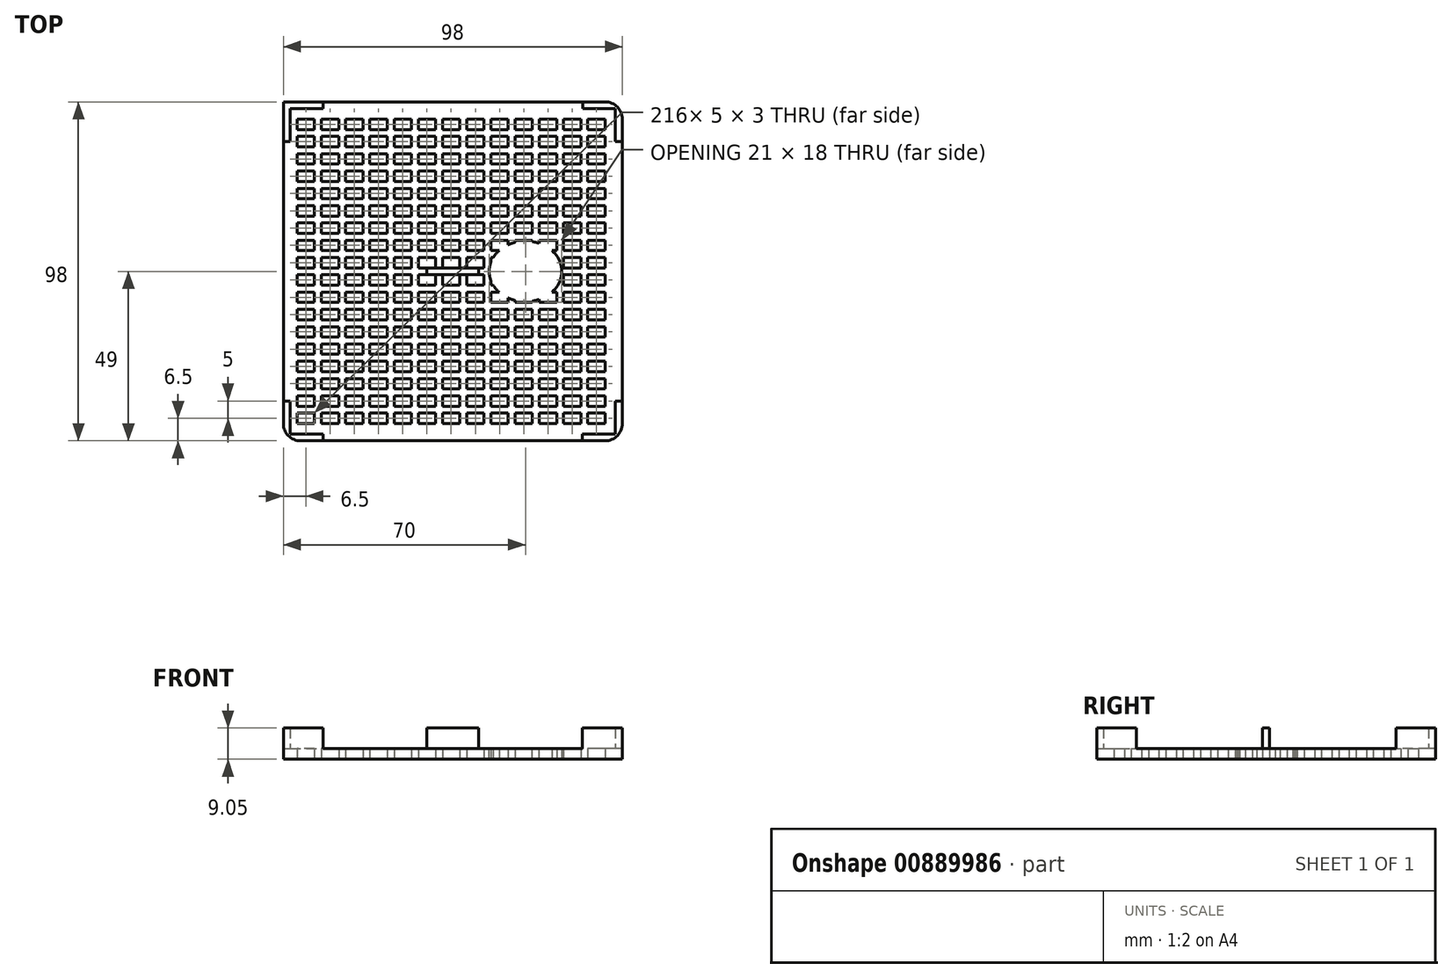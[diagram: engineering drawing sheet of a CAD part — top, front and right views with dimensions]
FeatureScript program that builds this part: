
annotation { "Feature Type Name" : "Feature", "Feature Type Description" : "" }
export const myFeature = defineFeature(function(context is Context, id is Id, definition is map)
    precondition{}
    {
        {
            var Q0;
            Q0=qCreatedBy(makeId("Top.planeOp"),FACE);
            var sketch = newSketch(context, id + "F0", { "sketchPlane" : qUnion([Q0])});
            skLineSegment(sketch, "E0.bottom", {"start": v(-49, 49) * mm, "end": v(49, 49) * mm});
            skLineSegment(sketch, "E0.top", {"start": v(-49, -49) * mm, "end": v(49, -49) * mm});
            skLineSegment(sketch, "E0.left", {"start": v(-49, 49) * mm, "end": v(-49, -49) * mm});
            skLineSegment(sketch, "E0.right", {"start": v(49, 49) * mm, "end": v(49, -49) * mm});
            skPoint(sketch, "E0.middle", {"position": v(0, 0) * mm});
            skLineSegment(sketch, "E1.bottom", {"start": v(-49, 49) * mm, "end": v(-42.5, 49) * mm});
            skLineSegment(sketch, "E1.top", {"start": v(-49, 42.5) * mm, "end": v(-42.5, 42.5) * mm});
            skLineSegment(sketch, "E1.left", {"start": v(-49, 49) * mm, "end": v(-49, 42.5) * mm});
            skLineSegment(sketch, "E1.right", {"start": v(-42.5, 49) * mm, "end": v(-42.5, 42.5) * mm});
            skLineSegment(sketch, "E2.bottom", {"start": v(-40, 41) * mm, "end": v(-45, 41) * mm});
            skLineSegment(sketch, "E2.top", {"start": v(-40, 44) * mm, "end": v(-45, 44) * mm});
            skLineSegment(sketch, "E2.left", {"start": v(-40, 41) * mm, "end": v(-40, 44) * mm});
            skLineSegment(sketch, "E2.right", {"start": v(-45, 41) * mm, "end": v(-45, 44) * mm});
            skPoint(sketch, "E2.middle", {"position": v(-42.5, 42.5) * mm});
            skLineSegment(sketch, "E3.1.0.0", {"start": v(-33, 41) * mm, "end": v(-33, 44) * mm});
            skLineSegment(sketch, "E3.1.0.1", {"start": v(-33, 44) * mm, "end": v(-38, 44) * mm});
            skLineSegment(sketch, "E3.1.0.2", {"start": v(-38, 41) * mm, "end": v(-38, 44) * mm});
            skLineSegment(sketch, "E3.1.0.3", {"start": v(-33, 41) * mm, "end": v(-38, 41) * mm});
            skLineSegment(sketch, "E3.2.0.0", {"start": v(-26, 41) * mm, "end": v(-26, 44) * mm});
            skLineSegment(sketch, "E3.2.0.1", {"start": v(-26, 44) * mm, "end": v(-31, 44) * mm});
            skLineSegment(sketch, "E3.2.0.2", {"start": v(-31, 41) * mm, "end": v(-31, 44) * mm});
            skLineSegment(sketch, "E3.2.0.3", {"start": v(-26, 41) * mm, "end": v(-31, 41) * mm});
            skLineSegment(sketch, "E3.3.0.0", {"start": v(-19, 41) * mm, "end": v(-19, 44) * mm});
            skLineSegment(sketch, "E3.3.0.1", {"start": v(-19, 44) * mm, "end": v(-24, 44) * mm});
            skLineSegment(sketch, "E3.3.0.2", {"start": v(-24, 41) * mm, "end": v(-24, 44) * mm});
            skLineSegment(sketch, "E3.3.0.3", {"start": v(-19, 41) * mm, "end": v(-24, 41) * mm});
            skLineSegment(sketch, "E3.4.0.0", {"start": v(-12, 41) * mm, "end": v(-12, 44) * mm});
            skLineSegment(sketch, "E3.4.0.1", {"start": v(-12, 44) * mm, "end": v(-17, 44) * mm});
            skLineSegment(sketch, "E3.4.0.2", {"start": v(-17, 41) * mm, "end": v(-17, 44) * mm});
            skLineSegment(sketch, "E3.4.0.3", {"start": v(-12, 41) * mm, "end": v(-17, 41) * mm});
            skLineSegment(sketch, "E3.5.0.0", {"start": v(-5, 41) * mm, "end": v(-5, 44) * mm});
            skLineSegment(sketch, "E3.5.0.1", {"start": v(-5, 44) * mm, "end": v(-10, 44) * mm});
            skLineSegment(sketch, "E3.5.0.2", {"start": v(-10, 41) * mm, "end": v(-10, 44) * mm});
            skLineSegment(sketch, "E3.5.0.3", {"start": v(-5, 41) * mm, "end": v(-10, 41) * mm});
            skLineSegment(sketch, "E3.6.0.0", {"start": v(2, 41) * mm, "end": v(2, 44) * mm});
            skLineSegment(sketch, "E3.6.0.1", {"start": v(2, 44) * mm, "end": v(-3, 44) * mm});
            skLineSegment(sketch, "E3.6.0.2", {"start": v(-3, 41) * mm, "end": v(-3, 44) * mm});
            skLineSegment(sketch, "E3.6.0.3", {"start": v(2, 41) * mm, "end": v(-3, 41) * mm});
            skLineSegment(sketch, "E3.7.0.0", {"start": v(9, 41) * mm, "end": v(9, 44) * mm});
            skLineSegment(sketch, "E3.7.0.1", {"start": v(9, 44) * mm, "end": v(4, 44) * mm});
            skLineSegment(sketch, "E3.7.0.2", {"start": v(4, 41) * mm, "end": v(4, 44) * mm});
            skLineSegment(sketch, "E3.7.0.3", {"start": v(9, 41) * mm, "end": v(4, 41) * mm});
            skLineSegment(sketch, "E3.8.0.0", {"start": v(16, 41) * mm, "end": v(16, 44) * mm});
            skLineSegment(sketch, "E3.8.0.1", {"start": v(16, 44) * mm, "end": v(11, 44) * mm});
            skLineSegment(sketch, "E3.8.0.2", {"start": v(11, 41) * mm, "end": v(11, 44) * mm});
            skLineSegment(sketch, "E3.8.0.3", {"start": v(16, 41) * mm, "end": v(11, 41) * mm});
            skLineSegment(sketch, "E3.9.0.0", {"start": v(23, 41) * mm, "end": v(23, 44) * mm});
            skLineSegment(sketch, "E3.9.0.1", {"start": v(23, 44) * mm, "end": v(18, 44) * mm});
            skLineSegment(sketch, "E3.9.0.2", {"start": v(18, 41) * mm, "end": v(18, 44) * mm});
            skLineSegment(sketch, "E3.9.0.3", {"start": v(23, 41) * mm, "end": v(18, 41) * mm});
            skLineSegment(sketch, "E3.10.0.0", {"start": v(30, 41) * mm, "end": v(30, 44) * mm});
            skLineSegment(sketch, "E3.10.0.1", {"start": v(30, 44) * mm, "end": v(25, 44) * mm});
            skLineSegment(sketch, "E3.10.0.2", {"start": v(25, 41) * mm, "end": v(25, 44) * mm});
            skLineSegment(sketch, "E3.10.0.3", {"start": v(30, 41) * mm, "end": v(25, 41) * mm});
            skLineSegment(sketch, "E4.0.11.0", {"start": v(37, 41) * mm, "end": v(37, 44) * mm});
            skLineSegment(sketch, "E4.3.11.0", {"start": v(37, 44) * mm, "end": v(32, 44) * mm});
            skLineSegment(sketch, "E4.6.11.0", {"start": v(32, 41) * mm, "end": v(32, 44) * mm});
            skLineSegment(sketch, "E4.9.11.0", {"start": v(37, 41) * mm, "end": v(32, 41) * mm});
            skLineSegment(sketch, "E5.0.12.0", {"start": v(44, 41) * mm, "end": v(44, 44) * mm});
            skLineSegment(sketch, "E5.3.12.0", {"start": v(44, 44) * mm, "end": v(39, 44) * mm});
            skLineSegment(sketch, "E5.6.12.0", {"start": v(39, 41) * mm, "end": v(39, 44) * mm});
            skLineSegment(sketch, "E5.9.12.0", {"start": v(44, 41) * mm, "end": v(39, 41) * mm});
            skLineSegment(sketch, "E6.1.0.0", {"start": v(-40, 36) * mm, "end": v(-45, 36) * mm});
            skLineSegment(sketch, "E6.1.0.1", {"start": v(-40, 36) * mm, "end": v(-40, 39) * mm});
            skLineSegment(sketch, "E6.1.0.2", {"start": v(-40, 39) * mm, "end": v(-45, 39) * mm});
            skLineSegment(sketch, "E6.1.0.3", {"start": v(-45, 36) * mm, "end": v(-45, 39) * mm});
            skLineSegment(sketch, "E6.2.0.0", {"start": v(-40, 31) * mm, "end": v(-45, 31) * mm});
            skLineSegment(sketch, "E6.2.0.1", {"start": v(-40, 31) * mm, "end": v(-40, 34) * mm});
            skLineSegment(sketch, "E6.2.0.2", {"start": v(-40, 34) * mm, "end": v(-45, 34) * mm});
            skLineSegment(sketch, "E6.2.0.3", {"start": v(-45, 31) * mm, "end": v(-45, 34) * mm});
            skLineSegment(sketch, "E6.3.0.0", {"start": v(-40, 26) * mm, "end": v(-45, 26) * mm});
            skLineSegment(sketch, "E6.3.0.1", {"start": v(-40, 26) * mm, "end": v(-40, 29) * mm});
            skLineSegment(sketch, "E6.3.0.2", {"start": v(-40, 29) * mm, "end": v(-45, 29) * mm});
            skLineSegment(sketch, "E6.3.0.3", {"start": v(-45, 26) * mm, "end": v(-45, 29) * mm});
            skLineSegment(sketch, "E6.4.0.0", {"start": v(-40, 21) * mm, "end": v(-45, 21) * mm});
            skLineSegment(sketch, "E6.4.0.1", {"start": v(-40, 21) * mm, "end": v(-40, 24) * mm});
            skLineSegment(sketch, "E6.4.0.2", {"start": v(-40, 24) * mm, "end": v(-45, 24) * mm});
            skLineSegment(sketch, "E6.4.0.3", {"start": v(-45, 21) * mm, "end": v(-45, 24) * mm});
            skLineSegment(sketch, "E6.5.0.0", {"start": v(-40, 16) * mm, "end": v(-45, 16) * mm});
            skLineSegment(sketch, "E6.5.0.1", {"start": v(-40, 16) * mm, "end": v(-40, 19) * mm});
            skLineSegment(sketch, "E6.5.0.2", {"start": v(-40, 19) * mm, "end": v(-45, 19) * mm});
            skLineSegment(sketch, "E6.5.0.3", {"start": v(-45, 16) * mm, "end": v(-45, 19) * mm});
            skLineSegment(sketch, "E6.6.0.0", {"start": v(-40, 11) * mm, "end": v(-45, 11) * mm});
            skLineSegment(sketch, "E6.6.0.1", {"start": v(-40, 11) * mm, "end": v(-40, 14) * mm});
            skLineSegment(sketch, "E6.6.0.2", {"start": v(-40, 14) * mm, "end": v(-45, 14) * mm});
            skLineSegment(sketch, "E6.6.0.3", {"start": v(-45, 11) * mm, "end": v(-45, 14) * mm});
            skLineSegment(sketch, "E6.7.0.0", {"start": v(-40, 6) * mm, "end": v(-45, 6) * mm});
            skLineSegment(sketch, "E6.7.0.1", {"start": v(-40, 6) * mm, "end": v(-40, 9) * mm});
            skLineSegment(sketch, "E6.7.0.2", {"start": v(-40, 9) * mm, "end": v(-45, 9) * mm});
            skLineSegment(sketch, "E6.7.0.3", {"start": v(-45, 6) * mm, "end": v(-45, 9) * mm});
            skLineSegment(sketch, "E6.8.0.0", {"start": v(-40, 1) * mm, "end": v(-45, 1) * mm});
            skLineSegment(sketch, "E6.8.0.1", {"start": v(-40, 1) * mm, "end": v(-40, 4) * mm});
            skLineSegment(sketch, "E6.8.0.2", {"start": v(-40, 4) * mm, "end": v(-45, 4) * mm});
            skLineSegment(sketch, "E6.8.0.3", {"start": v(-45, 1) * mm, "end": v(-45, 4) * mm});
            skLineSegment(sketch, "E6.9.0.0", {"start": v(-40, -4) * mm, "end": v(-45, -4) * mm});
            skLineSegment(sketch, "E6.9.0.1", {"start": v(-40, -4) * mm, "end": v(-40, -1) * mm});
            skLineSegment(sketch, "E6.9.0.2", {"start": v(-40, -1) * mm, "end": v(-45, -1) * mm});
            skLineSegment(sketch, "E6.9.0.3", {"start": v(-45, -4) * mm, "end": v(-45, -1) * mm});
            skLineSegment(sketch, "E6.10.0.0", {"start": v(-40, -9) * mm, "end": v(-45, -9) * mm});
            skLineSegment(sketch, "E6.10.0.1", {"start": v(-40, -9) * mm, "end": v(-40, -6) * mm});
            skLineSegment(sketch, "E6.10.0.2", {"start": v(-40, -6) * mm, "end": v(-45, -6) * mm});
            skLineSegment(sketch, "E6.10.0.3", {"start": v(-45, -9) * mm, "end": v(-45, -6) * mm});
            skLineSegment(sketch, "E6.11.0.0", {"start": v(-40, -14) * mm, "end": v(-45, -14) * mm});
            skLineSegment(sketch, "E6.11.0.1", {"start": v(-40, -14) * mm, "end": v(-40, -11) * mm});
            skLineSegment(sketch, "E6.11.0.2", {"start": v(-40, -11) * mm, "end": v(-45, -11) * mm});
            skLineSegment(sketch, "E6.11.0.3", {"start": v(-45, -14) * mm, "end": v(-45, -11) * mm});
            skLineSegment(sketch, "E6.12.0.0", {"start": v(-40, -19) * mm, "end": v(-45, -19) * mm});
            skLineSegment(sketch, "E6.12.0.1", {"start": v(-40, -19) * mm, "end": v(-40, -16) * mm});
            skLineSegment(sketch, "E6.12.0.2", {"start": v(-40, -16) * mm, "end": v(-45, -16) * mm});
            skLineSegment(sketch, "E6.12.0.3", {"start": v(-45, -19) * mm, "end": v(-45, -16) * mm});
            skLineSegment(sketch, "E6.13.0.0", {"start": v(-40, -24) * mm, "end": v(-45, -24) * mm});
            skLineSegment(sketch, "E6.13.0.1", {"start": v(-40, -24) * mm, "end": v(-40, -21) * mm});
            skLineSegment(sketch, "E6.13.0.2", {"start": v(-40, -21) * mm, "end": v(-45, -21) * mm});
            skLineSegment(sketch, "E6.13.0.3", {"start": v(-45, -24) * mm, "end": v(-45, -21) * mm});
            skLineSegment(sketch, "E6.14.0.0", {"start": v(-40, -29) * mm, "end": v(-45, -29) * mm});
            skLineSegment(sketch, "E6.14.0.1", {"start": v(-40, -29) * mm, "end": v(-40, -26) * mm});
            skLineSegment(sketch, "E6.14.0.2", {"start": v(-40, -26) * mm, "end": v(-45, -26) * mm});
            skLineSegment(sketch, "E6.14.0.3", {"start": v(-45, -29) * mm, "end": v(-45, -26) * mm});
            skLineSegment(sketch, "E6.15.0.0", {"start": v(-40, -34) * mm, "end": v(-45, -34) * mm});
            skLineSegment(sketch, "E6.15.0.1", {"start": v(-40, -34) * mm, "end": v(-40, -31) * mm});
            skLineSegment(sketch, "E6.15.0.2", {"start": v(-40, -31) * mm, "end": v(-45, -31) * mm});
            skLineSegment(sketch, "E6.15.0.3", {"start": v(-45, -34) * mm, "end": v(-45, -31) * mm});
            skLineSegment(sketch, "E6.16.0.0", {"start": v(-40, -39) * mm, "end": v(-45, -39) * mm});
            skLineSegment(sketch, "E6.16.0.1", {"start": v(-40, -39) * mm, "end": v(-40, -36) * mm});
            skLineSegment(sketch, "E6.16.0.2", {"start": v(-40, -36) * mm, "end": v(-45, -36) * mm});
            skLineSegment(sketch, "E6.16.0.3", {"start": v(-45, -39) * mm, "end": v(-45, -36) * mm});
            skLineSegment(sketch, "E6.17.0.0", {"start": v(-40, -44) * mm, "end": v(-45, -44) * mm});
            skLineSegment(sketch, "E6.17.0.1", {"start": v(-40, -44) * mm, "end": v(-40, -41) * mm});
            skLineSegment(sketch, "E6.17.0.2", {"start": v(-40, -41) * mm, "end": v(-45, -41) * mm});
            skLineSegment(sketch, "E6.17.0.3", {"start": v(-45, -44) * mm, "end": v(-45, -41) * mm});
            skLineSegment(sketch, "E7.1.0.0", {"start": v(-33, 39) * mm, "end": v(-38, 39) * mm});
            skLineSegment(sketch, "E7.1.0.1", {"start": v(-38, 36) * mm, "end": v(-38, 39) * mm});
            skLineSegment(sketch, "E7.1.0.2", {"start": v(-33, 36) * mm, "end": v(-33, 39) * mm});
            skLineSegment(sketch, "E7.1.0.3", {"start": v(-33, 36) * mm, "end": v(-38, 36) * mm});
            skLineSegment(sketch, "E7.2.0.0", {"start": v(-26, 39) * mm, "end": v(-31, 39) * mm});
            skLineSegment(sketch, "E7.2.0.1", {"start": v(-31, 36) * mm, "end": v(-31, 39) * mm});
            skLineSegment(sketch, "E7.2.0.2", {"start": v(-26, 36) * mm, "end": v(-26, 39) * mm});
            skLineSegment(sketch, "E7.2.0.3", {"start": v(-26, 36) * mm, "end": v(-31, 36) * mm});
            skLineSegment(sketch, "E7.3.0.0", {"start": v(-19, 39) * mm, "end": v(-24, 39) * mm});
            skLineSegment(sketch, "E7.3.0.1", {"start": v(-24, 36) * mm, "end": v(-24, 39) * mm});
            skLineSegment(sketch, "E7.3.0.2", {"start": v(-19, 36) * mm, "end": v(-19, 39) * mm});
            skLineSegment(sketch, "E7.3.0.3", {"start": v(-19, 36) * mm, "end": v(-24, 36) * mm});
            skLineSegment(sketch, "E7.4.0.0", {"start": v(-12, 39) * mm, "end": v(-17, 39) * mm});
            skLineSegment(sketch, "E7.4.0.1", {"start": v(-17, 36) * mm, "end": v(-17, 39) * mm});
            skLineSegment(sketch, "E7.4.0.2", {"start": v(-12, 36) * mm, "end": v(-12, 39) * mm});
            skLineSegment(sketch, "E7.4.0.3", {"start": v(-12, 36) * mm, "end": v(-17, 36) * mm});
            skLineSegment(sketch, "E7.5.0.0", {"start": v(-5, 39) * mm, "end": v(-10, 39) * mm});
            skLineSegment(sketch, "E7.5.0.1", {"start": v(-10, 36) * mm, "end": v(-10, 39) * mm});
            skLineSegment(sketch, "E7.5.0.2", {"start": v(-5, 36) * mm, "end": v(-5, 39) * mm});
            skLineSegment(sketch, "E7.5.0.3", {"start": v(-5, 36) * mm, "end": v(-10, 36) * mm});
            skLineSegment(sketch, "E7.6.0.0", {"start": v(2, 39) * mm, "end": v(-3, 39) * mm});
            skLineSegment(sketch, "E7.6.0.1", {"start": v(-3, 36) * mm, "end": v(-3, 39) * mm});
            skLineSegment(sketch, "E7.6.0.2", {"start": v(2, 36) * mm, "end": v(2, 39) * mm});
            skLineSegment(sketch, "E7.6.0.3", {"start": v(2, 36) * mm, "end": v(-3, 36) * mm});
            skLineSegment(sketch, "E7.7.0.0", {"start": v(9, 39) * mm, "end": v(4, 39) * mm});
            skLineSegment(sketch, "E7.7.0.1", {"start": v(4, 36) * mm, "end": v(4, 39) * mm});
            skLineSegment(sketch, "E7.7.0.2", {"start": v(9, 36) * mm, "end": v(9, 39) * mm});
            skLineSegment(sketch, "E7.7.0.3", {"start": v(9, 36) * mm, "end": v(4, 36) * mm});
            skLineSegment(sketch, "E7.8.0.0", {"start": v(16, 39) * mm, "end": v(11, 39) * mm});
            skLineSegment(sketch, "E7.8.0.1", {"start": v(11, 36) * mm, "end": v(11, 39) * mm});
            skLineSegment(sketch, "E7.8.0.2", {"start": v(16, 36) * mm, "end": v(16, 39) * mm});
            skLineSegment(sketch, "E7.8.0.3", {"start": v(16, 36) * mm, "end": v(11, 36) * mm});
            skLineSegment(sketch, "E7.9.0.0", {"start": v(23, 39) * mm, "end": v(18, 39) * mm});
            skLineSegment(sketch, "E7.9.0.1", {"start": v(18, 36) * mm, "end": v(18, 39) * mm});
            skLineSegment(sketch, "E7.9.0.2", {"start": v(23, 36) * mm, "end": v(23, 39) * mm});
            skLineSegment(sketch, "E7.9.0.3", {"start": v(23, 36) * mm, "end": v(18, 36) * mm});
            skLineSegment(sketch, "E7.10.0.0", {"start": v(30, 39) * mm, "end": v(25, 39) * mm});
            skLineSegment(sketch, "E7.10.0.1", {"start": v(25, 36) * mm, "end": v(25, 39) * mm});
            skLineSegment(sketch, "E7.10.0.2", {"start": v(30, 36) * mm, "end": v(30, 39) * mm});
            skLineSegment(sketch, "E7.10.0.3", {"start": v(30, 36) * mm, "end": v(25, 36) * mm});
            skLineSegment(sketch, "E7.11.0.0", {"start": v(37, 39) * mm, "end": v(32, 39) * mm});
            skLineSegment(sketch, "E7.11.0.1", {"start": v(32, 36) * mm, "end": v(32, 39) * mm});
            skLineSegment(sketch, "E7.11.0.2", {"start": v(37, 36) * mm, "end": v(37, 39) * mm});
            skLineSegment(sketch, "E7.11.0.3", {"start": v(37, 36) * mm, "end": v(32, 36) * mm});
            skLineSegment(sketch, "E7.12.0.0", {"start": v(44, 39) * mm, "end": v(39, 39) * mm});
            skLineSegment(sketch, "E7.12.0.1", {"start": v(39, 36) * mm, "end": v(39, 39) * mm});
            skLineSegment(sketch, "E7.12.0.2", {"start": v(44, 36) * mm, "end": v(44, 39) * mm});
            skLineSegment(sketch, "E7.12.0.3", {"start": v(44, 36) * mm, "end": v(39, 36) * mm});
            skLineSegment(sketch, "E8.1.0.0", {"start": v(-33, 31) * mm, "end": v(-33, 34) * mm});
            skLineSegment(sketch, "E8.1.0.1", {"start": v(-38, 31) * mm, "end": v(-38, 34) * mm});
            skLineSegment(sketch, "E8.1.0.2", {"start": v(-33, 34) * mm, "end": v(-38, 34) * mm});
            skLineSegment(sketch, "E8.1.0.3", {"start": v(-33, 31) * mm, "end": v(-38, 31) * mm});
            skLineSegment(sketch, "E8.2.0.0", {"start": v(-26, 31) * mm, "end": v(-26, 34) * mm});
            skLineSegment(sketch, "E8.2.0.1", {"start": v(-31, 31) * mm, "end": v(-31, 34) * mm});
            skLineSegment(sketch, "E8.2.0.2", {"start": v(-26, 34) * mm, "end": v(-31, 34) * mm});
            skLineSegment(sketch, "E8.2.0.3", {"start": v(-26, 31) * mm, "end": v(-31, 31) * mm});
            skLineSegment(sketch, "E8.3.0.0", {"start": v(-19, 31) * mm, "end": v(-19, 34) * mm});
            skLineSegment(sketch, "E8.3.0.1", {"start": v(-24, 31) * mm, "end": v(-24, 34) * mm});
            skLineSegment(sketch, "E8.3.0.2", {"start": v(-19, 34) * mm, "end": v(-24, 34) * mm});
            skLineSegment(sketch, "E8.3.0.3", {"start": v(-19, 31) * mm, "end": v(-24, 31) * mm});
            skLineSegment(sketch, "E8.4.0.0", {"start": v(-12, 31) * mm, "end": v(-12, 34) * mm});
            skLineSegment(sketch, "E8.4.0.1", {"start": v(-17, 31) * mm, "end": v(-17, 34) * mm});
            skLineSegment(sketch, "E8.4.0.2", {"start": v(-12, 34) * mm, "end": v(-17, 34) * mm});
            skLineSegment(sketch, "E8.4.0.3", {"start": v(-12, 31) * mm, "end": v(-17, 31) * mm});
            skLineSegment(sketch, "E8.5.0.0", {"start": v(-5, 31) * mm, "end": v(-5, 34) * mm});
            skLineSegment(sketch, "E8.5.0.1", {"start": v(-10, 31) * mm, "end": v(-10, 34) * mm});
            skLineSegment(sketch, "E8.5.0.2", {"start": v(-5, 34) * mm, "end": v(-10, 34) * mm});
            skLineSegment(sketch, "E8.5.0.3", {"start": v(-5, 31) * mm, "end": v(-10, 31) * mm});
            skLineSegment(sketch, "E8.6.0.0", {"start": v(2, 31) * mm, "end": v(2, 34) * mm});
            skLineSegment(sketch, "E8.6.0.1", {"start": v(-3, 31) * mm, "end": v(-3, 34) * mm});
            skLineSegment(sketch, "E8.6.0.2", {"start": v(2, 34) * mm, "end": v(-3, 34) * mm});
            skLineSegment(sketch, "E8.6.0.3", {"start": v(2, 31) * mm, "end": v(-3, 31) * mm});
            skLineSegment(sketch, "E8.7.0.0", {"start": v(9, 31) * mm, "end": v(9, 34) * mm});
            skLineSegment(sketch, "E8.7.0.1", {"start": v(4, 31) * mm, "end": v(4, 34) * mm});
            skLineSegment(sketch, "E8.7.0.2", {"start": v(9, 34) * mm, "end": v(4, 34) * mm});
            skLineSegment(sketch, "E8.7.0.3", {"start": v(9, 31) * mm, "end": v(4, 31) * mm});
            skLineSegment(sketch, "E8.8.0.0", {"start": v(16, 31) * mm, "end": v(16, 34) * mm});
            skLineSegment(sketch, "E8.8.0.1", {"start": v(11, 31) * mm, "end": v(11, 34) * mm});
            skLineSegment(sketch, "E8.8.0.2", {"start": v(16, 34) * mm, "end": v(11, 34) * mm});
            skLineSegment(sketch, "E8.8.0.3", {"start": v(16, 31) * mm, "end": v(11, 31) * mm});
            skLineSegment(sketch, "E8.9.0.0", {"start": v(23, 31) * mm, "end": v(23, 34) * mm});
            skLineSegment(sketch, "E8.9.0.1", {"start": v(18, 31) * mm, "end": v(18, 34) * mm});
            skLineSegment(sketch, "E8.9.0.2", {"start": v(23, 34) * mm, "end": v(18, 34) * mm});
            skLineSegment(sketch, "E8.9.0.3", {"start": v(23, 31) * mm, "end": v(18, 31) * mm});
            skLineSegment(sketch, "E8.10.0.0", {"start": v(30, 31) * mm, "end": v(30, 34) * mm});
            skLineSegment(sketch, "E8.10.0.1", {"start": v(25, 31) * mm, "end": v(25, 34) * mm});
            skLineSegment(sketch, "E8.10.0.2", {"start": v(30, 34) * mm, "end": v(25, 34) * mm});
            skLineSegment(sketch, "E8.10.0.3", {"start": v(30, 31) * mm, "end": v(25, 31) * mm});
            skLineSegment(sketch, "E8.11.0.0", {"start": v(37, 31) * mm, "end": v(37, 34) * mm});
            skLineSegment(sketch, "E8.11.0.1", {"start": v(32, 31) * mm, "end": v(32, 34) * mm});
            skLineSegment(sketch, "E8.11.0.2", {"start": v(37, 34) * mm, "end": v(32, 34) * mm});
            skLineSegment(sketch, "E8.11.0.3", {"start": v(37, 31) * mm, "end": v(32, 31) * mm});
            skLineSegment(sketch, "E8.12.0.0", {"start": v(44, 31) * mm, "end": v(44, 34) * mm});
            skLineSegment(sketch, "E8.12.0.1", {"start": v(39, 31) * mm, "end": v(39, 34) * mm});
            skLineSegment(sketch, "E8.12.0.2", {"start": v(44, 34) * mm, "end": v(39, 34) * mm});
            skLineSegment(sketch, "E8.12.0.3", {"start": v(44, 31) * mm, "end": v(39, 31) * mm});
            skLineSegment(sketch, "E9.1.0.0", {"start": v(-33, 29) * mm, "end": v(-38, 29) * mm});
            skLineSegment(sketch, "E9.1.0.1", {"start": v(-38, 26) * mm, "end": v(-38, 29) * mm});
            skLineSegment(sketch, "E9.1.0.2", {"start": v(-33, 26) * mm, "end": v(-38, 26) * mm});
            skLineSegment(sketch, "E9.1.0.3", {"start": v(-33, 26) * mm, "end": v(-33, 29) * mm});
            skLineSegment(sketch, "E9.2.0.0", {"start": v(-26, 29) * mm, "end": v(-31, 29) * mm});
            skLineSegment(sketch, "E9.2.0.1", {"start": v(-31, 26) * mm, "end": v(-31, 29) * mm});
            skLineSegment(sketch, "E9.2.0.2", {"start": v(-26, 26) * mm, "end": v(-31, 26) * mm});
            skLineSegment(sketch, "E9.2.0.3", {"start": v(-26, 26) * mm, "end": v(-26, 29) * mm});
            skLineSegment(sketch, "E9.3.0.0", {"start": v(-19, 29) * mm, "end": v(-24, 29) * mm});
            skLineSegment(sketch, "E9.3.0.1", {"start": v(-24, 26) * mm, "end": v(-24, 29) * mm});
            skLineSegment(sketch, "E9.3.0.2", {"start": v(-19, 26) * mm, "end": v(-24, 26) * mm});
            skLineSegment(sketch, "E9.3.0.3", {"start": v(-19, 26) * mm, "end": v(-19, 29) * mm});
            skLineSegment(sketch, "E9.4.0.0", {"start": v(-12, 29) * mm, "end": v(-17, 29) * mm});
            skLineSegment(sketch, "E9.4.0.1", {"start": v(-17, 26) * mm, "end": v(-17, 29) * mm});
            skLineSegment(sketch, "E9.4.0.2", {"start": v(-12, 26) * mm, "end": v(-17, 26) * mm});
            skLineSegment(sketch, "E9.4.0.3", {"start": v(-12, 26) * mm, "end": v(-12, 29) * mm});
            skLineSegment(sketch, "E9.5.0.0", {"start": v(-5, 29) * mm, "end": v(-10, 29) * mm});
            skLineSegment(sketch, "E9.5.0.1", {"start": v(-10, 26) * mm, "end": v(-10, 29) * mm});
            skLineSegment(sketch, "E9.5.0.2", {"start": v(-5, 26) * mm, "end": v(-10, 26) * mm});
            skLineSegment(sketch, "E9.5.0.3", {"start": v(-5, 26) * mm, "end": v(-5, 29) * mm});
            skLineSegment(sketch, "E9.6.0.0", {"start": v(2, 29) * mm, "end": v(-3, 29) * mm});
            skLineSegment(sketch, "E9.6.0.1", {"start": v(-3, 26) * mm, "end": v(-3, 29) * mm});
            skLineSegment(sketch, "E9.6.0.2", {"start": v(2, 26) * mm, "end": v(-3, 26) * mm});
            skLineSegment(sketch, "E9.6.0.3", {"start": v(2, 26) * mm, "end": v(2, 29) * mm});
            skLineSegment(sketch, "E9.7.0.0", {"start": v(9, 29) * mm, "end": v(4, 29) * mm});
            skLineSegment(sketch, "E9.7.0.1", {"start": v(4, 26) * mm, "end": v(4, 29) * mm});
            skLineSegment(sketch, "E9.7.0.2", {"start": v(9, 26) * mm, "end": v(4, 26) * mm});
            skLineSegment(sketch, "E9.7.0.3", {"start": v(9, 26) * mm, "end": v(9, 29) * mm});
            skLineSegment(sketch, "E9.8.0.0", {"start": v(16, 29) * mm, "end": v(11, 29) * mm});
            skLineSegment(sketch, "E9.8.0.1", {"start": v(11, 26) * mm, "end": v(11, 29) * mm});
            skLineSegment(sketch, "E9.8.0.2", {"start": v(16, 26) * mm, "end": v(11, 26) * mm});
            skLineSegment(sketch, "E9.8.0.3", {"start": v(16, 26) * mm, "end": v(16, 29) * mm});
            skLineSegment(sketch, "E9.9.0.0", {"start": v(23, 29) * mm, "end": v(18, 29) * mm});
            skLineSegment(sketch, "E9.9.0.1", {"start": v(18, 26) * mm, "end": v(18, 29) * mm});
            skLineSegment(sketch, "E9.9.0.2", {"start": v(23, 26) * mm, "end": v(18, 26) * mm});
            skLineSegment(sketch, "E9.9.0.3", {"start": v(23, 26) * mm, "end": v(23, 29) * mm});
            skLineSegment(sketch, "E9.10.0.0", {"start": v(30, 29) * mm, "end": v(25, 29) * mm});
            skLineSegment(sketch, "E9.10.0.1", {"start": v(25, 26) * mm, "end": v(25, 29) * mm});
            skLineSegment(sketch, "E9.10.0.2", {"start": v(30, 26) * mm, "end": v(25, 26) * mm});
            skLineSegment(sketch, "E9.10.0.3", {"start": v(30, 26) * mm, "end": v(30, 29) * mm});
            skLineSegment(sketch, "E9.11.0.0", {"start": v(37, 29) * mm, "end": v(32, 29) * mm});
            skLineSegment(sketch, "E9.11.0.1", {"start": v(32, 26) * mm, "end": v(32, 29) * mm});
            skLineSegment(sketch, "E9.11.0.2", {"start": v(37, 26) * mm, "end": v(32, 26) * mm});
            skLineSegment(sketch, "E9.11.0.3", {"start": v(37, 26) * mm, "end": v(37, 29) * mm});
            skLineSegment(sketch, "E9.12.0.0", {"start": v(44, 29) * mm, "end": v(39, 29) * mm});
            skLineSegment(sketch, "E9.12.0.1", {"start": v(39, 26) * mm, "end": v(39, 29) * mm});
            skLineSegment(sketch, "E9.12.0.2", {"start": v(44, 26) * mm, "end": v(39, 26) * mm});
            skLineSegment(sketch, "E9.12.0.3", {"start": v(44, 26) * mm, "end": v(44, 29) * mm});
            skLineSegment(sketch, "E10.1.0.0", {"start": v(-26, 21) * mm, "end": v(-31, 21) * mm});
            skLineSegment(sketch, "E10.1.0.1", {"start": v(-31, 21) * mm, "end": v(-31, 24) * mm});
            skLineSegment(sketch, "E10.1.0.2", {"start": v(-26, 24) * mm, "end": v(-31, 24) * mm});
            skLineSegment(sketch, "E10.1.0.3", {"start": v(-26, 21) * mm, "end": v(-26, 24) * mm});
            skLineSegment(sketch, "E10.1.0.4", {"start": v(-33, 21) * mm, "end": v(-33, 24) * mm});
            skLineSegment(sketch, "E10.1.0.5", {"start": v(-33, 24) * mm, "end": v(-38, 24) * mm});
            skLineSegment(sketch, "E10.1.0.6", {"start": v(-38, 21) * mm, "end": v(-38, 24) * mm});
            skLineSegment(sketch, "E10.1.0.7", {"start": v(-33, 21) * mm, "end": v(-38, 21) * mm});
            skLineSegment(sketch, "E10.1.0.8", {"start": v(-19, 21) * mm, "end": v(-24, 21) * mm});
            skLineSegment(sketch, "E10.1.0.9", {"start": v(-19, 24) * mm, "end": v(-24, 24) * mm});
            skLineSegment(sketch, "E10.1.0.10", {"start": v(-24, 21) * mm, "end": v(-24, 24) * mm});
            skLineSegment(sketch, "E10.1.0.11", {"start": v(-19, 21) * mm, "end": v(-19, 24) * mm});
            skLineSegment(sketch, "E10.1.0.12", {"start": v(-17, 21) * mm, "end": v(-17, 24) * mm});
            skLineSegment(sketch, "E10.1.0.13", {"start": v(-12, 24) * mm, "end": v(-17, 24) * mm});
            skLineSegment(sketch, "E10.1.0.14", {"start": v(-12, 21) * mm, "end": v(-17, 21) * mm});
            skLineSegment(sketch, "E10.1.0.15", {"start": v(-12, 21) * mm, "end": v(-12, 24) * mm});
            skLineSegment(sketch, "E10.1.0.16", {"start": v(-5, 24) * mm, "end": v(-10, 24) * mm});
            skLineSegment(sketch, "E10.1.0.17", {"start": v(-5, 21) * mm, "end": v(-10, 21) * mm});
            skLineSegment(sketch, "E10.1.0.18", {"start": v(-10, 21) * mm, "end": v(-10, 24) * mm});
            skLineSegment(sketch, "E10.1.0.19", {"start": v(-5, 21) * mm, "end": v(-5, 24) * mm});
            skLineSegment(sketch, "E10.2.0.0", {"start": v(-26, 16) * mm, "end": v(-31, 16) * mm});
            skLineSegment(sketch, "E10.2.0.1", {"start": v(-31, 16) * mm, "end": v(-31, 19) * mm});
            skLineSegment(sketch, "E10.2.0.2", {"start": v(-26, 19) * mm, "end": v(-31, 19) * mm});
            skLineSegment(sketch, "E10.2.0.3", {"start": v(-26, 16) * mm, "end": v(-26, 19) * mm});
            skLineSegment(sketch, "E10.2.0.4", {"start": v(-33, 16) * mm, "end": v(-33, 19) * mm});
            skLineSegment(sketch, "E10.2.0.5", {"start": v(-33, 19) * mm, "end": v(-38, 19) * mm});
            skLineSegment(sketch, "E10.2.0.6", {"start": v(-38, 16) * mm, "end": v(-38, 19) * mm});
            skLineSegment(sketch, "E10.2.0.7", {"start": v(-33, 16) * mm, "end": v(-38, 16) * mm});
            skLineSegment(sketch, "E10.2.0.8", {"start": v(-19, 16) * mm, "end": v(-24, 16) * mm});
            skLineSegment(sketch, "E10.2.0.9", {"start": v(-19, 19) * mm, "end": v(-24, 19) * mm});
            skLineSegment(sketch, "E10.2.0.10", {"start": v(-24, 16) * mm, "end": v(-24, 19) * mm});
            skLineSegment(sketch, "E10.2.0.11", {"start": v(-19, 16) * mm, "end": v(-19, 19) * mm});
            skLineSegment(sketch, "E10.2.0.12", {"start": v(-17, 16) * mm, "end": v(-17, 19) * mm});
            skLineSegment(sketch, "E10.2.0.13", {"start": v(-12, 19) * mm, "end": v(-17, 19) * mm});
            skLineSegment(sketch, "E10.2.0.14", {"start": v(-12, 16) * mm, "end": v(-17, 16) * mm});
            skLineSegment(sketch, "E10.2.0.15", {"start": v(-12, 16) * mm, "end": v(-12, 19) * mm});
            skLineSegment(sketch, "E10.2.0.16", {"start": v(-5, 19) * mm, "end": v(-10, 19) * mm});
            skLineSegment(sketch, "E10.2.0.17", {"start": v(-5, 16) * mm, "end": v(-10, 16) * mm});
            skLineSegment(sketch, "E10.2.0.18", {"start": v(-10, 16) * mm, "end": v(-10, 19) * mm});
            skLineSegment(sketch, "E10.2.0.19", {"start": v(-5, 16) * mm, "end": v(-5, 19) * mm});
            skLineSegment(sketch, "E10.3.0.0", {"start": v(-26, 11) * mm, "end": v(-31, 11) * mm});
            skLineSegment(sketch, "E10.3.0.1", {"start": v(-31, 11) * mm, "end": v(-31, 14) * mm});
            skLineSegment(sketch, "E10.3.0.2", {"start": v(-26, 14) * mm, "end": v(-31, 14) * mm});
            skLineSegment(sketch, "E10.3.0.3", {"start": v(-26, 11) * mm, "end": v(-26, 14) * mm});
            skLineSegment(sketch, "E10.3.0.4", {"start": v(-33, 11) * mm, "end": v(-33, 14) * mm});
            skLineSegment(sketch, "E10.3.0.5", {"start": v(-33, 14) * mm, "end": v(-38, 14) * mm});
            skLineSegment(sketch, "E10.3.0.6", {"start": v(-38, 11) * mm, "end": v(-38, 14) * mm});
            skLineSegment(sketch, "E10.3.0.7", {"start": v(-33, 11) * mm, "end": v(-38, 11) * mm});
            skLineSegment(sketch, "E10.3.0.8", {"start": v(-19, 11) * mm, "end": v(-24, 11) * mm});
            skLineSegment(sketch, "E10.3.0.9", {"start": v(-19, 14) * mm, "end": v(-24, 14) * mm});
            skLineSegment(sketch, "E10.3.0.10", {"start": v(-24, 11) * mm, "end": v(-24, 14) * mm});
            skLineSegment(sketch, "E10.3.0.11", {"start": v(-19, 11) * mm, "end": v(-19, 14) * mm});
            skLineSegment(sketch, "E10.3.0.12", {"start": v(-17, 11) * mm, "end": v(-17, 14) * mm});
            skLineSegment(sketch, "E10.3.0.13", {"start": v(-12, 14) * mm, "end": v(-17, 14) * mm});
            skLineSegment(sketch, "E10.3.0.14", {"start": v(-12, 11) * mm, "end": v(-17, 11) * mm});
            skLineSegment(sketch, "E10.3.0.15", {"start": v(-12, 11) * mm, "end": v(-12, 14) * mm});
            skLineSegment(sketch, "E10.3.0.16", {"start": v(-5, 14) * mm, "end": v(-10, 14) * mm});
            skLineSegment(sketch, "E10.3.0.17", {"start": v(-5, 11) * mm, "end": v(-10, 11) * mm});
            skLineSegment(sketch, "E10.3.0.18", {"start": v(-10, 11) * mm, "end": v(-10, 14) * mm});
            skLineSegment(sketch, "E10.3.0.19", {"start": v(-5, 11) * mm, "end": v(-5, 14) * mm});
            skLineSegment(sketch, "E10.4.0.0", {"start": v(-26, 6) * mm, "end": v(-31, 6) * mm});
            skLineSegment(sketch, "E10.4.0.1", {"start": v(-31, 6) * mm, "end": v(-31, 9) * mm});
            skLineSegment(sketch, "E10.4.0.2", {"start": v(-26, 9) * mm, "end": v(-31, 9) * mm});
            skLineSegment(sketch, "E10.4.0.3", {"start": v(-26, 6) * mm, "end": v(-26, 9) * mm});
            skLineSegment(sketch, "E10.4.0.4", {"start": v(-33, 6) * mm, "end": v(-33, 9) * mm});
            skLineSegment(sketch, "E10.4.0.5", {"start": v(-33, 9) * mm, "end": v(-38, 9) * mm});
            skLineSegment(sketch, "E10.4.0.6", {"start": v(-38, 6) * mm, "end": v(-38, 9) * mm});
            skLineSegment(sketch, "E10.4.0.7", {"start": v(-33, 6) * mm, "end": v(-38, 6) * mm});
            skLineSegment(sketch, "E10.4.0.8", {"start": v(-19, 6) * mm, "end": v(-24, 6) * mm});
            skLineSegment(sketch, "E10.4.0.9", {"start": v(-19, 9) * mm, "end": v(-24, 9) * mm});
            skLineSegment(sketch, "E10.4.0.10", {"start": v(-24, 6) * mm, "end": v(-24, 9) * mm});
            skLineSegment(sketch, "E10.4.0.11", {"start": v(-19, 6) * mm, "end": v(-19, 9) * mm});
            skLineSegment(sketch, "E10.4.0.12", {"start": v(-17, 6) * mm, "end": v(-17, 9) * mm});
            skLineSegment(sketch, "E10.4.0.13", {"start": v(-12, 9) * mm, "end": v(-17, 9) * mm});
            skLineSegment(sketch, "E10.4.0.14", {"start": v(-12, 6) * mm, "end": v(-17, 6) * mm});
            skLineSegment(sketch, "E10.4.0.15", {"start": v(-12, 6) * mm, "end": v(-12, 9) * mm});
            skLineSegment(sketch, "E10.4.0.16", {"start": v(-5, 9) * mm, "end": v(-10, 9) * mm});
            skLineSegment(sketch, "E10.4.0.17", {"start": v(-5, 6) * mm, "end": v(-10, 6) * mm});
            skLineSegment(sketch, "E10.4.0.18", {"start": v(-10, 6) * mm, "end": v(-10, 9) * mm});
            skLineSegment(sketch, "E10.4.0.19", {"start": v(-5, 6) * mm, "end": v(-5, 9) * mm});
            skLineSegment(sketch, "E10.5.0.0", {"start": v(-26, 1) * mm, "end": v(-31, 1) * mm});
            skLineSegment(sketch, "E10.5.0.1", {"start": v(-31, 1) * mm, "end": v(-31, 4) * mm});
            skLineSegment(sketch, "E10.5.0.2", {"start": v(-26, 4) * mm, "end": v(-31, 4) * mm});
            skLineSegment(sketch, "E10.5.0.3", {"start": v(-26, 1) * mm, "end": v(-26, 4) * mm});
            skLineSegment(sketch, "E10.5.0.4", {"start": v(-33, 1) * mm, "end": v(-33, 4) * mm});
            skLineSegment(sketch, "E10.5.0.5", {"start": v(-33, 4) * mm, "end": v(-38, 4) * mm});
            skLineSegment(sketch, "E10.5.0.6", {"start": v(-38, 1) * mm, "end": v(-38, 4) * mm});
            skLineSegment(sketch, "E10.5.0.7", {"start": v(-33, 1) * mm, "end": v(-38, 1) * mm});
            skLineSegment(sketch, "E10.5.0.8", {"start": v(-19, 1) * mm, "end": v(-24, 1) * mm});
            skLineSegment(sketch, "E10.5.0.9", {"start": v(-19, 4) * mm, "end": v(-24, 4) * mm});
            skLineSegment(sketch, "E10.5.0.10", {"start": v(-24, 1) * mm, "end": v(-24, 4) * mm});
            skLineSegment(sketch, "E10.5.0.11", {"start": v(-19, 1) * mm, "end": v(-19, 4) * mm});
            skLineSegment(sketch, "E10.5.0.12", {"start": v(-17, 1) * mm, "end": v(-17, 4) * mm});
            skLineSegment(sketch, "E10.5.0.13", {"start": v(-12, 4) * mm, "end": v(-17, 4) * mm});
            skLineSegment(sketch, "E10.5.0.14", {"start": v(-12, 1) * mm, "end": v(-17, 1) * mm});
            skLineSegment(sketch, "E10.5.0.15", {"start": v(-12, 1) * mm, "end": v(-12, 4) * mm});
            skLineSegment(sketch, "E10.5.0.16", {"start": v(-5, 4) * mm, "end": v(-10, 4) * mm});
            skLineSegment(sketch, "E10.5.0.17", {"start": v(-5, 1) * mm, "end": v(-10, 1) * mm});
            skLineSegment(sketch, "E10.5.0.18", {"start": v(-10, 1) * mm, "end": v(-10, 4) * mm});
            skLineSegment(sketch, "E10.5.0.19", {"start": v(-5, 1) * mm, "end": v(-5, 4) * mm});
            skLineSegment(sketch, "E10.6.0.0", {"start": v(-26, -4) * mm, "end": v(-31, -4) * mm});
            skLineSegment(sketch, "E10.6.0.1", {"start": v(-31, -4) * mm, "end": v(-31, -1) * mm});
            skLineSegment(sketch, "E10.6.0.2", {"start": v(-26, -1) * mm, "end": v(-31, -1) * mm});
            skLineSegment(sketch, "E10.6.0.3", {"start": v(-26, -4) * mm, "end": v(-26, -1) * mm});
            skLineSegment(sketch, "E10.6.0.4", {"start": v(-33, -4) * mm, "end": v(-33, -1) * mm});
            skLineSegment(sketch, "E10.6.0.5", {"start": v(-33, -1) * mm, "end": v(-38, -1) * mm});
            skLineSegment(sketch, "E10.6.0.6", {"start": v(-38, -4) * mm, "end": v(-38, -1) * mm});
            skLineSegment(sketch, "E10.6.0.7", {"start": v(-33, -4) * mm, "end": v(-38, -4) * mm});
            skLineSegment(sketch, "E10.6.0.8", {"start": v(-19, -4) * mm, "end": v(-24, -4) * mm});
            skLineSegment(sketch, "E10.6.0.9", {"start": v(-19, -1) * mm, "end": v(-24, -1) * mm});
            skLineSegment(sketch, "E10.6.0.10", {"start": v(-24, -4) * mm, "end": v(-24, -1) * mm});
            skLineSegment(sketch, "E10.6.0.11", {"start": v(-19, -4) * mm, "end": v(-19, -1) * mm});
            skLineSegment(sketch, "E10.6.0.12", {"start": v(-17, -4) * mm, "end": v(-17, -1) * mm});
            skLineSegment(sketch, "E10.6.0.13", {"start": v(-12, -1) * mm, "end": v(-17, -1) * mm});
            skLineSegment(sketch, "E10.6.0.14", {"start": v(-12, -4) * mm, "end": v(-17, -4) * mm});
            skLineSegment(sketch, "E10.6.0.15", {"start": v(-12, -4) * mm, "end": v(-12, -1) * mm});
            skLineSegment(sketch, "E10.6.0.16", {"start": v(-5, -1) * mm, "end": v(-10, -1) * mm});
            skLineSegment(sketch, "E10.6.0.17", {"start": v(-5, -4) * mm, "end": v(-10, -4) * mm});
            skLineSegment(sketch, "E10.6.0.18", {"start": v(-10, -4) * mm, "end": v(-10, -1) * mm});
            skLineSegment(sketch, "E10.6.0.19", {"start": v(-5, -4) * mm, "end": v(-5, -1) * mm});
            skLineSegment(sketch, "E10.7.0.0", {"start": v(-26, -9) * mm, "end": v(-31, -9) * mm});
            skLineSegment(sketch, "E10.7.0.1", {"start": v(-31, -9) * mm, "end": v(-31, -6) * mm});
            skLineSegment(sketch, "E10.7.0.2", {"start": v(-26, -6) * mm, "end": v(-31, -6) * mm});
            skLineSegment(sketch, "E10.7.0.3", {"start": v(-26, -9) * mm, "end": v(-26, -6) * mm});
            skLineSegment(sketch, "E10.7.0.4", {"start": v(-33, -9) * mm, "end": v(-33, -6) * mm});
            skLineSegment(sketch, "E10.7.0.5", {"start": v(-33, -6) * mm, "end": v(-38, -6) * mm});
            skLineSegment(sketch, "E10.7.0.6", {"start": v(-38, -9) * mm, "end": v(-38, -6) * mm});
            skLineSegment(sketch, "E10.7.0.7", {"start": v(-33, -9) * mm, "end": v(-38, -9) * mm});
            skLineSegment(sketch, "E10.7.0.8", {"start": v(-19, -9) * mm, "end": v(-24, -9) * mm});
            skLineSegment(sketch, "E10.7.0.9", {"start": v(-19, -6) * mm, "end": v(-24, -6) * mm});
            skLineSegment(sketch, "E10.7.0.10", {"start": v(-24, -9) * mm, "end": v(-24, -6) * mm});
            skLineSegment(sketch, "E10.7.0.11", {"start": v(-19, -9) * mm, "end": v(-19, -6) * mm});
            skLineSegment(sketch, "E10.7.0.12", {"start": v(-17, -9) * mm, "end": v(-17, -6) * mm});
            skLineSegment(sketch, "E10.7.0.13", {"start": v(-12, -6) * mm, "end": v(-17, -6) * mm});
            skLineSegment(sketch, "E10.7.0.14", {"start": v(-12, -9) * mm, "end": v(-17, -9) * mm});
            skLineSegment(sketch, "E10.7.0.15", {"start": v(-12, -9) * mm, "end": v(-12, -6) * mm});
            skLineSegment(sketch, "E10.7.0.16", {"start": v(-5, -6) * mm, "end": v(-10, -6) * mm});
            skLineSegment(sketch, "E10.7.0.17", {"start": v(-5, -9) * mm, "end": v(-10, -9) * mm});
            skLineSegment(sketch, "E10.7.0.18", {"start": v(-10, -9) * mm, "end": v(-10, -6) * mm});
            skLineSegment(sketch, "E10.7.0.19", {"start": v(-5, -9) * mm, "end": v(-5, -6) * mm});
            skLineSegment(sketch, "E10.8.0.0", {"start": v(-26, -14) * mm, "end": v(-31, -14) * mm});
            skLineSegment(sketch, "E10.8.0.1", {"start": v(-31, -14) * mm, "end": v(-31, -11) * mm});
            skLineSegment(sketch, "E10.8.0.2", {"start": v(-26, -11) * mm, "end": v(-31, -11) * mm});
            skLineSegment(sketch, "E10.8.0.3", {"start": v(-26, -14) * mm, "end": v(-26, -11) * mm});
            skLineSegment(sketch, "E10.8.0.4", {"start": v(-33, -14) * mm, "end": v(-33, -11) * mm});
            skLineSegment(sketch, "E10.8.0.5", {"start": v(-33, -11) * mm, "end": v(-38, -11) * mm});
            skLineSegment(sketch, "E10.8.0.6", {"start": v(-38, -14) * mm, "end": v(-38, -11) * mm});
            skLineSegment(sketch, "E10.8.0.7", {"start": v(-33, -14) * mm, "end": v(-38, -14) * mm});
            skLineSegment(sketch, "E10.8.0.8", {"start": v(-19, -14) * mm, "end": v(-24, -14) * mm});
            skLineSegment(sketch, "E10.8.0.9", {"start": v(-19, -11) * mm, "end": v(-24, -11) * mm});
            skLineSegment(sketch, "E10.8.0.10", {"start": v(-24, -14) * mm, "end": v(-24, -11) * mm});
            skLineSegment(sketch, "E10.8.0.11", {"start": v(-19, -14) * mm, "end": v(-19, -11) * mm});
            skLineSegment(sketch, "E10.8.0.12", {"start": v(-17, -14) * mm, "end": v(-17, -11) * mm});
            skLineSegment(sketch, "E10.8.0.13", {"start": v(-12, -11) * mm, "end": v(-17, -11) * mm});
            skLineSegment(sketch, "E10.8.0.14", {"start": v(-12, -14) * mm, "end": v(-17, -14) * mm});
            skLineSegment(sketch, "E10.8.0.15", {"start": v(-12, -14) * mm, "end": v(-12, -11) * mm});
            skLineSegment(sketch, "E10.8.0.16", {"start": v(-5, -11) * mm, "end": v(-10, -11) * mm});
            skLineSegment(sketch, "E10.8.0.17", {"start": v(-5, -14) * mm, "end": v(-10, -14) * mm});
            skLineSegment(sketch, "E10.8.0.18", {"start": v(-10, -14) * mm, "end": v(-10, -11) * mm});
            skLineSegment(sketch, "E10.8.0.19", {"start": v(-5, -14) * mm, "end": v(-5, -11) * mm});
            skLineSegment(sketch, "E10.9.0.0", {"start": v(-26, -19) * mm, "end": v(-31, -19) * mm});
            skLineSegment(sketch, "E10.9.0.1", {"start": v(-31, -19) * mm, "end": v(-31, -16) * mm});
            skLineSegment(sketch, "E10.9.0.2", {"start": v(-26, -16) * mm, "end": v(-31, -16) * mm});
            skLineSegment(sketch, "E10.9.0.3", {"start": v(-26, -19) * mm, "end": v(-26, -16) * mm});
            skLineSegment(sketch, "E10.9.0.4", {"start": v(-33, -19) * mm, "end": v(-33, -16) * mm});
            skLineSegment(sketch, "E10.9.0.5", {"start": v(-33, -16) * mm, "end": v(-38, -16) * mm});
            skLineSegment(sketch, "E10.9.0.6", {"start": v(-38, -19) * mm, "end": v(-38, -16) * mm});
            skLineSegment(sketch, "E10.9.0.7", {"start": v(-33, -19) * mm, "end": v(-38, -19) * mm});
            skLineSegment(sketch, "E10.9.0.8", {"start": v(-19, -19) * mm, "end": v(-24, -19) * mm});
            skLineSegment(sketch, "E10.9.0.9", {"start": v(-19, -16) * mm, "end": v(-24, -16) * mm});
            skLineSegment(sketch, "E10.9.0.10", {"start": v(-24, -19) * mm, "end": v(-24, -16) * mm});
            skLineSegment(sketch, "E10.9.0.11", {"start": v(-19, -19) * mm, "end": v(-19, -16) * mm});
            skLineSegment(sketch, "E10.9.0.12", {"start": v(-17, -19) * mm, "end": v(-17, -16) * mm});
            skLineSegment(sketch, "E10.9.0.13", {"start": v(-12, -16) * mm, "end": v(-17, -16) * mm});
            skLineSegment(sketch, "E10.9.0.14", {"start": v(-12, -19) * mm, "end": v(-17, -19) * mm});
            skLineSegment(sketch, "E10.9.0.15", {"start": v(-12, -19) * mm, "end": v(-12, -16) * mm});
            skLineSegment(sketch, "E10.9.0.16", {"start": v(-5, -16) * mm, "end": v(-10, -16) * mm});
            skLineSegment(sketch, "E10.9.0.17", {"start": v(-5, -19) * mm, "end": v(-10, -19) * mm});
            skLineSegment(sketch, "E10.9.0.18", {"start": v(-10, -19) * mm, "end": v(-10, -16) * mm});
            skLineSegment(sketch, "E10.9.0.19", {"start": v(-5, -19) * mm, "end": v(-5, -16) * mm});
            skLineSegment(sketch, "E10.10.0.0", {"start": v(-26, -24) * mm, "end": v(-31, -24) * mm});
            skLineSegment(sketch, "E10.10.0.1", {"start": v(-31, -24) * mm, "end": v(-31, -21) * mm});
            skLineSegment(sketch, "E10.10.0.2", {"start": v(-26, -21) * mm, "end": v(-31, -21) * mm});
            skLineSegment(sketch, "E10.10.0.3", {"start": v(-26, -24) * mm, "end": v(-26, -21) * mm});
            skLineSegment(sketch, "E10.10.0.4", {"start": v(-33, -24) * mm, "end": v(-33, -21) * mm});
            skLineSegment(sketch, "E10.10.0.5", {"start": v(-33, -21) * mm, "end": v(-38, -21) * mm});
            skLineSegment(sketch, "E10.10.0.6", {"start": v(-38, -24) * mm, "end": v(-38, -21) * mm});
            skLineSegment(sketch, "E10.10.0.7", {"start": v(-33, -24) * mm, "end": v(-38, -24) * mm});
            skLineSegment(sketch, "E10.10.0.8", {"start": v(-19, -24) * mm, "end": v(-24, -24) * mm});
            skLineSegment(sketch, "E10.10.0.9", {"start": v(-19, -21) * mm, "end": v(-24, -21) * mm});
            skLineSegment(sketch, "E10.10.0.10", {"start": v(-24, -24) * mm, "end": v(-24, -21) * mm});
            skLineSegment(sketch, "E10.10.0.11", {"start": v(-19, -24) * mm, "end": v(-19, -21) * mm});
            skLineSegment(sketch, "E10.10.0.12", {"start": v(-17, -24) * mm, "end": v(-17, -21) * mm});
            skLineSegment(sketch, "E10.10.0.13", {"start": v(-12, -21) * mm, "end": v(-17, -21) * mm});
            skLineSegment(sketch, "E10.10.0.14", {"start": v(-12, -24) * mm, "end": v(-17, -24) * mm});
            skLineSegment(sketch, "E10.10.0.15", {"start": v(-12, -24) * mm, "end": v(-12, -21) * mm});
            skLineSegment(sketch, "E10.10.0.16", {"start": v(-5, -21) * mm, "end": v(-10, -21) * mm});
            skLineSegment(sketch, "E10.10.0.17", {"start": v(-5, -24) * mm, "end": v(-10, -24) * mm});
            skLineSegment(sketch, "E10.10.0.18", {"start": v(-10, -24) * mm, "end": v(-10, -21) * mm});
            skLineSegment(sketch, "E10.10.0.19", {"start": v(-5, -24) * mm, "end": v(-5, -21) * mm});
            skLineSegment(sketch, "E10.11.0.0", {"start": v(-26, -29) * mm, "end": v(-31, -29) * mm});
            skLineSegment(sketch, "E10.11.0.1", {"start": v(-31, -29) * mm, "end": v(-31, -26) * mm});
            skLineSegment(sketch, "E10.11.0.2", {"start": v(-26, -26) * mm, "end": v(-31, -26) * mm});
            skLineSegment(sketch, "E10.11.0.3", {"start": v(-26, -29) * mm, "end": v(-26, -26) * mm});
            skLineSegment(sketch, "E10.11.0.4", {"start": v(-33, -29) * mm, "end": v(-33, -26) * mm});
            skLineSegment(sketch, "E10.11.0.5", {"start": v(-33, -26) * mm, "end": v(-38, -26) * mm});
            skLineSegment(sketch, "E10.11.0.6", {"start": v(-38, -29) * mm, "end": v(-38, -26) * mm});
            skLineSegment(sketch, "E10.11.0.7", {"start": v(-33, -29) * mm, "end": v(-38, -29) * mm});
            skLineSegment(sketch, "E10.11.0.8", {"start": v(-19, -29) * mm, "end": v(-24, -29) * mm});
            skLineSegment(sketch, "E10.11.0.9", {"start": v(-19, -26) * mm, "end": v(-24, -26) * mm});
            skLineSegment(sketch, "E10.11.0.10", {"start": v(-24, -29) * mm, "end": v(-24, -26) * mm});
            skLineSegment(sketch, "E10.11.0.11", {"start": v(-19, -29) * mm, "end": v(-19, -26) * mm});
            skLineSegment(sketch, "E10.11.0.12", {"start": v(-17, -29) * mm, "end": v(-17, -26) * mm});
            skLineSegment(sketch, "E10.11.0.13", {"start": v(-12, -26) * mm, "end": v(-17, -26) * mm});
            skLineSegment(sketch, "E10.11.0.14", {"start": v(-12, -29) * mm, "end": v(-17, -29) * mm});
            skLineSegment(sketch, "E10.11.0.15", {"start": v(-12, -29) * mm, "end": v(-12, -26) * mm});
            skLineSegment(sketch, "E10.11.0.16", {"start": v(-5, -26) * mm, "end": v(-10, -26) * mm});
            skLineSegment(sketch, "E10.11.0.17", {"start": v(-5, -29) * mm, "end": v(-10, -29) * mm});
            skLineSegment(sketch, "E10.11.0.18", {"start": v(-10, -29) * mm, "end": v(-10, -26) * mm});
            skLineSegment(sketch, "E10.11.0.19", {"start": v(-5, -29) * mm, "end": v(-5, -26) * mm});
            skLineSegment(sketch, "E10.12.0.0", {"start": v(-26, -34) * mm, "end": v(-31, -34) * mm});
            skLineSegment(sketch, "E10.12.0.1", {"start": v(-31, -34) * mm, "end": v(-31, -31) * mm});
            skLineSegment(sketch, "E10.12.0.2", {"start": v(-26, -31) * mm, "end": v(-31, -31) * mm});
            skLineSegment(sketch, "E10.12.0.3", {"start": v(-26, -34) * mm, "end": v(-26, -31) * mm});
            skLineSegment(sketch, "E10.12.0.4", {"start": v(-33, -34) * mm, "end": v(-33, -31) * mm});
            skLineSegment(sketch, "E10.12.0.5", {"start": v(-33, -31) * mm, "end": v(-38, -31) * mm});
            skLineSegment(sketch, "E10.12.0.6", {"start": v(-38, -34) * mm, "end": v(-38, -31) * mm});
            skLineSegment(sketch, "E10.12.0.7", {"start": v(-33, -34) * mm, "end": v(-38, -34) * mm});
            skLineSegment(sketch, "E10.12.0.8", {"start": v(-19, -34) * mm, "end": v(-24, -34) * mm});
            skLineSegment(sketch, "E10.12.0.9", {"start": v(-19, -31) * mm, "end": v(-24, -31) * mm});
            skLineSegment(sketch, "E10.12.0.10", {"start": v(-24, -34) * mm, "end": v(-24, -31) * mm});
            skLineSegment(sketch, "E10.12.0.11", {"start": v(-19, -34) * mm, "end": v(-19, -31) * mm});
            skLineSegment(sketch, "E10.12.0.12", {"start": v(-17, -34) * mm, "end": v(-17, -31) * mm});
            skLineSegment(sketch, "E10.12.0.13", {"start": v(-12, -31) * mm, "end": v(-17, -31) * mm});
            skLineSegment(sketch, "E10.12.0.14", {"start": v(-12, -34) * mm, "end": v(-17, -34) * mm});
            skLineSegment(sketch, "E10.12.0.15", {"start": v(-12, -34) * mm, "end": v(-12, -31) * mm});
            skLineSegment(sketch, "E10.12.0.16", {"start": v(-5, -31) * mm, "end": v(-10, -31) * mm});
            skLineSegment(sketch, "E10.12.0.17", {"start": v(-5, -34) * mm, "end": v(-10, -34) * mm});
            skLineSegment(sketch, "E10.12.0.18", {"start": v(-10, -34) * mm, "end": v(-10, -31) * mm});
            skLineSegment(sketch, "E10.12.0.19", {"start": v(-5, -34) * mm, "end": v(-5, -31) * mm});
            skLineSegment(sketch, "E10.13.0.0", {"start": v(-26, -39) * mm, "end": v(-31, -39) * mm});
            skLineSegment(sketch, "E10.13.0.1", {"start": v(-31, -39) * mm, "end": v(-31, -36) * mm});
            skLineSegment(sketch, "E10.13.0.2", {"start": v(-26, -36) * mm, "end": v(-31, -36) * mm});
            skLineSegment(sketch, "E10.13.0.3", {"start": v(-26, -39) * mm, "end": v(-26, -36) * mm});
            skLineSegment(sketch, "E10.13.0.4", {"start": v(-33, -39) * mm, "end": v(-33, -36) * mm});
            skLineSegment(sketch, "E10.13.0.5", {"start": v(-33, -36) * mm, "end": v(-38, -36) * mm});
            skLineSegment(sketch, "E10.13.0.6", {"start": v(-38, -39) * mm, "end": v(-38, -36) * mm});
            skLineSegment(sketch, "E10.13.0.7", {"start": v(-33, -39) * mm, "end": v(-38, -39) * mm});
            skLineSegment(sketch, "E10.13.0.8", {"start": v(-19, -39) * mm, "end": v(-24, -39) * mm});
            skLineSegment(sketch, "E10.13.0.9", {"start": v(-19, -36) * mm, "end": v(-24, -36) * mm});
            skLineSegment(sketch, "E10.13.0.10", {"start": v(-24, -39) * mm, "end": v(-24, -36) * mm});
            skLineSegment(sketch, "E10.13.0.11", {"start": v(-19, -39) * mm, "end": v(-19, -36) * mm});
            skLineSegment(sketch, "E10.13.0.12", {"start": v(-17, -39) * mm, "end": v(-17, -36) * mm});
            skLineSegment(sketch, "E10.13.0.13", {"start": v(-12, -36) * mm, "end": v(-17, -36) * mm});
            skLineSegment(sketch, "E10.13.0.14", {"start": v(-12, -39) * mm, "end": v(-17, -39) * mm});
            skLineSegment(sketch, "E10.13.0.15", {"start": v(-12, -39) * mm, "end": v(-12, -36) * mm});
            skLineSegment(sketch, "E10.13.0.16", {"start": v(-5, -36) * mm, "end": v(-10, -36) * mm});
            skLineSegment(sketch, "E10.13.0.17", {"start": v(-5, -39) * mm, "end": v(-10, -39) * mm});
            skLineSegment(sketch, "E10.13.0.18", {"start": v(-10, -39) * mm, "end": v(-10, -36) * mm});
            skLineSegment(sketch, "E10.13.0.19", {"start": v(-5, -39) * mm, "end": v(-5, -36) * mm});
            skLineSegment(sketch, "E10.14.0.0", {"start": v(-26, -44) * mm, "end": v(-31, -44) * mm});
            skLineSegment(sketch, "E10.14.0.1", {"start": v(-31, -44) * mm, "end": v(-31, -41) * mm});
            skLineSegment(sketch, "E10.14.0.2", {"start": v(-26, -41) * mm, "end": v(-31, -41) * mm});
            skLineSegment(sketch, "E10.14.0.3", {"start": v(-26, -44) * mm, "end": v(-26, -41) * mm});
            skLineSegment(sketch, "E10.14.0.4", {"start": v(-33, -44) * mm, "end": v(-33, -41) * mm});
            skLineSegment(sketch, "E10.14.0.5", {"start": v(-33, -41) * mm, "end": v(-38, -41) * mm});
            skLineSegment(sketch, "E10.14.0.6", {"start": v(-38, -44) * mm, "end": v(-38, -41) * mm});
            skLineSegment(sketch, "E10.14.0.7", {"start": v(-33, -44) * mm, "end": v(-38, -44) * mm});
            skLineSegment(sketch, "E10.14.0.8", {"start": v(-19, -44) * mm, "end": v(-24, -44) * mm});
            skLineSegment(sketch, "E10.14.0.9", {"start": v(-19, -41) * mm, "end": v(-24, -41) * mm});
            skLineSegment(sketch, "E10.14.0.10", {"start": v(-24, -44) * mm, "end": v(-24, -41) * mm});
            skLineSegment(sketch, "E10.14.0.11", {"start": v(-19, -44) * mm, "end": v(-19, -41) * mm});
            skLineSegment(sketch, "E10.14.0.12", {"start": v(-17, -44) * mm, "end": v(-17, -41) * mm});
            skLineSegment(sketch, "E10.14.0.13", {"start": v(-12, -41) * mm, "end": v(-17, -41) * mm});
            skLineSegment(sketch, "E10.14.0.14", {"start": v(-12, -44) * mm, "end": v(-17, -44) * mm});
            skLineSegment(sketch, "E10.14.0.15", {"start": v(-12, -44) * mm, "end": v(-12, -41) * mm});
            skLineSegment(sketch, "E10.14.0.16", {"start": v(-5, -41) * mm, "end": v(-10, -41) * mm});
            skLineSegment(sketch, "E10.14.0.17", {"start": v(-5, -44) * mm, "end": v(-10, -44) * mm});
            skLineSegment(sketch, "E10.14.0.18", {"start": v(-10, -44) * mm, "end": v(-10, -41) * mm});
            skLineSegment(sketch, "E10.14.0.19", {"start": v(-5, -44) * mm, "end": v(-5, -41) * mm});
            skLineSegment(sketch, "E10.direction1", {"start": v(-38, 26) * mm, "end": v(-38, 21) * mm, "construction": true});
            skLineSegment(sketch, "E11.1.0.0", {"start": v(-3, 21) * mm, "end": v(-3, 24) * mm});
            skLineSegment(sketch, "E11.1.0.1", {"start": v(2, 24) * mm, "end": v(-3, 24) * mm});
            skLineSegment(sketch, "E11.1.0.2", {"start": v(2, 21) * mm, "end": v(-3, 21) * mm});
            skLineSegment(sketch, "E11.1.0.3", {"start": v(2, 21) * mm, "end": v(2, 24) * mm});
            skLineSegment(sketch, "E11.1.0.4", {"start": v(9, 24) * mm, "end": v(4, 24) * mm});
            skLineSegment(sketch, "E11.1.0.5", {"start": v(4, 21) * mm, "end": v(4, 24) * mm});
            skLineSegment(sketch, "E11.1.0.6", {"start": v(9, 21) * mm, "end": v(4, 21) * mm});
            skLineSegment(sketch, "E11.1.0.7", {"start": v(9, 21) * mm, "end": v(9, 24) * mm});
            skLineSegment(sketch, "E11.1.0.8", {"start": v(16, 24) * mm, "end": v(11, 24) * mm});
            skLineSegment(sketch, "E11.1.0.9", {"start": v(11, 21) * mm, "end": v(11, 24) * mm});
            skLineSegment(sketch, "E11.1.0.10", {"start": v(16, 21) * mm, "end": v(11, 21) * mm});
            skLineSegment(sketch, "E11.1.0.11", {"start": v(16, 21) * mm, "end": v(16, 24) * mm});
            skLineSegment(sketch, "E11.1.0.12", {"start": v(18, 21) * mm, "end": v(18, 24) * mm});
            skLineSegment(sketch, "E11.1.0.13", {"start": v(23, 24) * mm, "end": v(18, 24) * mm});
            skLineSegment(sketch, "E11.1.0.14", {"start": v(23, 21) * mm, "end": v(18, 21) * mm});
            skLineSegment(sketch, "E11.1.0.15", {"start": v(23, 21) * mm, "end": v(23, 24) * mm});
            skLineSegment(sketch, "E11.1.0.16", {"start": v(30, 24) * mm, "end": v(25, 24) * mm});
            skLineSegment(sketch, "E11.1.0.17", {"start": v(25, 21) * mm, "end": v(25, 24) * mm});
            skLineSegment(sketch, "E11.1.0.18", {"start": v(30, 21) * mm, "end": v(25, 21) * mm});
            skLineSegment(sketch, "E11.1.0.19", {"start": v(30, 21) * mm, "end": v(30, 24) * mm});
            skLineSegment(sketch, "E11.1.0.20", {"start": v(37, 24) * mm, "end": v(32, 24) * mm});
            skLineSegment(sketch, "E11.1.0.21", {"start": v(37, 21) * mm, "end": v(32, 21) * mm});
            skLineSegment(sketch, "E11.1.0.22", {"start": v(32, 21) * mm, "end": v(32, 24) * mm});
            skLineSegment(sketch, "E11.1.0.23", {"start": v(37, 21) * mm, "end": v(37, 24) * mm});
            skLineSegment(sketch, "E11.1.0.24", {"start": v(44, 24) * mm, "end": v(39, 24) * mm});
            skLineSegment(sketch, "E11.1.0.25", {"start": v(39, 21) * mm, "end": v(39, 24) * mm});
            skLineSegment(sketch, "E11.1.0.26", {"start": v(44, 21) * mm, "end": v(39, 21) * mm});
            skLineSegment(sketch, "E11.1.0.27", {"start": v(44, 21) * mm, "end": v(44, 24) * mm});
            skLineSegment(sketch, "E11.2.0.0", {"start": v(-3, 16) * mm, "end": v(-3, 19) * mm});
            skLineSegment(sketch, "E11.2.0.1", {"start": v(2, 19) * mm, "end": v(-3, 19) * mm});
            skLineSegment(sketch, "E11.2.0.2", {"start": v(2, 16) * mm, "end": v(-3, 16) * mm});
            skLineSegment(sketch, "E11.2.0.3", {"start": v(2, 16) * mm, "end": v(2, 19) * mm});
            skLineSegment(sketch, "E11.2.0.4", {"start": v(9, 19) * mm, "end": v(4, 19) * mm});
            skLineSegment(sketch, "E11.2.0.5", {"start": v(4, 16) * mm, "end": v(4, 19) * mm});
            skLineSegment(sketch, "E11.2.0.6", {"start": v(9, 16) * mm, "end": v(4, 16) * mm});
            skLineSegment(sketch, "E11.2.0.7", {"start": v(9, 16) * mm, "end": v(9, 19) * mm});
            skLineSegment(sketch, "E11.2.0.8", {"start": v(16, 19) * mm, "end": v(11, 19) * mm});
            skLineSegment(sketch, "E11.2.0.9", {"start": v(11, 16) * mm, "end": v(11, 19) * mm});
            skLineSegment(sketch, "E11.2.0.10", {"start": v(16, 16) * mm, "end": v(11, 16) * mm});
            skLineSegment(sketch, "E11.2.0.11", {"start": v(16, 16) * mm, "end": v(16, 19) * mm});
            skLineSegment(sketch, "E11.2.0.12", {"start": v(18, 16) * mm, "end": v(18, 19) * mm});
            skLineSegment(sketch, "E11.2.0.13", {"start": v(23, 19) * mm, "end": v(18, 19) * mm});
            skLineSegment(sketch, "E11.2.0.14", {"start": v(23, 16) * mm, "end": v(18, 16) * mm});
            skLineSegment(sketch, "E11.2.0.15", {"start": v(23, 16) * mm, "end": v(23, 19) * mm});
            skLineSegment(sketch, "E11.2.0.16", {"start": v(30, 19) * mm, "end": v(25, 19) * mm});
            skLineSegment(sketch, "E11.2.0.17", {"start": v(25, 16) * mm, "end": v(25, 19) * mm});
            skLineSegment(sketch, "E11.2.0.18", {"start": v(30, 16) * mm, "end": v(25, 16) * mm});
            skLineSegment(sketch, "E11.2.0.19", {"start": v(30, 16) * mm, "end": v(30, 19) * mm});
            skLineSegment(sketch, "E11.2.0.20", {"start": v(37, 19) * mm, "end": v(32, 19) * mm});
            skLineSegment(sketch, "E11.2.0.21", {"start": v(37, 16) * mm, "end": v(32, 16) * mm});
            skLineSegment(sketch, "E11.2.0.22", {"start": v(32, 16) * mm, "end": v(32, 19) * mm});
            skLineSegment(sketch, "E11.2.0.23", {"start": v(37, 16) * mm, "end": v(37, 19) * mm});
            skLineSegment(sketch, "E11.2.0.24", {"start": v(44, 19) * mm, "end": v(39, 19) * mm});
            skLineSegment(sketch, "E11.2.0.25", {"start": v(39, 16) * mm, "end": v(39, 19) * mm});
            skLineSegment(sketch, "E11.2.0.26", {"start": v(44, 16) * mm, "end": v(39, 16) * mm});
            skLineSegment(sketch, "E11.2.0.27", {"start": v(44, 16) * mm, "end": v(44, 19) * mm});
            skLineSegment(sketch, "E11.3.0.0", {"start": v(-3, 11) * mm, "end": v(-3, 14) * mm});
            skLineSegment(sketch, "E11.3.0.1", {"start": v(2, 14) * mm, "end": v(-3, 14) * mm});
            skLineSegment(sketch, "E11.3.0.2", {"start": v(2, 11) * mm, "end": v(-3, 11) * mm});
            skLineSegment(sketch, "E11.3.0.3", {"start": v(2, 11) * mm, "end": v(2, 14) * mm});
            skLineSegment(sketch, "E11.3.0.4", {"start": v(9, 14) * mm, "end": v(4, 14) * mm});
            skLineSegment(sketch, "E11.3.0.5", {"start": v(4, 11) * mm, "end": v(4, 14) * mm});
            skLineSegment(sketch, "E11.3.0.6", {"start": v(9, 11) * mm, "end": v(4, 11) * mm});
            skLineSegment(sketch, "E11.3.0.7", {"start": v(9, 11) * mm, "end": v(9, 14) * mm});
            skLineSegment(sketch, "E11.3.0.8", {"start": v(16, 14) * mm, "end": v(11, 14) * mm});
            skLineSegment(sketch, "E11.3.0.9", {"start": v(11, 11) * mm, "end": v(11, 14) * mm});
            skLineSegment(sketch, "E11.3.0.10", {"start": v(16, 11) * mm, "end": v(11, 11) * mm});
            skLineSegment(sketch, "E11.3.0.11", {"start": v(16, 11) * mm, "end": v(16, 14) * mm});
            skLineSegment(sketch, "E11.3.0.12", {"start": v(18, 11) * mm, "end": v(18, 14) * mm});
            skLineSegment(sketch, "E11.3.0.13", {"start": v(23, 14) * mm, "end": v(18, 14) * mm});
            skLineSegment(sketch, "E11.3.0.14", {"start": v(23, 11) * mm, "end": v(18, 11) * mm});
            skLineSegment(sketch, "E11.3.0.15", {"start": v(23, 11) * mm, "end": v(23, 14) * mm});
            skLineSegment(sketch, "E11.3.0.16", {"start": v(30, 14) * mm, "end": v(25, 14) * mm});
            skLineSegment(sketch, "E11.3.0.17", {"start": v(25, 11) * mm, "end": v(25, 14) * mm});
            skLineSegment(sketch, "E11.3.0.18", {"start": v(30, 11) * mm, "end": v(25, 11) * mm});
            skLineSegment(sketch, "E11.3.0.19", {"start": v(30, 11) * mm, "end": v(30, 14) * mm});
            skLineSegment(sketch, "E11.3.0.20", {"start": v(37, 14) * mm, "end": v(32, 14) * mm});
            skLineSegment(sketch, "E11.3.0.21", {"start": v(37, 11) * mm, "end": v(32, 11) * mm});
            skLineSegment(sketch, "E11.3.0.22", {"start": v(32, 11) * mm, "end": v(32, 14) * mm});
            skLineSegment(sketch, "E11.3.0.23", {"start": v(37, 11) * mm, "end": v(37, 14) * mm});
            skLineSegment(sketch, "E11.3.0.24", {"start": v(44, 14) * mm, "end": v(39, 14) * mm});
            skLineSegment(sketch, "E11.3.0.25", {"start": v(39, 11) * mm, "end": v(39, 14) * mm});
            skLineSegment(sketch, "E11.3.0.26", {"start": v(44, 11) * mm, "end": v(39, 11) * mm});
            skLineSegment(sketch, "E11.3.0.27", {"start": v(44, 11) * mm, "end": v(44, 14) * mm});
            skLineSegment(sketch, "E11.4.0.0", {"start": v(-3, 6) * mm, "end": v(-3, 9) * mm});
            skLineSegment(sketch, "E11.4.0.1", {"start": v(2, 9) * mm, "end": v(-3, 9) * mm});
            skLineSegment(sketch, "E11.4.0.2", {"start": v(2, 6) * mm, "end": v(-3, 6) * mm});
            skLineSegment(sketch, "E11.4.0.3", {"start": v(2, 6) * mm, "end": v(2, 9) * mm});
            skLineSegment(sketch, "E11.4.0.4", {"start": v(9, 9) * mm, "end": v(4, 9) * mm});
            skLineSegment(sketch, "E11.4.0.5", {"start": v(4, 6) * mm, "end": v(4, 9) * mm});
            skLineSegment(sketch, "E11.4.0.6", {"start": v(9, 6) * mm, "end": v(4, 6) * mm});
            skLineSegment(sketch, "E11.4.0.7", {"start": v(9, 6) * mm, "end": v(9, 9) * mm});
            skLineSegment(sketch, "E11.4.0.8", {"start": v(16, 9) * mm, "end": v(11, 9) * mm});
            skLineSegment(sketch, "E11.4.0.9", {"start": v(11, 6) * mm, "end": v(11, 9) * mm});
            skLineSegment(sketch, "E11.4.0.10", {"start": v(16, 6) * mm, "end": v(11, 6) * mm});
            skLineSegment(sketch, "E11.4.0.11", {"start": v(16, 6) * mm, "end": v(16, 9) * mm});
            skLineSegment(sketch, "E11.4.0.12", {"start": v(18, 6) * mm, "end": v(18, 9) * mm});
            skLineSegment(sketch, "E11.4.0.13", {"start": v(23, 9) * mm, "end": v(18, 9) * mm});
            skLineSegment(sketch, "E11.4.0.14", {"start": v(23, 6) * mm, "end": v(18, 6) * mm});
            skLineSegment(sketch, "E11.4.0.15", {"start": v(23, 6) * mm, "end": v(23, 9) * mm});
            skLineSegment(sketch, "E11.4.0.16", {"start": v(30, 9) * mm, "end": v(25, 9) * mm});
            skLineSegment(sketch, "E11.4.0.17", {"start": v(25, 6) * mm, "end": v(25, 9) * mm});
            skLineSegment(sketch, "E11.4.0.18", {"start": v(30, 6) * mm, "end": v(25, 6) * mm});
            skLineSegment(sketch, "E11.4.0.19", {"start": v(30, 6) * mm, "end": v(30, 9) * mm});
            skLineSegment(sketch, "E11.4.0.20", {"start": v(37, 9) * mm, "end": v(32, 9) * mm});
            skLineSegment(sketch, "E11.4.0.21", {"start": v(37, 6) * mm, "end": v(32, 6) * mm});
            skLineSegment(sketch, "E11.4.0.22", {"start": v(32, 6) * mm, "end": v(32, 9) * mm});
            skLineSegment(sketch, "E11.4.0.23", {"start": v(37, 6) * mm, "end": v(37, 9) * mm});
            skLineSegment(sketch, "E11.4.0.24", {"start": v(44, 9) * mm, "end": v(39, 9) * mm});
            skLineSegment(sketch, "E11.4.0.25", {"start": v(39, 6) * mm, "end": v(39, 9) * mm});
            skLineSegment(sketch, "E11.4.0.26", {"start": v(44, 6) * mm, "end": v(39, 6) * mm});
            skLineSegment(sketch, "E11.4.0.27", {"start": v(44, 6) * mm, "end": v(44, 9) * mm});
            skLineSegment(sketch, "E11.5.0.0", {"start": v(-3, 1) * mm, "end": v(-3, 4) * mm});
            skLineSegment(sketch, "E11.5.0.1", {"start": v(2, 4) * mm, "end": v(-3, 4) * mm});
            skLineSegment(sketch, "E11.5.0.2", {"start": v(2, 1) * mm, "end": v(-3, 1) * mm});
            skLineSegment(sketch, "E11.5.0.3", {"start": v(2, 1) * mm, "end": v(2, 4) * mm});
            skLineSegment(sketch, "E11.5.0.4", {"start": v(9, 4) * mm, "end": v(4, 4) * mm});
            skLineSegment(sketch, "E11.5.0.5", {"start": v(4, 1) * mm, "end": v(4, 4) * mm});
            skLineSegment(sketch, "E11.5.0.6", {"start": v(9, 1) * mm, "end": v(4, 1) * mm});
            skLineSegment(sketch, "E11.5.0.7", {"start": v(9, 1) * mm, "end": v(9, 4) * mm});
            skLineSegment(sketch, "E11.5.0.8", {"start": v(16, 4) * mm, "end": v(11, 4) * mm});
            skLineSegment(sketch, "E11.5.0.9", {"start": v(11, 1) * mm, "end": v(11, 4) * mm});
            skLineSegment(sketch, "E11.5.0.10", {"start": v(16, 1) * mm, "end": v(11, 1) * mm});
            skLineSegment(sketch, "E11.5.0.11", {"start": v(16, 1) * mm, "end": v(16, 4) * mm});
            skLineSegment(sketch, "E11.5.0.12", {"start": v(18, 1) * mm, "end": v(18, 4) * mm});
            skLineSegment(sketch, "E11.5.0.13", {"start": v(23, 4) * mm, "end": v(18, 4) * mm});
            skLineSegment(sketch, "E11.5.0.14", {"start": v(23, 1) * mm, "end": v(18, 1) * mm});
            skLineSegment(sketch, "E11.5.0.15", {"start": v(23, 1) * mm, "end": v(23, 4) * mm});
            skLineSegment(sketch, "E11.5.0.16", {"start": v(30, 4) * mm, "end": v(25, 4) * mm});
            skLineSegment(sketch, "E11.5.0.17", {"start": v(25, 1) * mm, "end": v(25, 4) * mm});
            skLineSegment(sketch, "E11.5.0.18", {"start": v(30, 1) * mm, "end": v(25, 1) * mm});
            skLineSegment(sketch, "E11.5.0.19", {"start": v(30, 1) * mm, "end": v(30, 4) * mm});
            skLineSegment(sketch, "E11.5.0.20", {"start": v(37, 4) * mm, "end": v(32, 4) * mm});
            skLineSegment(sketch, "E11.5.0.21", {"start": v(37, 1) * mm, "end": v(32, 1) * mm});
            skLineSegment(sketch, "E11.5.0.22", {"start": v(32, 1) * mm, "end": v(32, 4) * mm});
            skLineSegment(sketch, "E11.5.0.23", {"start": v(37, 1) * mm, "end": v(37, 4) * mm});
            skLineSegment(sketch, "E11.5.0.24", {"start": v(44, 4) * mm, "end": v(39, 4) * mm});
            skLineSegment(sketch, "E11.5.0.25", {"start": v(39, 1) * mm, "end": v(39, 4) * mm});
            skLineSegment(sketch, "E11.5.0.26", {"start": v(44, 1) * mm, "end": v(39, 1) * mm});
            skLineSegment(sketch, "E11.5.0.27", {"start": v(44, 1) * mm, "end": v(44, 4) * mm});
            skLineSegment(sketch, "E11.6.0.0", {"start": v(-3, -4) * mm, "end": v(-3, -1) * mm});
            skLineSegment(sketch, "E11.6.0.1", {"start": v(2, -1) * mm, "end": v(-3, -1) * mm});
            skLineSegment(sketch, "E11.6.0.2", {"start": v(2, -4) * mm, "end": v(-3, -4) * mm});
            skLineSegment(sketch, "E11.6.0.3", {"start": v(2, -4) * mm, "end": v(2, -1) * mm});
            skLineSegment(sketch, "E11.6.0.4", {"start": v(9, -1) * mm, "end": v(4, -1) * mm});
            skLineSegment(sketch, "E11.6.0.5", {"start": v(4, -4) * mm, "end": v(4, -1) * mm});
            skLineSegment(sketch, "E11.6.0.6", {"start": v(9, -4) * mm, "end": v(4, -4) * mm});
            skLineSegment(sketch, "E11.6.0.7", {"start": v(9, -4) * mm, "end": v(9, -1) * mm});
            skLineSegment(sketch, "E11.6.0.8", {"start": v(16, -1) * mm, "end": v(11, -1) * mm});
            skLineSegment(sketch, "E11.6.0.9", {"start": v(11, -4) * mm, "end": v(11, -1) * mm});
            skLineSegment(sketch, "E11.6.0.10", {"start": v(16, -4) * mm, "end": v(11, -4) * mm});
            skLineSegment(sketch, "E11.6.0.11", {"start": v(16, -4) * mm, "end": v(16, -1) * mm});
            skLineSegment(sketch, "E11.6.0.12", {"start": v(18, -4) * mm, "end": v(18, -1) * mm});
            skLineSegment(sketch, "E11.6.0.13", {"start": v(23, -1) * mm, "end": v(18, -1) * mm});
            skLineSegment(sketch, "E11.6.0.14", {"start": v(23, -4) * mm, "end": v(18, -4) * mm});
            skLineSegment(sketch, "E11.6.0.15", {"start": v(23, -4) * mm, "end": v(23, -1) * mm});
            skLineSegment(sketch, "E11.6.0.16", {"start": v(30, -1) * mm, "end": v(25, -1) * mm});
            skLineSegment(sketch, "E11.6.0.17", {"start": v(25, -4) * mm, "end": v(25, -1) * mm});
            skLineSegment(sketch, "E11.6.0.18", {"start": v(30, -4) * mm, "end": v(25, -4) * mm});
            skLineSegment(sketch, "E11.6.0.19", {"start": v(30, -4) * mm, "end": v(30, -1) * mm});
            skLineSegment(sketch, "E11.6.0.20", {"start": v(37, -1) * mm, "end": v(32, -1) * mm});
            skLineSegment(sketch, "E11.6.0.21", {"start": v(37, -4) * mm, "end": v(32, -4) * mm});
            skLineSegment(sketch, "E11.6.0.22", {"start": v(32, -4) * mm, "end": v(32, -1) * mm});
            skLineSegment(sketch, "E11.6.0.23", {"start": v(37, -4) * mm, "end": v(37, -1) * mm});
            skLineSegment(sketch, "E11.6.0.24", {"start": v(44, -1) * mm, "end": v(39, -1) * mm});
            skLineSegment(sketch, "E11.6.0.25", {"start": v(39, -4) * mm, "end": v(39, -1) * mm});
            skLineSegment(sketch, "E11.6.0.26", {"start": v(44, -4) * mm, "end": v(39, -4) * mm});
            skLineSegment(sketch, "E11.6.0.27", {"start": v(44, -4) * mm, "end": v(44, -1) * mm});
            skLineSegment(sketch, "E11.7.0.0", {"start": v(-3, -9) * mm, "end": v(-3, -6) * mm});
            skLineSegment(sketch, "E11.7.0.1", {"start": v(2, -6) * mm, "end": v(-3, -6) * mm});
            skLineSegment(sketch, "E11.7.0.2", {"start": v(2, -9) * mm, "end": v(-3, -9) * mm});
            skLineSegment(sketch, "E11.7.0.3", {"start": v(2, -9) * mm, "end": v(2, -6) * mm});
            skLineSegment(sketch, "E11.7.0.4", {"start": v(9, -6) * mm, "end": v(4, -6) * mm});
            skLineSegment(sketch, "E11.7.0.5", {"start": v(4, -9) * mm, "end": v(4, -6) * mm});
            skLineSegment(sketch, "E11.7.0.6", {"start": v(9, -9) * mm, "end": v(4, -9) * mm});
            skLineSegment(sketch, "E11.7.0.7", {"start": v(9, -9) * mm, "end": v(9, -6) * mm});
            skLineSegment(sketch, "E11.7.0.8", {"start": v(16, -6) * mm, "end": v(11, -6) * mm});
            skLineSegment(sketch, "E11.7.0.9", {"start": v(11, -9) * mm, "end": v(11, -6) * mm});
            skLineSegment(sketch, "E11.7.0.10", {"start": v(16, -9) * mm, "end": v(11, -9) * mm});
            skLineSegment(sketch, "E11.7.0.11", {"start": v(16, -9) * mm, "end": v(16, -6) * mm});
            skLineSegment(sketch, "E11.7.0.12", {"start": v(18, -9) * mm, "end": v(18, -6) * mm});
            skLineSegment(sketch, "E11.7.0.13", {"start": v(23, -6) * mm, "end": v(18, -6) * mm});
            skLineSegment(sketch, "E11.7.0.14", {"start": v(23, -9) * mm, "end": v(18, -9) * mm});
            skLineSegment(sketch, "E11.7.0.15", {"start": v(23, -9) * mm, "end": v(23, -6) * mm});
            skLineSegment(sketch, "E11.7.0.16", {"start": v(30, -6) * mm, "end": v(25, -6) * mm});
            skLineSegment(sketch, "E11.7.0.17", {"start": v(25, -9) * mm, "end": v(25, -6) * mm});
            skLineSegment(sketch, "E11.7.0.18", {"start": v(30, -9) * mm, "end": v(25, -9) * mm});
            skLineSegment(sketch, "E11.7.0.19", {"start": v(30, -9) * mm, "end": v(30, -6) * mm});
            skLineSegment(sketch, "E11.7.0.20", {"start": v(37, -6) * mm, "end": v(32, -6) * mm});
            skLineSegment(sketch, "E11.7.0.21", {"start": v(37, -9) * mm, "end": v(32, -9) * mm});
            skLineSegment(sketch, "E11.7.0.22", {"start": v(32, -9) * mm, "end": v(32, -6) * mm});
            skLineSegment(sketch, "E11.7.0.23", {"start": v(37, -9) * mm, "end": v(37, -6) * mm});
            skLineSegment(sketch, "E11.7.0.24", {"start": v(44, -6) * mm, "end": v(39, -6) * mm});
            skLineSegment(sketch, "E11.7.0.25", {"start": v(39, -9) * mm, "end": v(39, -6) * mm});
            skLineSegment(sketch, "E11.7.0.26", {"start": v(44, -9) * mm, "end": v(39, -9) * mm});
            skLineSegment(sketch, "E11.7.0.27", {"start": v(44, -9) * mm, "end": v(44, -6) * mm});
            skLineSegment(sketch, "E11.8.0.0", {"start": v(-3, -14) * mm, "end": v(-3, -11) * mm});
            skLineSegment(sketch, "E11.8.0.1", {"start": v(2, -11) * mm, "end": v(-3, -11) * mm});
            skLineSegment(sketch, "E11.8.0.2", {"start": v(2, -14) * mm, "end": v(-3, -14) * mm});
            skLineSegment(sketch, "E11.8.0.3", {"start": v(2, -14) * mm, "end": v(2, -11) * mm});
            skLineSegment(sketch, "E11.8.0.4", {"start": v(9, -11) * mm, "end": v(4, -11) * mm});
            skLineSegment(sketch, "E11.8.0.5", {"start": v(4, -14) * mm, "end": v(4, -11) * mm});
            skLineSegment(sketch, "E11.8.0.6", {"start": v(9, -14) * mm, "end": v(4, -14) * mm});
            skLineSegment(sketch, "E11.8.0.7", {"start": v(9, -14) * mm, "end": v(9, -11) * mm});
            skLineSegment(sketch, "E11.8.0.8", {"start": v(16, -11) * mm, "end": v(11, -11) * mm});
            skLineSegment(sketch, "E11.8.0.9", {"start": v(11, -14) * mm, "end": v(11, -11) * mm});
            skLineSegment(sketch, "E11.8.0.10", {"start": v(16, -14) * mm, "end": v(11, -14) * mm});
            skLineSegment(sketch, "E11.8.0.11", {"start": v(16, -14) * mm, "end": v(16, -11) * mm});
            skLineSegment(sketch, "E11.8.0.12", {"start": v(18, -14) * mm, "end": v(18, -11) * mm});
            skLineSegment(sketch, "E11.8.0.13", {"start": v(23, -11) * mm, "end": v(18, -11) * mm});
            skLineSegment(sketch, "E11.8.0.14", {"start": v(23, -14) * mm, "end": v(18, -14) * mm});
            skLineSegment(sketch, "E11.8.0.15", {"start": v(23, -14) * mm, "end": v(23, -11) * mm});
            skLineSegment(sketch, "E11.8.0.16", {"start": v(30, -11) * mm, "end": v(25, -11) * mm});
            skLineSegment(sketch, "E11.8.0.17", {"start": v(25, -14) * mm, "end": v(25, -11) * mm});
            skLineSegment(sketch, "E11.8.0.18", {"start": v(30, -14) * mm, "end": v(25, -14) * mm});
            skLineSegment(sketch, "E11.8.0.19", {"start": v(30, -14) * mm, "end": v(30, -11) * mm});
            skLineSegment(sketch, "E11.8.0.20", {"start": v(37, -11) * mm, "end": v(32, -11) * mm});
            skLineSegment(sketch, "E11.8.0.21", {"start": v(37, -14) * mm, "end": v(32, -14) * mm});
            skLineSegment(sketch, "E11.8.0.22", {"start": v(32, -14) * mm, "end": v(32, -11) * mm});
            skLineSegment(sketch, "E11.8.0.23", {"start": v(37, -14) * mm, "end": v(37, -11) * mm});
            skLineSegment(sketch, "E11.8.0.24", {"start": v(44, -11) * mm, "end": v(39, -11) * mm});
            skLineSegment(sketch, "E11.8.0.25", {"start": v(39, -14) * mm, "end": v(39, -11) * mm});
            skLineSegment(sketch, "E11.8.0.26", {"start": v(44, -14) * mm, "end": v(39, -14) * mm});
            skLineSegment(sketch, "E11.8.0.27", {"start": v(44, -14) * mm, "end": v(44, -11) * mm});
            skLineSegment(sketch, "E11.9.0.0", {"start": v(-3, -19) * mm, "end": v(-3, -16) * mm});
            skLineSegment(sketch, "E11.9.0.1", {"start": v(2, -16) * mm, "end": v(-3, -16) * mm});
            skLineSegment(sketch, "E11.9.0.2", {"start": v(2, -19) * mm, "end": v(-3, -19) * mm});
            skLineSegment(sketch, "E11.9.0.3", {"start": v(2, -19) * mm, "end": v(2, -16) * mm});
            skLineSegment(sketch, "E11.9.0.4", {"start": v(9, -16) * mm, "end": v(4, -16) * mm});
            skLineSegment(sketch, "E11.9.0.5", {"start": v(4, -19) * mm, "end": v(4, -16) * mm});
            skLineSegment(sketch, "E11.9.0.6", {"start": v(9, -19) * mm, "end": v(4, -19) * mm});
            skLineSegment(sketch, "E11.9.0.7", {"start": v(9, -19) * mm, "end": v(9, -16) * mm});
            skLineSegment(sketch, "E11.9.0.8", {"start": v(16, -16) * mm, "end": v(11, -16) * mm});
            skLineSegment(sketch, "E11.9.0.9", {"start": v(11, -19) * mm, "end": v(11, -16) * mm});
            skLineSegment(sketch, "E11.9.0.10", {"start": v(16, -19) * mm, "end": v(11, -19) * mm});
            skLineSegment(sketch, "E11.9.0.11", {"start": v(16, -19) * mm, "end": v(16, -16) * mm});
            skLineSegment(sketch, "E11.9.0.12", {"start": v(18, -19) * mm, "end": v(18, -16) * mm});
            skLineSegment(sketch, "E11.9.0.13", {"start": v(23, -16) * mm, "end": v(18, -16) * mm});
            skLineSegment(sketch, "E11.9.0.14", {"start": v(23, -19) * mm, "end": v(18, -19) * mm});
            skLineSegment(sketch, "E11.9.0.15", {"start": v(23, -19) * mm, "end": v(23, -16) * mm});
            skLineSegment(sketch, "E11.9.0.16", {"start": v(30, -16) * mm, "end": v(25, -16) * mm});
            skLineSegment(sketch, "E11.9.0.17", {"start": v(25, -19) * mm, "end": v(25, -16) * mm});
            skLineSegment(sketch, "E11.9.0.18", {"start": v(30, -19) * mm, "end": v(25, -19) * mm});
            skLineSegment(sketch, "E11.9.0.19", {"start": v(30, -19) * mm, "end": v(30, -16) * mm});
            skLineSegment(sketch, "E11.9.0.20", {"start": v(37, -16) * mm, "end": v(32, -16) * mm});
            skLineSegment(sketch, "E11.9.0.21", {"start": v(37, -19) * mm, "end": v(32, -19) * mm});
            skLineSegment(sketch, "E11.9.0.22", {"start": v(32, -19) * mm, "end": v(32, -16) * mm});
            skLineSegment(sketch, "E11.9.0.23", {"start": v(37, -19) * mm, "end": v(37, -16) * mm});
            skLineSegment(sketch, "E11.9.0.24", {"start": v(44, -16) * mm, "end": v(39, -16) * mm});
            skLineSegment(sketch, "E11.9.0.25", {"start": v(39, -19) * mm, "end": v(39, -16) * mm});
            skLineSegment(sketch, "E11.9.0.26", {"start": v(44, -19) * mm, "end": v(39, -19) * mm});
            skLineSegment(sketch, "E11.9.0.27", {"start": v(44, -19) * mm, "end": v(44, -16) * mm});
            skLineSegment(sketch, "E11.10.0.0", {"start": v(-3, -24) * mm, "end": v(-3, -21) * mm});
            skLineSegment(sketch, "E11.10.0.1", {"start": v(2, -21) * mm, "end": v(-3, -21) * mm});
            skLineSegment(sketch, "E11.10.0.2", {"start": v(2, -24) * mm, "end": v(-3, -24) * mm});
            skLineSegment(sketch, "E11.10.0.3", {"start": v(2, -24) * mm, "end": v(2, -21) * mm});
            skLineSegment(sketch, "E11.10.0.4", {"start": v(9, -21) * mm, "end": v(4, -21) * mm});
            skLineSegment(sketch, "E11.10.0.5", {"start": v(4, -24) * mm, "end": v(4, -21) * mm});
            skLineSegment(sketch, "E11.10.0.6", {"start": v(9, -24) * mm, "end": v(4, -24) * mm});
            skLineSegment(sketch, "E11.10.0.7", {"start": v(9, -24) * mm, "end": v(9, -21) * mm});
            skLineSegment(sketch, "E11.10.0.8", {"start": v(16, -21) * mm, "end": v(11, -21) * mm});
            skLineSegment(sketch, "E11.10.0.9", {"start": v(11, -24) * mm, "end": v(11, -21) * mm});
            skLineSegment(sketch, "E11.10.0.10", {"start": v(16, -24) * mm, "end": v(11, -24) * mm});
            skLineSegment(sketch, "E11.10.0.11", {"start": v(16, -24) * mm, "end": v(16, -21) * mm});
            skLineSegment(sketch, "E11.10.0.12", {"start": v(18, -24) * mm, "end": v(18, -21) * mm});
            skLineSegment(sketch, "E11.10.0.13", {"start": v(23, -21) * mm, "end": v(18, -21) * mm});
            skLineSegment(sketch, "E11.10.0.14", {"start": v(23, -24) * mm, "end": v(18, -24) * mm});
            skLineSegment(sketch, "E11.10.0.15", {"start": v(23, -24) * mm, "end": v(23, -21) * mm});
            skLineSegment(sketch, "E11.10.0.16", {"start": v(30, -21) * mm, "end": v(25, -21) * mm});
            skLineSegment(sketch, "E11.10.0.17", {"start": v(25, -24) * mm, "end": v(25, -21) * mm});
            skLineSegment(sketch, "E11.10.0.18", {"start": v(30, -24) * mm, "end": v(25, -24) * mm});
            skLineSegment(sketch, "E11.10.0.19", {"start": v(30, -24) * mm, "end": v(30, -21) * mm});
            skLineSegment(sketch, "E11.10.0.20", {"start": v(37, -21) * mm, "end": v(32, -21) * mm});
            skLineSegment(sketch, "E11.10.0.21", {"start": v(37, -24) * mm, "end": v(32, -24) * mm});
            skLineSegment(sketch, "E11.10.0.22", {"start": v(32, -24) * mm, "end": v(32, -21) * mm});
            skLineSegment(sketch, "E11.10.0.23", {"start": v(37, -24) * mm, "end": v(37, -21) * mm});
            skLineSegment(sketch, "E11.10.0.24", {"start": v(44, -21) * mm, "end": v(39, -21) * mm});
            skLineSegment(sketch, "E11.10.0.25", {"start": v(39, -24) * mm, "end": v(39, -21) * mm});
            skLineSegment(sketch, "E11.10.0.26", {"start": v(44, -24) * mm, "end": v(39, -24) * mm});
            skLineSegment(sketch, "E11.10.0.27", {"start": v(44, -24) * mm, "end": v(44, -21) * mm});
            skLineSegment(sketch, "E11.11.0.0", {"start": v(-3, -29) * mm, "end": v(-3, -26) * mm});
            skLineSegment(sketch, "E11.11.0.1", {"start": v(2, -26) * mm, "end": v(-3, -26) * mm});
            skLineSegment(sketch, "E11.11.0.2", {"start": v(2, -29) * mm, "end": v(-3, -29) * mm});
            skLineSegment(sketch, "E11.11.0.3", {"start": v(2, -29) * mm, "end": v(2, -26) * mm});
            skLineSegment(sketch, "E11.11.0.4", {"start": v(9, -26) * mm, "end": v(4, -26) * mm});
            skLineSegment(sketch, "E11.11.0.5", {"start": v(4, -29) * mm, "end": v(4, -26) * mm});
            skLineSegment(sketch, "E11.11.0.6", {"start": v(9, -29) * mm, "end": v(4, -29) * mm});
            skLineSegment(sketch, "E11.11.0.7", {"start": v(9, -29) * mm, "end": v(9, -26) * mm});
            skLineSegment(sketch, "E11.11.0.8", {"start": v(16, -26) * mm, "end": v(11, -26) * mm});
            skLineSegment(sketch, "E11.11.0.9", {"start": v(11, -29) * mm, "end": v(11, -26) * mm});
            skLineSegment(sketch, "E11.11.0.10", {"start": v(16, -29) * mm, "end": v(11, -29) * mm});
            skLineSegment(sketch, "E11.11.0.11", {"start": v(16, -29) * mm, "end": v(16, -26) * mm});
            skLineSegment(sketch, "E11.11.0.12", {"start": v(18, -29) * mm, "end": v(18, -26) * mm});
            skLineSegment(sketch, "E11.11.0.13", {"start": v(23, -26) * mm, "end": v(18, -26) * mm});
            skLineSegment(sketch, "E11.11.0.14", {"start": v(23, -29) * mm, "end": v(18, -29) * mm});
            skLineSegment(sketch, "E11.11.0.15", {"start": v(23, -29) * mm, "end": v(23, -26) * mm});
            skLineSegment(sketch, "E11.11.0.16", {"start": v(30, -26) * mm, "end": v(25, -26) * mm});
            skLineSegment(sketch, "E11.11.0.17", {"start": v(25, -29) * mm, "end": v(25, -26) * mm});
            skLineSegment(sketch, "E11.11.0.18", {"start": v(30, -29) * mm, "end": v(25, -29) * mm});
            skLineSegment(sketch, "E11.11.0.19", {"start": v(30, -29) * mm, "end": v(30, -26) * mm});
            skLineSegment(sketch, "E11.11.0.20", {"start": v(37, -26) * mm, "end": v(32, -26) * mm});
            skLineSegment(sketch, "E11.11.0.21", {"start": v(37, -29) * mm, "end": v(32, -29) * mm});
            skLineSegment(sketch, "E11.11.0.22", {"start": v(32, -29) * mm, "end": v(32, -26) * mm});
            skLineSegment(sketch, "E11.11.0.23", {"start": v(37, -29) * mm, "end": v(37, -26) * mm});
            skLineSegment(sketch, "E11.11.0.24", {"start": v(44, -26) * mm, "end": v(39, -26) * mm});
            skLineSegment(sketch, "E11.11.0.25", {"start": v(39, -29) * mm, "end": v(39, -26) * mm});
            skLineSegment(sketch, "E11.11.0.26", {"start": v(44, -29) * mm, "end": v(39, -29) * mm});
            skLineSegment(sketch, "E11.11.0.27", {"start": v(44, -29) * mm, "end": v(44, -26) * mm});
            skLineSegment(sketch, "E11.12.0.0", {"start": v(-3, -34) * mm, "end": v(-3, -31) * mm});
            skLineSegment(sketch, "E11.12.0.1", {"start": v(2, -31) * mm, "end": v(-3, -31) * mm});
            skLineSegment(sketch, "E11.12.0.2", {"start": v(2, -34) * mm, "end": v(-3, -34) * mm});
            skLineSegment(sketch, "E11.12.0.3", {"start": v(2, -34) * mm, "end": v(2, -31) * mm});
            skLineSegment(sketch, "E11.12.0.4", {"start": v(9, -31) * mm, "end": v(4, -31) * mm});
            skLineSegment(sketch, "E11.12.0.5", {"start": v(4, -34) * mm, "end": v(4, -31) * mm});
            skLineSegment(sketch, "E11.12.0.6", {"start": v(9, -34) * mm, "end": v(4, -34) * mm});
            skLineSegment(sketch, "E11.12.0.7", {"start": v(9, -34) * mm, "end": v(9, -31) * mm});
            skLineSegment(sketch, "E11.12.0.8", {"start": v(16, -31) * mm, "end": v(11, -31) * mm});
            skLineSegment(sketch, "E11.12.0.9", {"start": v(11, -34) * mm, "end": v(11, -31) * mm});
            skLineSegment(sketch, "E11.12.0.10", {"start": v(16, -34) * mm, "end": v(11, -34) * mm});
            skLineSegment(sketch, "E11.12.0.11", {"start": v(16, -34) * mm, "end": v(16, -31) * mm});
            skLineSegment(sketch, "E11.12.0.12", {"start": v(18, -34) * mm, "end": v(18, -31) * mm});
            skLineSegment(sketch, "E11.12.0.13", {"start": v(23, -31) * mm, "end": v(18, -31) * mm});
            skLineSegment(sketch, "E11.12.0.14", {"start": v(23, -34) * mm, "end": v(18, -34) * mm});
            skLineSegment(sketch, "E11.12.0.15", {"start": v(23, -34) * mm, "end": v(23, -31) * mm});
            skLineSegment(sketch, "E11.12.0.16", {"start": v(30, -31) * mm, "end": v(25, -31) * mm});
            skLineSegment(sketch, "E11.12.0.17", {"start": v(25, -34) * mm, "end": v(25, -31) * mm});
            skLineSegment(sketch, "E11.12.0.18", {"start": v(30, -34) * mm, "end": v(25, -34) * mm});
            skLineSegment(sketch, "E11.12.0.19", {"start": v(30, -34) * mm, "end": v(30, -31) * mm});
            skLineSegment(sketch, "E11.12.0.20", {"start": v(37, -31) * mm, "end": v(32, -31) * mm});
            skLineSegment(sketch, "E11.12.0.21", {"start": v(37, -34) * mm, "end": v(32, -34) * mm});
            skLineSegment(sketch, "E11.12.0.22", {"start": v(32, -34) * mm, "end": v(32, -31) * mm});
            skLineSegment(sketch, "E11.12.0.23", {"start": v(37, -34) * mm, "end": v(37, -31) * mm});
            skLineSegment(sketch, "E11.12.0.24", {"start": v(44, -31) * mm, "end": v(39, -31) * mm});
            skLineSegment(sketch, "E11.12.0.25", {"start": v(39, -34) * mm, "end": v(39, -31) * mm});
            skLineSegment(sketch, "E11.12.0.26", {"start": v(44, -34) * mm, "end": v(39, -34) * mm});
            skLineSegment(sketch, "E11.12.0.27", {"start": v(44, -34) * mm, "end": v(44, -31) * mm});
            skLineSegment(sketch, "E11.13.0.0", {"start": v(-3, -39) * mm, "end": v(-3, -36) * mm});
            skLineSegment(sketch, "E11.13.0.1", {"start": v(2, -36) * mm, "end": v(-3, -36) * mm});
            skLineSegment(sketch, "E11.13.0.2", {"start": v(2, -39) * mm, "end": v(-3, -39) * mm});
            skLineSegment(sketch, "E11.13.0.3", {"start": v(2, -39) * mm, "end": v(2, -36) * mm});
            skLineSegment(sketch, "E11.13.0.4", {"start": v(9, -36) * mm, "end": v(4, -36) * mm});
            skLineSegment(sketch, "E11.13.0.5", {"start": v(4, -39) * mm, "end": v(4, -36) * mm});
            skLineSegment(sketch, "E11.13.0.6", {"start": v(9, -39) * mm, "end": v(4, -39) * mm});
            skLineSegment(sketch, "E11.13.0.7", {"start": v(9, -39) * mm, "end": v(9, -36) * mm});
            skLineSegment(sketch, "E11.13.0.8", {"start": v(16, -36) * mm, "end": v(11, -36) * mm});
            skLineSegment(sketch, "E11.13.0.9", {"start": v(11, -39) * mm, "end": v(11, -36) * mm});
            skLineSegment(sketch, "E11.13.0.10", {"start": v(16, -39) * mm, "end": v(11, -39) * mm});
            skLineSegment(sketch, "E11.13.0.11", {"start": v(16, -39) * mm, "end": v(16, -36) * mm});
            skLineSegment(sketch, "E11.13.0.12", {"start": v(18, -39) * mm, "end": v(18, -36) * mm});
            skLineSegment(sketch, "E11.13.0.13", {"start": v(23, -36) * mm, "end": v(18, -36) * mm});
            skLineSegment(sketch, "E11.13.0.14", {"start": v(23, -39) * mm, "end": v(18, -39) * mm});
            skLineSegment(sketch, "E11.13.0.15", {"start": v(23, -39) * mm, "end": v(23, -36) * mm});
            skLineSegment(sketch, "E11.13.0.16", {"start": v(30, -36) * mm, "end": v(25, -36) * mm});
            skLineSegment(sketch, "E11.13.0.17", {"start": v(25, -39) * mm, "end": v(25, -36) * mm});
            skLineSegment(sketch, "E11.13.0.18", {"start": v(30, -39) * mm, "end": v(25, -39) * mm});
            skLineSegment(sketch, "E11.13.0.19", {"start": v(30, -39) * mm, "end": v(30, -36) * mm});
            skLineSegment(sketch, "E11.13.0.20", {"start": v(37, -36) * mm, "end": v(32, -36) * mm});
            skLineSegment(sketch, "E11.13.0.21", {"start": v(37, -39) * mm, "end": v(32, -39) * mm});
            skLineSegment(sketch, "E11.13.0.22", {"start": v(32, -39) * mm, "end": v(32, -36) * mm});
            skLineSegment(sketch, "E11.13.0.23", {"start": v(37, -39) * mm, "end": v(37, -36) * mm});
            skLineSegment(sketch, "E11.13.0.24", {"start": v(44, -36) * mm, "end": v(39, -36) * mm});
            skLineSegment(sketch, "E11.13.0.25", {"start": v(39, -39) * mm, "end": v(39, -36) * mm});
            skLineSegment(sketch, "E11.13.0.26", {"start": v(44, -39) * mm, "end": v(39, -39) * mm});
            skLineSegment(sketch, "E11.13.0.27", {"start": v(44, -39) * mm, "end": v(44, -36) * mm});
            skLineSegment(sketch, "E11.14.0.0", {"start": v(-3, -44) * mm, "end": v(-3, -41) * mm});
            skLineSegment(sketch, "E11.14.0.1", {"start": v(2, -41) * mm, "end": v(-3, -41) * mm});
            skLineSegment(sketch, "E11.14.0.2", {"start": v(2, -44) * mm, "end": v(-3, -44) * mm});
            skLineSegment(sketch, "E11.14.0.3", {"start": v(2, -44) * mm, "end": v(2, -41) * mm});
            skLineSegment(sketch, "E11.14.0.4", {"start": v(9, -41) * mm, "end": v(4, -41) * mm});
            skLineSegment(sketch, "E11.14.0.5", {"start": v(4, -44) * mm, "end": v(4, -41) * mm});
            skLineSegment(sketch, "E11.14.0.6", {"start": v(9, -44) * mm, "end": v(4, -44) * mm});
            skLineSegment(sketch, "E11.14.0.7", {"start": v(9, -44) * mm, "end": v(9, -41) * mm});
            skLineSegment(sketch, "E11.14.0.8", {"start": v(16, -41) * mm, "end": v(11, -41) * mm});
            skLineSegment(sketch, "E11.14.0.9", {"start": v(11, -44) * mm, "end": v(11, -41) * mm});
            skLineSegment(sketch, "E11.14.0.10", {"start": v(16, -44) * mm, "end": v(11, -44) * mm});
            skLineSegment(sketch, "E11.14.0.11", {"start": v(16, -44) * mm, "end": v(16, -41) * mm});
            skLineSegment(sketch, "E11.14.0.12", {"start": v(18, -44) * mm, "end": v(18, -41) * mm});
            skLineSegment(sketch, "E11.14.0.13", {"start": v(23, -41) * mm, "end": v(18, -41) * mm});
            skLineSegment(sketch, "E11.14.0.14", {"start": v(23, -44) * mm, "end": v(18, -44) * mm});
            skLineSegment(sketch, "E11.14.0.15", {"start": v(23, -44) * mm, "end": v(23, -41) * mm});
            skLineSegment(sketch, "E11.14.0.16", {"start": v(30, -41) * mm, "end": v(25, -41) * mm});
            skLineSegment(sketch, "E11.14.0.17", {"start": v(25, -44) * mm, "end": v(25, -41) * mm});
            skLineSegment(sketch, "E11.14.0.18", {"start": v(30, -44) * mm, "end": v(25, -44) * mm});
            skLineSegment(sketch, "E11.14.0.19", {"start": v(30, -44) * mm, "end": v(30, -41) * mm});
            skLineSegment(sketch, "E11.14.0.20", {"start": v(37, -41) * mm, "end": v(32, -41) * mm});
            skLineSegment(sketch, "E11.14.0.21", {"start": v(37, -44) * mm, "end": v(32, -44) * mm});
            skLineSegment(sketch, "E11.14.0.22", {"start": v(32, -44) * mm, "end": v(32, -41) * mm});
            skLineSegment(sketch, "E11.14.0.23", {"start": v(37, -44) * mm, "end": v(37, -41) * mm});
            skLineSegment(sketch, "E11.14.0.24", {"start": v(44, -41) * mm, "end": v(39, -41) * mm});
            skLineSegment(sketch, "E11.14.0.25", {"start": v(39, -44) * mm, "end": v(39, -41) * mm});
            skLineSegment(sketch, "E11.14.0.26", {"start": v(44, -44) * mm, "end": v(39, -44) * mm});
            skLineSegment(sketch, "E11.14.0.27", {"start": v(44, -44) * mm, "end": v(44, -41) * mm});
            skLineSegment(sketch, "E11.direction1", {"start": v(-3, 26) * mm, "end": v(-3, 21) * mm, "construction": true});
            skSolve(sketch);
        }
        {
            var Q0;
            Q0 = qSketchRegion(id + "F0", true);
            extrude(context, id + "F1", {"entities" : qUnion([Q0]), "depth" : 3.05 * mm, "offsetDistance" : 25.4 * mm});
        }
        {
            var Q0;
            Q0=qCreatedBy(makeId("Top.planeOp"),FACE);
            var sketch = newSketch(context, id + "F2", { "sketchPlane" : qUnion([Q0])});
            skEllipse(sketch, "E12", {"center": v(21, 0) * mm, "majorRadius": 10.5 * mm, "minorRadius": 8.75 * mm, "majorAxis": v(-1, 0)});
            skSolve(sketch);
        }
        {
            var Q0;
            Q0 = qSketchRegion(id + "F2", true);
            extrude(context, id + "F3", {"entities" : qUnion([Q0]), "operationType" : NewBodyOperationType.REMOVE, "depth" : 4 * mm, "offsetDistance" : 25 * mm});
        }
        {
            var Q0;
            Q0=makeQuery(id+"F1.opExtrude","CAP_FACE",FACE,{"disambiguationData":[OSD([sQuery(id+"F0.wireOp",EDGE,"E0.bottom"),sQuery(id+"F0.wireOp",EDGE,"E0.top"),sQuery(id+"F0.wireOp",EDGE,"E0.left"),sQuery(id+"F0.wireOp",EDGE,"E0.right"),sQuery(id+"F0.wireOp",EDGE,"E1.bottom"),sQuery(id+"F0.wireOp",EDGE,"E1.left"),sQuery(id+"F0.wireOp",EDGE,"E2.bottom"),sQuery(id+"F0.wireOp",EDGE,"E2.top"),sQuery(id+"F0.wireOp",EDGE,"E2.left"),sQuery(id+"F0.wireOp",EDGE,"E2.right"),sQuery(id+"F0.wireOp",EDGE,"E3.1.0.0"),sQuery(id+"F0.wireOp",EDGE,"E3.1.0.1"),sQuery(id+"F0.wireOp",EDGE,"E3.1.0.2"),sQuery(id+"F0.wireOp",EDGE,"E3.1.0.3"),sQuery(id+"F0.wireOp",EDGE,"E3.2.0.0"),sQuery(id+"F0.wireOp",EDGE,"E3.2.0.1"),sQuery(id+"F0.wireOp",EDGE,"E3.2.0.2"),sQuery(id+"F0.wireOp",EDGE,"E3.2.0.3"),sQuery(id+"F0.wireOp",EDGE,"E3.3.0.0"),sQuery(id+"F0.wireOp",EDGE,"E3.3.0.1"),sQuery(id+"F0.wireOp",EDGE,"E3.3.0.2"),sQuery(id+"F0.wireOp",EDGE,"E3.3.0.3"),sQuery(id+"F0.wireOp",EDGE,"E3.4.0.0"),sQuery(id+"F0.wireOp",EDGE,"E3.4.0.1"),sQuery(id+"F0.wireOp",EDGE,"E3.4.0.2"),sQuery(id+"F0.wireOp",EDGE,"E3.4.0.3"),sQuery(id+"F0.wireOp",EDGE,"E3.5.0.0"),sQuery(id+"F0.wireOp",EDGE,"E3.5.0.1"),sQuery(id+"F0.wireOp",EDGE,"E3.5.0.2"),sQuery(id+"F0.wireOp",EDGE,"E3.5.0.3"),sQuery(id+"F0.wireOp",EDGE,"E3.6.0.0"),sQuery(id+"F0.wireOp",EDGE,"E3.6.0.1"),sQuery(id+"F0.wireOp",EDGE,"E3.6.0.2"),sQuery(id+"F0.wireOp",EDGE,"E3.6.0.3"),sQuery(id+"F0.wireOp",EDGE,"E3.7.0.0"),sQuery(id+"F0.wireOp",EDGE,"E3.7.0.1"),sQuery(id+"F0.wireOp",EDGE,"E3.7.0.2"),sQuery(id+"F0.wireOp",EDGE,"E3.7.0.3"),sQuery(id+"F0.wireOp",EDGE,"E3.8.0.0"),sQuery(id+"F0.wireOp",EDGE,"E3.8.0.1"),sQuery(id+"F0.wireOp",EDGE,"E3.8.0.2"),sQuery(id+"F0.wireOp",EDGE,"E3.8.0.3"),sQuery(id+"F0.wireOp",EDGE,"E3.9.0.0"),sQuery(id+"F0.wireOp",EDGE,"E3.9.0.1"),sQuery(id+"F0.wireOp",EDGE,"E3.9.0.2"),sQuery(id+"F0.wireOp",EDGE,"E3.9.0.3"),sQuery(id+"F0.wireOp",EDGE,"E3.10.0.0"),sQuery(id+"F0.wireOp",EDGE,"E3.10.0.1"),sQuery(id+"F0.wireOp",EDGE,"E3.10.0.2"),sQuery(id+"F0.wireOp",EDGE,"E3.10.0.3"),sQuery(id+"F0.wireOp",EDGE,"E4.0.11.0"),sQuery(id+"F0.wireOp",EDGE,"E4.3.11.0"),sQuery(id+"F0.wireOp",EDGE,"E4.6.11.0"),sQuery(id+"F0.wireOp",EDGE,"E4.9.11.0"),sQuery(id+"F0.wireOp",EDGE,"E5.0.12.0"),sQuery(id+"F0.wireOp",EDGE,"E5.3.12.0"),sQuery(id+"F0.wireOp",EDGE,"E5.6.12.0"),sQuery(id+"F0.wireOp",EDGE,"E5.9.12.0"),sQuery(id+"F0.wireOp",EDGE,"E6.1.0.0"),sQuery(id+"F0.wireOp",EDGE,"E6.1.0.1"),sQuery(id+"F0.wireOp",EDGE,"E6.1.0.2"),sQuery(id+"F0.wireOp",EDGE,"E6.1.0.3"),sQuery(id+"F0.wireOp",EDGE,"E6.2.0.0"),sQuery(id+"F0.wireOp",EDGE,"E6.2.0.1"),sQuery(id+"F0.wireOp",EDGE,"E6.2.0.2"),sQuery(id+"F0.wireOp",EDGE,"E6.2.0.3"),sQuery(id+"F0.wireOp",EDGE,"E6.3.0.0"),sQuery(id+"F0.wireOp",EDGE,"E6.3.0.1"),sQuery(id+"F0.wireOp",EDGE,"E6.3.0.2"),sQuery(id+"F0.wireOp",EDGE,"E6.3.0.3"),sQuery(id+"F0.wireOp",EDGE,"E6.4.0.0"),sQuery(id+"F0.wireOp",EDGE,"E6.4.0.1"),sQuery(id+"F0.wireOp",EDGE,"E6.4.0.2"),sQuery(id+"F0.wireOp",EDGE,"E6.4.0.3"),sQuery(id+"F0.wireOp",EDGE,"E6.5.0.0"),sQuery(id+"F0.wireOp",EDGE,"E6.5.0.1"),sQuery(id+"F0.wireOp",EDGE,"E6.5.0.2"),sQuery(id+"F0.wireOp",EDGE,"E6.5.0.3"),sQuery(id+"F0.wireOp",EDGE,"E6.6.0.0"),sQuery(id+"F0.wireOp",EDGE,"E6.6.0.1"),sQuery(id+"F0.wireOp",EDGE,"E6.6.0.2"),sQuery(id+"F0.wireOp",EDGE,"E6.6.0.3"),sQuery(id+"F0.wireOp",EDGE,"E6.7.0.0"),sQuery(id+"F0.wireOp",EDGE,"E6.7.0.1"),sQuery(id+"F0.wireOp",EDGE,"E6.7.0.2"),sQuery(id+"F0.wireOp",EDGE,"E6.7.0.3"),sQuery(id+"F0.wireOp",EDGE,"E6.8.0.0"),sQuery(id+"F0.wireOp",EDGE,"E6.8.0.1"),sQuery(id+"F0.wireOp",EDGE,"E6.8.0.2"),sQuery(id+"F0.wireOp",EDGE,"E6.8.0.3"),sQuery(id+"F0.wireOp",EDGE,"E6.9.0.0"),sQuery(id+"F0.wireOp",EDGE,"E6.9.0.1"),sQuery(id+"F0.wireOp",EDGE,"E6.9.0.2"),sQuery(id+"F0.wireOp",EDGE,"E6.9.0.3"),sQuery(id+"F0.wireOp",EDGE,"E6.10.0.0"),sQuery(id+"F0.wireOp",EDGE,"E6.10.0.1"),sQuery(id+"F0.wireOp",EDGE,"E6.10.0.2"),sQuery(id+"F0.wireOp",EDGE,"E6.10.0.3"),sQuery(id+"F0.wireOp",EDGE,"E6.11.0.0"),sQuery(id+"F0.wireOp",EDGE,"E6.11.0.1"),sQuery(id+"F0.wireOp",EDGE,"E6.11.0.2"),sQuery(id+"F0.wireOp",EDGE,"E6.11.0.3"),sQuery(id+"F0.wireOp",EDGE,"E6.12.0.0"),sQuery(id+"F0.wireOp",EDGE,"E6.12.0.1"),sQuery(id+"F0.wireOp",EDGE,"E6.12.0.2"),sQuery(id+"F0.wireOp",EDGE,"E6.12.0.3"),sQuery(id+"F0.wireOp",EDGE,"E6.13.0.0"),sQuery(id+"F0.wireOp",EDGE,"E6.13.0.1"),sQuery(id+"F0.wireOp",EDGE,"E6.13.0.2"),sQuery(id+"F0.wireOp",EDGE,"E6.13.0.3"),sQuery(id+"F0.wireOp",EDGE,"E6.14.0.0"),sQuery(id+"F0.wireOp",EDGE,"E6.14.0.1"),sQuery(id+"F0.wireOp",EDGE,"E6.14.0.2"),sQuery(id+"F0.wireOp",EDGE,"E6.14.0.3"),sQuery(id+"F0.wireOp",EDGE,"E6.15.0.0"),sQuery(id+"F0.wireOp",EDGE,"E6.15.0.1"),sQuery(id+"F0.wireOp",EDGE,"E6.15.0.2"),sQuery(id+"F0.wireOp",EDGE,"E6.15.0.3"),sQuery(id+"F0.wireOp",EDGE,"E6.16.0.0"),sQuery(id+"F0.wireOp",EDGE,"E6.16.0.1"),sQuery(id+"F0.wireOp",EDGE,"E6.16.0.2"),sQuery(id+"F0.wireOp",EDGE,"E6.16.0.3"),sQuery(id+"F0.wireOp",EDGE,"E6.17.0.0"),sQuery(id+"F0.wireOp",EDGE,"E6.17.0.1"),sQuery(id+"F0.wireOp",EDGE,"E6.17.0.2"),sQuery(id+"F0.wireOp",EDGE,"E6.17.0.3"),sQuery(id+"F0.wireOp",EDGE,"E7.1.0.0"),sQuery(id+"F0.wireOp",EDGE,"E7.1.0.1"),sQuery(id+"F0.wireOp",EDGE,"E7.1.0.2"),sQuery(id+"F0.wireOp",EDGE,"E7.1.0.3"),sQuery(id+"F0.wireOp",EDGE,"E7.2.0.0"),sQuery(id+"F0.wireOp",EDGE,"E7.2.0.1"),sQuery(id+"F0.wireOp",EDGE,"E7.2.0.2"),sQuery(id+"F0.wireOp",EDGE,"E7.2.0.3"),sQuery(id+"F0.wireOp",EDGE,"E7.3.0.0"),sQuery(id+"F0.wireOp",EDGE,"E7.3.0.1"),sQuery(id+"F0.wireOp",EDGE,"E7.3.0.2"),sQuery(id+"F0.wireOp",EDGE,"E7.3.0.3"),sQuery(id+"F0.wireOp",EDGE,"E7.4.0.0"),sQuery(id+"F0.wireOp",EDGE,"E7.4.0.1"),sQuery(id+"F0.wireOp",EDGE,"E7.4.0.2"),sQuery(id+"F0.wireOp",EDGE,"E7.4.0.3"),sQuery(id+"F0.wireOp",EDGE,"E7.5.0.0"),sQuery(id+"F0.wireOp",EDGE,"E7.5.0.1"),sQuery(id+"F0.wireOp",EDGE,"E7.5.0.2"),sQuery(id+"F0.wireOp",EDGE,"E7.5.0.3"),sQuery(id+"F0.wireOp",EDGE,"E7.6.0.0"),sQuery(id+"F0.wireOp",EDGE,"E7.6.0.1"),sQuery(id+"F0.wireOp",EDGE,"E7.6.0.2"),sQuery(id+"F0.wireOp",EDGE,"E7.6.0.3"),sQuery(id+"F0.wireOp",EDGE,"E7.7.0.0"),sQuery(id+"F0.wireOp",EDGE,"E7.7.0.1"),sQuery(id+"F0.wireOp",EDGE,"E7.7.0.2"),sQuery(id+"F0.wireOp",EDGE,"E7.7.0.3"),sQuery(id+"F0.wireOp",EDGE,"E7.8.0.0"),sQuery(id+"F0.wireOp",EDGE,"E7.8.0.1"),sQuery(id+"F0.wireOp",EDGE,"E7.8.0.2"),sQuery(id+"F0.wireOp",EDGE,"E7.8.0.3"),sQuery(id+"F0.wireOp",EDGE,"E7.9.0.0"),sQuery(id+"F0.wireOp",EDGE,"E7.9.0.1"),sQuery(id+"F0.wireOp",EDGE,"E7.9.0.2"),sQuery(id+"F0.wireOp",EDGE,"E7.9.0.3"),sQuery(id+"F0.wireOp",EDGE,"E7.10.0.0"),sQuery(id+"F0.wireOp",EDGE,"E7.10.0.1"),sQuery(id+"F0.wireOp",EDGE,"E7.10.0.2"),sQuery(id+"F0.wireOp",EDGE,"E7.10.0.3"),sQuery(id+"F0.wireOp",EDGE,"E7.11.0.0"),sQuery(id+"F0.wireOp",EDGE,"E7.11.0.1"),sQuery(id+"F0.wireOp",EDGE,"E7.11.0.2"),sQuery(id+"F0.wireOp",EDGE,"E7.11.0.3"),sQuery(id+"F0.wireOp",EDGE,"E7.12.0.0"),sQuery(id+"F0.wireOp",EDGE,"E7.12.0.1"),sQuery(id+"F0.wireOp",EDGE,"E7.12.0.2"),sQuery(id+"F0.wireOp",EDGE,"E7.12.0.3"),sQuery(id+"F0.wireOp",EDGE,"E8.1.0.0"),sQuery(id+"F0.wireOp",EDGE,"E8.1.0.1"),sQuery(id+"F0.wireOp",EDGE,"E8.1.0.2"),sQuery(id+"F0.wireOp",EDGE,"E8.1.0.3"),sQuery(id+"F0.wireOp",EDGE,"E8.2.0.0"),sQuery(id+"F0.wireOp",EDGE,"E8.2.0.1"),sQuery(id+"F0.wireOp",EDGE,"E8.2.0.2"),sQuery(id+"F0.wireOp",EDGE,"E8.2.0.3"),sQuery(id+"F0.wireOp",EDGE,"E8.3.0.0"),sQuery(id+"F0.wireOp",EDGE,"E8.3.0.1"),sQuery(id+"F0.wireOp",EDGE,"E8.3.0.2"),sQuery(id+"F0.wireOp",EDGE,"E8.3.0.3"),sQuery(id+"F0.wireOp",EDGE,"E8.4.0.0"),sQuery(id+"F0.wireOp",EDGE,"E8.4.0.1"),sQuery(id+"F0.wireOp",EDGE,"E8.4.0.2"),sQuery(id+"F0.wireOp",EDGE,"E8.4.0.3"),sQuery(id+"F0.wireOp",EDGE,"E8.5.0.0"),sQuery(id+"F0.wireOp",EDGE,"E8.5.0.1"),sQuery(id+"F0.wireOp",EDGE,"E8.5.0.2"),sQuery(id+"F0.wireOp",EDGE,"E8.5.0.3"),sQuery(id+"F0.wireOp",EDGE,"E8.6.0.0"),sQuery(id+"F0.wireOp",EDGE,"E8.6.0.1"),sQuery(id+"F0.wireOp",EDGE,"E8.6.0.2"),sQuery(id+"F0.wireOp",EDGE,"E8.6.0.3"),sQuery(id+"F0.wireOp",EDGE,"E8.7.0.0"),sQuery(id+"F0.wireOp",EDGE,"E8.7.0.1"),sQuery(id+"F0.wireOp",EDGE,"E8.7.0.2"),sQuery(id+"F0.wireOp",EDGE,"E8.7.0.3"),sQuery(id+"F0.wireOp",EDGE,"E8.8.0.0"),sQuery(id+"F0.wireOp",EDGE,"E8.8.0.1"),sQuery(id+"F0.wireOp",EDGE,"E8.8.0.2"),sQuery(id+"F0.wireOp",EDGE,"E8.8.0.3"),sQuery(id+"F0.wireOp",EDGE,"E8.9.0.0"),sQuery(id+"F0.wireOp",EDGE,"E8.9.0.1"),sQuery(id+"F0.wireOp",EDGE,"E8.9.0.2"),sQuery(id+"F0.wireOp",EDGE,"E8.9.0.3"),sQuery(id+"F0.wireOp",EDGE,"E8.10.0.0"),sQuery(id+"F0.wireOp",EDGE,"E8.10.0.1"),sQuery(id+"F0.wireOp",EDGE,"E8.10.0.2"),sQuery(id+"F0.wireOp",EDGE,"E8.10.0.3"),sQuery(id+"F0.wireOp",EDGE,"E8.11.0.0"),sQuery(id+"F0.wireOp",EDGE,"E8.11.0.1"),sQuery(id+"F0.wireOp",EDGE,"E8.11.0.2"),sQuery(id+"F0.wireOp",EDGE,"E8.11.0.3"),sQuery(id+"F0.wireOp",EDGE,"E8.12.0.0"),sQuery(id+"F0.wireOp",EDGE,"E8.12.0.1"),sQuery(id+"F0.wireOp",EDGE,"E8.12.0.2"),sQuery(id+"F0.wireOp",EDGE,"E8.12.0.3"),sQuery(id+"F0.wireOp",EDGE,"E9.1.0.0"),sQuery(id+"F0.wireOp",EDGE,"E9.1.0.1"),sQuery(id+"F0.wireOp",EDGE,"E9.1.0.2"),sQuery(id+"F0.wireOp",EDGE,"E9.1.0.3"),sQuery(id+"F0.wireOp",EDGE,"E9.2.0.0"),sQuery(id+"F0.wireOp",EDGE,"E9.2.0.1"),sQuery(id+"F0.wireOp",EDGE,"E9.2.0.2"),sQuery(id+"F0.wireOp",EDGE,"E9.2.0.3"),sQuery(id+"F0.wireOp",EDGE,"E9.3.0.0"),sQuery(id+"F0.wireOp",EDGE,"E9.3.0.1"),sQuery(id+"F0.wireOp",EDGE,"E9.3.0.2"),sQuery(id+"F0.wireOp",EDGE,"E9.3.0.3"),sQuery(id+"F0.wireOp",EDGE,"E9.4.0.0"),sQuery(id+"F0.wireOp",EDGE,"E9.4.0.1"),sQuery(id+"F0.wireOp",EDGE,"E9.4.0.2"),sQuery(id+"F0.wireOp",EDGE,"E9.4.0.3"),sQuery(id+"F0.wireOp",EDGE,"E9.5.0.0"),sQuery(id+"F0.wireOp",EDGE,"E9.5.0.1"),sQuery(id+"F0.wireOp",EDGE,"E9.5.0.2"),sQuery(id+"F0.wireOp",EDGE,"E9.5.0.3"),sQuery(id+"F0.wireOp",EDGE,"E9.6.0.0"),sQuery(id+"F0.wireOp",EDGE,"E9.6.0.1"),sQuery(id+"F0.wireOp",EDGE,"E9.6.0.2"),sQuery(id+"F0.wireOp",EDGE,"E9.6.0.3"),sQuery(id+"F0.wireOp",EDGE,"E9.7.0.0"),sQuery(id+"F0.wireOp",EDGE,"E9.7.0.1"),sQuery(id+"F0.wireOp",EDGE,"E9.7.0.2"),sQuery(id+"F0.wireOp",EDGE,"E9.7.0.3"),sQuery(id+"F0.wireOp",EDGE,"E9.8.0.0"),sQuery(id+"F0.wireOp",EDGE,"E9.8.0.1"),sQuery(id+"F0.wireOp",EDGE,"E9.8.0.2"),sQuery(id+"F0.wireOp",EDGE,"E9.8.0.3"),sQuery(id+"F0.wireOp",EDGE,"E9.9.0.0"),sQuery(id+"F0.wireOp",EDGE,"E9.9.0.1"),sQuery(id+"F0.wireOp",EDGE,"E9.9.0.2"),sQuery(id+"F0.wireOp",EDGE,"E9.9.0.3"),sQuery(id+"F0.wireOp",EDGE,"E9.10.0.0"),sQuery(id+"F0.wireOp",EDGE,"E9.10.0.1"),sQuery(id+"F0.wireOp",EDGE,"E9.10.0.2"),sQuery(id+"F0.wireOp",EDGE,"E9.10.0.3"),sQuery(id+"F0.wireOp",EDGE,"E9.11.0.0"),sQuery(id+"F0.wireOp",EDGE,"E9.11.0.1"),sQuery(id+"F0.wireOp",EDGE,"E9.11.0.2"),sQuery(id+"F0.wireOp",EDGE,"E9.11.0.3"),sQuery(id+"F0.wireOp",EDGE,"E9.12.0.0"),sQuery(id+"F0.wireOp",EDGE,"E9.12.0.1"),sQuery(id+"F0.wireOp",EDGE,"E9.12.0.2"),sQuery(id+"F0.wireOp",EDGE,"E9.12.0.3"),sQuery(id+"F0.wireOp",EDGE,"E10.1.0.0"),sQuery(id+"F0.wireOp",EDGE,"E10.1.0.1"),sQuery(id+"F0.wireOp",EDGE,"E10.1.0.2"),sQuery(id+"F0.wireOp",EDGE,"E10.1.0.3"),sQuery(id+"F0.wireOp",EDGE,"E10.1.0.4"),sQuery(id+"F0.wireOp",EDGE,"E10.1.0.5"),sQuery(id+"F0.wireOp",EDGE,"E10.1.0.6"),sQuery(id+"F0.wireOp",EDGE,"E10.1.0.7"),sQuery(id+"F0.wireOp",EDGE,"E10.1.0.8"),sQuery(id+"F0.wireOp",EDGE,"E10.1.0.9"),sQuery(id+"F0.wireOp",EDGE,"E10.1.0.10"),sQuery(id+"F0.wireOp",EDGE,"E10.1.0.11"),sQuery(id+"F0.wireOp",EDGE,"E10.1.0.12"),sQuery(id+"F0.wireOp",EDGE,"E10.1.0.13"),sQuery(id+"F0.wireOp",EDGE,"E10.1.0.14"),sQuery(id+"F0.wireOp",EDGE,"E10.1.0.15"),sQuery(id+"F0.wireOp",EDGE,"E10.1.0.16"),sQuery(id+"F0.wireOp",EDGE,"E10.1.0.17"),sQuery(id+"F0.wireOp",EDGE,"E10.1.0.18"),sQuery(id+"F0.wireOp",EDGE,"E10.1.0.19"),sQuery(id+"F0.wireOp",EDGE,"E10.2.0.0"),sQuery(id+"F0.wireOp",EDGE,"E10.2.0.1"),sQuery(id+"F0.wireOp",EDGE,"E10.2.0.2"),sQuery(id+"F0.wireOp",EDGE,"E10.2.0.3"),sQuery(id+"F0.wireOp",EDGE,"E10.2.0.4"),sQuery(id+"F0.wireOp",EDGE,"E10.2.0.5"),sQuery(id+"F0.wireOp",EDGE,"E10.2.0.6"),sQuery(id+"F0.wireOp",EDGE,"E10.2.0.7"),sQuery(id+"F0.wireOp",EDGE,"E10.2.0.8"),sQuery(id+"F0.wireOp",EDGE,"E10.2.0.9"),sQuery(id+"F0.wireOp",EDGE,"E10.2.0.10"),sQuery(id+"F0.wireOp",EDGE,"E10.2.0.11"),sQuery(id+"F0.wireOp",EDGE,"E10.2.0.12"),sQuery(id+"F0.wireOp",EDGE,"E10.2.0.13"),sQuery(id+"F0.wireOp",EDGE,"E10.2.0.14"),sQuery(id+"F0.wireOp",EDGE,"E10.2.0.15"),sQuery(id+"F0.wireOp",EDGE,"E10.2.0.16"),sQuery(id+"F0.wireOp",EDGE,"E10.2.0.17"),sQuery(id+"F0.wireOp",EDGE,"E10.2.0.18"),sQuery(id+"F0.wireOp",EDGE,"E10.2.0.19"),sQuery(id+"F0.wireOp",EDGE,"E10.3.0.0"),sQuery(id+"F0.wireOp",EDGE,"E10.3.0.1"),sQuery(id+"F0.wireOp",EDGE,"E10.3.0.2"),sQuery(id+"F0.wireOp",EDGE,"E10.3.0.3"),sQuery(id+"F0.wireOp",EDGE,"E10.3.0.4"),sQuery(id+"F0.wireOp",EDGE,"E10.3.0.5"),sQuery(id+"F0.wireOp",EDGE,"E10.3.0.6"),sQuery(id+"F0.wireOp",EDGE,"E10.3.0.7"),sQuery(id+"F0.wireOp",EDGE,"E10.3.0.8"),sQuery(id+"F0.wireOp",EDGE,"E10.3.0.9"),sQuery(id+"F0.wireOp",EDGE,"E10.3.0.10"),sQuery(id+"F0.wireOp",EDGE,"E10.3.0.11"),sQuery(id+"F0.wireOp",EDGE,"E10.3.0.12"),sQuery(id+"F0.wireOp",EDGE,"E10.3.0.13"),sQuery(id+"F0.wireOp",EDGE,"E10.3.0.14"),sQuery(id+"F0.wireOp",EDGE,"E10.3.0.15"),sQuery(id+"F0.wireOp",EDGE,"E10.3.0.16"),sQuery(id+"F0.wireOp",EDGE,"E10.3.0.17"),sQuery(id+"F0.wireOp",EDGE,"E10.3.0.18"),sQuery(id+"F0.wireOp",EDGE,"E10.3.0.19"),sQuery(id+"F0.wireOp",EDGE,"E10.4.0.0"),sQuery(id+"F0.wireOp",EDGE,"E10.4.0.1"),sQuery(id+"F0.wireOp",EDGE,"E10.4.0.2"),sQuery(id+"F0.wireOp",EDGE,"E10.4.0.3"),sQuery(id+"F0.wireOp",EDGE,"E10.4.0.4"),sQuery(id+"F0.wireOp",EDGE,"E10.4.0.5"),sQuery(id+"F0.wireOp",EDGE,"E10.4.0.6"),sQuery(id+"F0.wireOp",EDGE,"E10.4.0.7"),sQuery(id+"F0.wireOp",EDGE,"E10.4.0.8"),sQuery(id+"F0.wireOp",EDGE,"E10.4.0.9"),sQuery(id+"F0.wireOp",EDGE,"E10.4.0.10"),sQuery(id+"F0.wireOp",EDGE,"E10.4.0.11"),sQuery(id+"F0.wireOp",EDGE,"E10.4.0.12"),sQuery(id+"F0.wireOp",EDGE,"E10.4.0.13"),sQuery(id+"F0.wireOp",EDGE,"E10.4.0.14"),sQuery(id+"F0.wireOp",EDGE,"E10.4.0.15"),sQuery(id+"F0.wireOp",EDGE,"E10.4.0.16"),sQuery(id+"F0.wireOp",EDGE,"E10.4.0.17"),sQuery(id+"F0.wireOp",EDGE,"E10.4.0.18"),sQuery(id+"F0.wireOp",EDGE,"E10.4.0.19"),sQuery(id+"F0.wireOp",EDGE,"E10.5.0.0"),sQuery(id+"F0.wireOp",EDGE,"E10.5.0.1"),sQuery(id+"F0.wireOp",EDGE,"E10.5.0.2"),sQuery(id+"F0.wireOp",EDGE,"E10.5.0.3"),sQuery(id+"F0.wireOp",EDGE,"E10.5.0.4"),sQuery(id+"F0.wireOp",EDGE,"E10.5.0.5"),sQuery(id+"F0.wireOp",EDGE,"E10.5.0.6"),sQuery(id+"F0.wireOp",EDGE,"E10.5.0.7"),sQuery(id+"F0.wireOp",EDGE,"E10.5.0.8"),sQuery(id+"F0.wireOp",EDGE,"E10.5.0.9"),sQuery(id+"F0.wireOp",EDGE,"E10.5.0.10"),sQuery(id+"F0.wireOp",EDGE,"E10.5.0.11"),sQuery(id+"F0.wireOp",EDGE,"E10.5.0.12"),sQuery(id+"F0.wireOp",EDGE,"E10.5.0.13"),sQuery(id+"F0.wireOp",EDGE,"E10.5.0.14"),sQuery(id+"F0.wireOp",EDGE,"E10.5.0.15"),sQuery(id+"F0.wireOp",EDGE,"E10.5.0.16"),sQuery(id+"F0.wireOp",EDGE,"E10.5.0.17"),sQuery(id+"F0.wireOp",EDGE,"E10.5.0.18"),sQuery(id+"F0.wireOp",EDGE,"E10.5.0.19"),sQuery(id+"F0.wireOp",EDGE,"E10.6.0.0"),sQuery(id+"F0.wireOp",EDGE,"E10.6.0.1"),sQuery(id+"F0.wireOp",EDGE,"E10.6.0.2"),sQuery(id+"F0.wireOp",EDGE,"E10.6.0.3"),sQuery(id+"F0.wireOp",EDGE,"E10.6.0.4"),sQuery(id+"F0.wireOp",EDGE,"E10.6.0.5"),sQuery(id+"F0.wireOp",EDGE,"E10.6.0.6"),sQuery(id+"F0.wireOp",EDGE,"E10.6.0.7"),sQuery(id+"F0.wireOp",EDGE,"E10.6.0.8"),sQuery(id+"F0.wireOp",EDGE,"E10.6.0.9"),sQuery(id+"F0.wireOp",EDGE,"E10.6.0.10"),sQuery(id+"F0.wireOp",EDGE,"E10.6.0.11"),sQuery(id+"F0.wireOp",EDGE,"E10.6.0.12"),sQuery(id+"F0.wireOp",EDGE,"E10.6.0.13"),sQuery(id+"F0.wireOp",EDGE,"E10.6.0.14"),sQuery(id+"F0.wireOp",EDGE,"E10.6.0.15"),sQuery(id+"F0.wireOp",EDGE,"E10.6.0.16"),sQuery(id+"F0.wireOp",EDGE,"E10.6.0.17"),sQuery(id+"F0.wireOp",EDGE,"E10.6.0.18"),sQuery(id+"F0.wireOp",EDGE,"E10.6.0.19"),sQuery(id+"F0.wireOp",EDGE,"E10.7.0.0"),sQuery(id+"F0.wireOp",EDGE,"E10.7.0.1"),sQuery(id+"F0.wireOp",EDGE,"E10.7.0.2"),sQuery(id+"F0.wireOp",EDGE,"E10.7.0.3"),sQuery(id+"F0.wireOp",EDGE,"E10.7.0.4"),sQuery(id+"F0.wireOp",EDGE,"E10.7.0.5"),sQuery(id+"F0.wireOp",EDGE,"E10.7.0.6"),sQuery(id+"F0.wireOp",EDGE,"E10.7.0.7"),sQuery(id+"F0.wireOp",EDGE,"E10.7.0.8"),sQuery(id+"F0.wireOp",EDGE,"E10.7.0.9"),sQuery(id+"F0.wireOp",EDGE,"E10.7.0.10"),sQuery(id+"F0.wireOp",EDGE,"E10.7.0.11"),sQuery(id+"F0.wireOp",EDGE,"E10.7.0.12"),sQuery(id+"F0.wireOp",EDGE,"E10.7.0.13"),sQuery(id+"F0.wireOp",EDGE,"E10.7.0.14"),sQuery(id+"F0.wireOp",EDGE,"E10.7.0.15"),sQuery(id+"F0.wireOp",EDGE,"E10.7.0.16"),sQuery(id+"F0.wireOp",EDGE,"E10.7.0.17"),sQuery(id+"F0.wireOp",EDGE,"E10.7.0.18"),sQuery(id+"F0.wireOp",EDGE,"E10.7.0.19"),sQuery(id+"F0.wireOp",EDGE,"E10.8.0.0"),sQuery(id+"F0.wireOp",EDGE,"E10.8.0.1"),sQuery(id+"F0.wireOp",EDGE,"E10.8.0.2"),sQuery(id+"F0.wireOp",EDGE,"E10.8.0.3"),sQuery(id+"F0.wireOp",EDGE,"E10.8.0.4"),sQuery(id+"F0.wireOp",EDGE,"E10.8.0.5"),sQuery(id+"F0.wireOp",EDGE,"E10.8.0.6"),sQuery(id+"F0.wireOp",EDGE,"E10.8.0.7"),sQuery(id+"F0.wireOp",EDGE,"E10.8.0.8"),sQuery(id+"F0.wireOp",EDGE,"E10.8.0.9"),sQuery(id+"F0.wireOp",EDGE,"E10.8.0.10"),sQuery(id+"F0.wireOp",EDGE,"E10.8.0.11"),sQuery(id+"F0.wireOp",EDGE,"E10.8.0.12"),sQuery(id+"F0.wireOp",EDGE,"E10.8.0.13"),sQuery(id+"F0.wireOp",EDGE,"E10.8.0.14"),sQuery(id+"F0.wireOp",EDGE,"E10.8.0.15"),sQuery(id+"F0.wireOp",EDGE,"E10.8.0.16"),sQuery(id+"F0.wireOp",EDGE,"E10.8.0.17"),sQuery(id+"F0.wireOp",EDGE,"E10.8.0.18"),sQuery(id+"F0.wireOp",EDGE,"E10.8.0.19"),sQuery(id+"F0.wireOp",EDGE,"E10.9.0.0"),sQuery(id+"F0.wireOp",EDGE,"E10.9.0.1"),sQuery(id+"F0.wireOp",EDGE,"E10.9.0.2"),sQuery(id+"F0.wireOp",EDGE,"E10.9.0.3"),sQuery(id+"F0.wireOp",EDGE,"E10.9.0.4"),sQuery(id+"F0.wireOp",EDGE,"E10.9.0.5"),sQuery(id+"F0.wireOp",EDGE,"E10.9.0.6"),sQuery(id+"F0.wireOp",EDGE,"E10.9.0.7"),sQuery(id+"F0.wireOp",EDGE,"E10.9.0.8"),sQuery(id+"F0.wireOp",EDGE,"E10.9.0.9"),sQuery(id+"F0.wireOp",EDGE,"E10.9.0.10"),sQuery(id+"F0.wireOp",EDGE,"E10.9.0.11"),sQuery(id+"F0.wireOp",EDGE,"E10.9.0.12"),sQuery(id+"F0.wireOp",EDGE,"E10.9.0.13"),sQuery(id+"F0.wireOp",EDGE,"E10.9.0.14"),sQuery(id+"F0.wireOp",EDGE,"E10.9.0.15"),sQuery(id+"F0.wireOp",EDGE,"E10.9.0.16"),sQuery(id+"F0.wireOp",EDGE,"E10.9.0.17"),sQuery(id+"F0.wireOp",EDGE,"E10.9.0.18"),sQuery(id+"F0.wireOp",EDGE,"E10.9.0.19"),sQuery(id+"F0.wireOp",EDGE,"E10.10.0.0"),sQuery(id+"F0.wireOp",EDGE,"E10.10.0.1"),sQuery(id+"F0.wireOp",EDGE,"E10.10.0.2"),sQuery(id+"F0.wireOp",EDGE,"E10.10.0.3"),sQuery(id+"F0.wireOp",EDGE,"E10.10.0.4"),sQuery(id+"F0.wireOp",EDGE,"E10.10.0.5"),sQuery(id+"F0.wireOp",EDGE,"E10.10.0.6"),sQuery(id+"F0.wireOp",EDGE,"E10.10.0.7"),sQuery(id+"F0.wireOp",EDGE,"E10.10.0.8"),sQuery(id+"F0.wireOp",EDGE,"E10.10.0.9"),sQuery(id+"F0.wireOp",EDGE,"E10.10.0.10"),sQuery(id+"F0.wireOp",EDGE,"E10.10.0.11"),sQuery(id+"F0.wireOp",EDGE,"E10.10.0.12"),sQuery(id+"F0.wireOp",EDGE,"E10.10.0.13"),sQuery(id+"F0.wireOp",EDGE,"E10.10.0.14"),sQuery(id+"F0.wireOp",EDGE,"E10.10.0.15"),sQuery(id+"F0.wireOp",EDGE,"E10.10.0.16"),sQuery(id+"F0.wireOp",EDGE,"E10.10.0.17"),sQuery(id+"F0.wireOp",EDGE,"E10.10.0.18"),sQuery(id+"F0.wireOp",EDGE,"E10.10.0.19"),sQuery(id+"F0.wireOp",EDGE,"E10.11.0.0"),sQuery(id+"F0.wireOp",EDGE,"E10.11.0.1"),sQuery(id+"F0.wireOp",EDGE,"E10.11.0.2"),sQuery(id+"F0.wireOp",EDGE,"E10.11.0.3"),sQuery(id+"F0.wireOp",EDGE,"E10.11.0.4"),sQuery(id+"F0.wireOp",EDGE,"E10.11.0.5"),sQuery(id+"F0.wireOp",EDGE,"E10.11.0.6"),sQuery(id+"F0.wireOp",EDGE,"E10.11.0.7"),sQuery(id+"F0.wireOp",EDGE,"E10.11.0.8"),sQuery(id+"F0.wireOp",EDGE,"E10.11.0.9"),sQuery(id+"F0.wireOp",EDGE,"E10.11.0.10"),sQuery(id+"F0.wireOp",EDGE,"E10.11.0.11"),sQuery(id+"F0.wireOp",EDGE,"E10.11.0.12"),sQuery(id+"F0.wireOp",EDGE,"E10.11.0.13"),sQuery(id+"F0.wireOp",EDGE,"E10.11.0.14"),sQuery(id+"F0.wireOp",EDGE,"E10.11.0.15"),sQuery(id+"F0.wireOp",EDGE,"E10.11.0.16"),sQuery(id+"F0.wireOp",EDGE,"E10.11.0.17"),sQuery(id+"F0.wireOp",EDGE,"E10.11.0.18"),sQuery(id+"F0.wireOp",EDGE,"E10.11.0.19"),sQuery(id+"F0.wireOp",EDGE,"E10.12.0.0"),sQuery(id+"F0.wireOp",EDGE,"E10.12.0.1"),sQuery(id+"F0.wireOp",EDGE,"E10.12.0.2"),sQuery(id+"F0.wireOp",EDGE,"E10.12.0.3"),sQuery(id+"F0.wireOp",EDGE,"E10.12.0.4"),sQuery(id+"F0.wireOp",EDGE,"E10.12.0.5"),sQuery(id+"F0.wireOp",EDGE,"E10.12.0.6"),sQuery(id+"F0.wireOp",EDGE,"E10.12.0.7"),sQuery(id+"F0.wireOp",EDGE,"E10.12.0.8"),sQuery(id+"F0.wireOp",EDGE,"E10.12.0.9"),sQuery(id+"F0.wireOp",EDGE,"E10.12.0.10"),sQuery(id+"F0.wireOp",EDGE,"E10.12.0.11"),sQuery(id+"F0.wireOp",EDGE,"E10.12.0.12"),sQuery(id+"F0.wireOp",EDGE,"E10.12.0.13"),sQuery(id+"F0.wireOp",EDGE,"E10.12.0.14"),sQuery(id+"F0.wireOp",EDGE,"E10.12.0.15"),sQuery(id+"F0.wireOp",EDGE,"E10.12.0.16"),sQuery(id+"F0.wireOp",EDGE,"E10.12.0.17"),sQuery(id+"F0.wireOp",EDGE,"E10.12.0.18"),sQuery(id+"F0.wireOp",EDGE,"E10.12.0.19"),sQuery(id+"F0.wireOp",EDGE,"E10.13.0.0"),sQuery(id+"F0.wireOp",EDGE,"E10.13.0.1"),sQuery(id+"F0.wireOp",EDGE,"E10.13.0.2"),sQuery(id+"F0.wireOp",EDGE,"E10.13.0.3"),sQuery(id+"F0.wireOp",EDGE,"E10.13.0.4"),sQuery(id+"F0.wireOp",EDGE,"E10.13.0.5"),sQuery(id+"F0.wireOp",EDGE,"E10.13.0.6"),sQuery(id+"F0.wireOp",EDGE,"E10.13.0.7"),sQuery(id+"F0.wireOp",EDGE,"E10.13.0.8"),sQuery(id+"F0.wireOp",EDGE,"E10.13.0.9"),sQuery(id+"F0.wireOp",EDGE,"E10.13.0.10"),sQuery(id+"F0.wireOp",EDGE,"E10.13.0.11"),sQuery(id+"F0.wireOp",EDGE,"E10.13.0.12"),sQuery(id+"F0.wireOp",EDGE,"E10.13.0.13"),sQuery(id+"F0.wireOp",EDGE,"E10.13.0.14"),sQuery(id+"F0.wireOp",EDGE,"E10.13.0.15"),sQuery(id+"F0.wireOp",EDGE,"E10.13.0.16"),sQuery(id+"F0.wireOp",EDGE,"E10.13.0.17"),sQuery(id+"F0.wireOp",EDGE,"E10.13.0.18"),sQuery(id+"F0.wireOp",EDGE,"E10.13.0.19"),sQuery(id+"F0.wireOp",EDGE,"E10.14.0.0"),sQuery(id+"F0.wireOp",EDGE,"E10.14.0.1"),sQuery(id+"F0.wireOp",EDGE,"E10.14.0.2"),sQuery(id+"F0.wireOp",EDGE,"E10.14.0.3"),sQuery(id+"F0.wireOp",EDGE,"E10.14.0.4"),sQuery(id+"F0.wireOp",EDGE,"E10.14.0.5"),sQuery(id+"F0.wireOp",EDGE,"E10.14.0.6"),sQuery(id+"F0.wireOp",EDGE,"E10.14.0.7"),sQuery(id+"F0.wireOp",EDGE,"E10.14.0.8"),sQuery(id+"F0.wireOp",EDGE,"E10.14.0.9"),sQuery(id+"F0.wireOp",EDGE,"E10.14.0.10"),sQuery(id+"F0.wireOp",EDGE,"E10.14.0.11"),sQuery(id+"F0.wireOp",EDGE,"E10.14.0.12"),sQuery(id+"F0.wireOp",EDGE,"E10.14.0.13"),sQuery(id+"F0.wireOp",EDGE,"E10.14.0.14"),sQuery(id+"F0.wireOp",EDGE,"E10.14.0.15"),sQuery(id+"F0.wireOp",EDGE,"E10.14.0.16"),sQuery(id+"F0.wireOp",EDGE,"E10.14.0.17"),sQuery(id+"F0.wireOp",EDGE,"E10.14.0.18"),sQuery(id+"F0.wireOp",EDGE,"E10.14.0.19"),sQuery(id+"F0.wireOp",EDGE,"E11.1.0.0"),sQuery(id+"F0.wireOp",EDGE,"E11.1.0.1"),sQuery(id+"F0.wireOp",EDGE,"E11.1.0.2"),sQuery(id+"F0.wireOp",EDGE,"E11.1.0.3"),sQuery(id+"F0.wireOp",EDGE,"E11.1.0.4"),sQuery(id+"F0.wireOp",EDGE,"E11.1.0.5"),sQuery(id+"F0.wireOp",EDGE,"E11.1.0.6"),sQuery(id+"F0.wireOp",EDGE,"E11.1.0.7"),sQuery(id+"F0.wireOp",EDGE,"E11.1.0.8"),sQuery(id+"F0.wireOp",EDGE,"E11.1.0.9"),sQuery(id+"F0.wireOp",EDGE,"E11.1.0.10"),sQuery(id+"F0.wireOp",EDGE,"E11.1.0.11"),sQuery(id+"F0.wireOp",EDGE,"E11.1.0.12"),sQuery(id+"F0.wireOp",EDGE,"E11.1.0.13"),sQuery(id+"F0.wireOp",EDGE,"E11.1.0.14"),sQuery(id+"F0.wireOp",EDGE,"E11.1.0.15"),sQuery(id+"F0.wireOp",EDGE,"E11.1.0.16"),sQuery(id+"F0.wireOp",EDGE,"E11.1.0.17"),sQuery(id+"F0.wireOp",EDGE,"E11.1.0.18"),sQuery(id+"F0.wireOp",EDGE,"E11.1.0.19"),sQuery(id+"F0.wireOp",EDGE,"E11.1.0.20"),sQuery(id+"F0.wireOp",EDGE,"E11.1.0.21"),sQuery(id+"F0.wireOp",EDGE,"E11.1.0.22"),sQuery(id+"F0.wireOp",EDGE,"E11.1.0.23"),sQuery(id+"F0.wireOp",EDGE,"E11.1.0.24"),sQuery(id+"F0.wireOp",EDGE,"E11.1.0.25"),sQuery(id+"F0.wireOp",EDGE,"E11.1.0.26"),sQuery(id+"F0.wireOp",EDGE,"E11.1.0.27"),sQuery(id+"F0.wireOp",EDGE,"E11.2.0.0"),sQuery(id+"F0.wireOp",EDGE,"E11.2.0.1"),sQuery(id+"F0.wireOp",EDGE,"E11.2.0.2"),sQuery(id+"F0.wireOp",EDGE,"E11.2.0.3"),sQuery(id+"F0.wireOp",EDGE,"E11.2.0.4"),sQuery(id+"F0.wireOp",EDGE,"E11.2.0.5"),sQuery(id+"F0.wireOp",EDGE,"E11.2.0.6"),sQuery(id+"F0.wireOp",EDGE,"E11.2.0.7"),sQuery(id+"F0.wireOp",EDGE,"E11.2.0.8"),sQuery(id+"F0.wireOp",EDGE,"E11.2.0.9"),sQuery(id+"F0.wireOp",EDGE,"E11.2.0.10"),sQuery(id+"F0.wireOp",EDGE,"E11.2.0.11"),sQuery(id+"F0.wireOp",EDGE,"E11.2.0.12"),sQuery(id+"F0.wireOp",EDGE,"E11.2.0.13"),sQuery(id+"F0.wireOp",EDGE,"E11.2.0.14"),sQuery(id+"F0.wireOp",EDGE,"E11.2.0.15"),sQuery(id+"F0.wireOp",EDGE,"E11.2.0.16"),sQuery(id+"F0.wireOp",EDGE,"E11.2.0.17"),sQuery(id+"F0.wireOp",EDGE,"E11.2.0.18"),sQuery(id+"F0.wireOp",EDGE,"E11.2.0.19"),sQuery(id+"F0.wireOp",EDGE,"E11.2.0.20"),sQuery(id+"F0.wireOp",EDGE,"E11.2.0.21"),sQuery(id+"F0.wireOp",EDGE,"E11.2.0.22"),sQuery(id+"F0.wireOp",EDGE,"E11.2.0.23"),sQuery(id+"F0.wireOp",EDGE,"E11.2.0.24"),sQuery(id+"F0.wireOp",EDGE,"E11.2.0.25"),sQuery(id+"F0.wireOp",EDGE,"E11.2.0.26"),sQuery(id+"F0.wireOp",EDGE,"E11.2.0.27"),sQuery(id+"F0.wireOp",EDGE,"E11.3.0.0"),sQuery(id+"F0.wireOp",EDGE,"E11.3.0.1"),sQuery(id+"F0.wireOp",EDGE,"E11.3.0.2"),sQuery(id+"F0.wireOp",EDGE,"E11.3.0.3"),sQuery(id+"F0.wireOp",EDGE,"E11.3.0.4"),sQuery(id+"F0.wireOp",EDGE,"E11.3.0.5"),sQuery(id+"F0.wireOp",EDGE,"E11.3.0.6"),sQuery(id+"F0.wireOp",EDGE,"E11.3.0.7"),sQuery(id+"F0.wireOp",EDGE,"E11.3.0.8"),sQuery(id+"F0.wireOp",EDGE,"E11.3.0.9"),sQuery(id+"F0.wireOp",EDGE,"E11.3.0.10"),sQuery(id+"F0.wireOp",EDGE,"E11.3.0.11"),sQuery(id+"F0.wireOp",EDGE,"E11.3.0.12"),sQuery(id+"F0.wireOp",EDGE,"E11.3.0.13"),sQuery(id+"F0.wireOp",EDGE,"E11.3.0.14"),sQuery(id+"F0.wireOp",EDGE,"E11.3.0.15"),sQuery(id+"F0.wireOp",EDGE,"E11.3.0.16"),sQuery(id+"F0.wireOp",EDGE,"E11.3.0.17"),sQuery(id+"F0.wireOp",EDGE,"E11.3.0.18"),sQuery(id+"F0.wireOp",EDGE,"E11.3.0.19"),sQuery(id+"F0.wireOp",EDGE,"E11.3.0.20"),sQuery(id+"F0.wireOp",EDGE,"E11.3.0.21"),sQuery(id+"F0.wireOp",EDGE,"E11.3.0.22"),sQuery(id+"F0.wireOp",EDGE,"E11.3.0.23"),sQuery(id+"F0.wireOp",EDGE,"E11.3.0.24"),sQuery(id+"F0.wireOp",EDGE,"E11.3.0.25"),sQuery(id+"F0.wireOp",EDGE,"E11.3.0.26"),sQuery(id+"F0.wireOp",EDGE,"E11.3.0.27"),sQuery(id+"F0.wireOp",EDGE,"E11.4.0.0"),sQuery(id+"F0.wireOp",EDGE,"E11.4.0.1"),sQuery(id+"F0.wireOp",EDGE,"E11.4.0.2"),sQuery(id+"F0.wireOp",EDGE,"E11.4.0.3"),sQuery(id+"F0.wireOp",EDGE,"E11.4.0.4"),sQuery(id+"F0.wireOp",EDGE,"E11.4.0.5"),sQuery(id+"F0.wireOp",EDGE,"E11.4.0.6"),sQuery(id+"F0.wireOp",EDGE,"E11.4.0.7"),sQuery(id+"F0.wireOp",EDGE,"E11.4.0.8"),sQuery(id+"F0.wireOp",EDGE,"E11.4.0.9"),sQuery(id+"F0.wireOp",EDGE,"E11.4.0.10"),sQuery(id+"F0.wireOp",EDGE,"E11.4.0.11"),sQuery(id+"F0.wireOp",EDGE,"E11.4.0.12"),sQuery(id+"F0.wireOp",EDGE,"E11.4.0.13"),sQuery(id+"F0.wireOp",EDGE,"E11.4.0.14"),sQuery(id+"F0.wireOp",EDGE,"E11.4.0.15"),sQuery(id+"F0.wireOp",EDGE,"E11.4.0.16"),sQuery(id+"F0.wireOp",EDGE,"E11.4.0.17"),sQuery(id+"F0.wireOp",EDGE,"E11.4.0.18"),sQuery(id+"F0.wireOp",EDGE,"E11.4.0.19"),sQuery(id+"F0.wireOp",EDGE,"E11.4.0.20"),sQuery(id+"F0.wireOp",EDGE,"E11.4.0.21"),sQuery(id+"F0.wireOp",EDGE,"E11.4.0.22"),sQuery(id+"F0.wireOp",EDGE,"E11.4.0.23"),sQuery(id+"F0.wireOp",EDGE,"E11.4.0.24"),sQuery(id+"F0.wireOp",EDGE,"E11.4.0.25"),sQuery(id+"F0.wireOp",EDGE,"E11.4.0.26"),sQuery(id+"F0.wireOp",EDGE,"E11.4.0.27"),sQuery(id+"F0.wireOp",EDGE,"E11.5.0.0"),sQuery(id+"F0.wireOp",EDGE,"E11.5.0.1"),sQuery(id+"F0.wireOp",EDGE,"E11.5.0.2"),sQuery(id+"F0.wireOp",EDGE,"E11.5.0.3"),sQuery(id+"F0.wireOp",EDGE,"E11.5.0.4"),sQuery(id+"F0.wireOp",EDGE,"E11.5.0.5"),sQuery(id+"F0.wireOp",EDGE,"E11.5.0.6"),sQuery(id+"F0.wireOp",EDGE,"E11.5.0.7"),sQuery(id+"F0.wireOp",EDGE,"E11.5.0.8"),sQuery(id+"F0.wireOp",EDGE,"E11.5.0.9"),sQuery(id+"F0.wireOp",EDGE,"E11.5.0.10"),sQuery(id+"F0.wireOp",EDGE,"E11.5.0.11"),sQuery(id+"F0.wireOp",EDGE,"E11.5.0.12"),sQuery(id+"F0.wireOp",EDGE,"E11.5.0.13"),sQuery(id+"F0.wireOp",EDGE,"E11.5.0.14"),sQuery(id+"F0.wireOp",EDGE,"E11.5.0.15"),sQuery(id+"F0.wireOp",EDGE,"E11.5.0.16"),sQuery(id+"F0.wireOp",EDGE,"E11.5.0.17"),sQuery(id+"F0.wireOp",EDGE,"E11.5.0.18"),sQuery(id+"F0.wireOp",EDGE,"E11.5.0.19"),sQuery(id+"F0.wireOp",EDGE,"E11.5.0.20"),sQuery(id+"F0.wireOp",EDGE,"E11.5.0.21"),sQuery(id+"F0.wireOp",EDGE,"E11.5.0.22"),sQuery(id+"F0.wireOp",EDGE,"E11.5.0.23"),sQuery(id+"F0.wireOp",EDGE,"E11.5.0.24"),sQuery(id+"F0.wireOp",EDGE,"E11.5.0.25"),sQuery(id+"F0.wireOp",EDGE,"E11.5.0.26"),sQuery(id+"F0.wireOp",EDGE,"E11.5.0.27"),sQuery(id+"F0.wireOp",EDGE,"E11.6.0.0"),sQuery(id+"F0.wireOp",EDGE,"E11.6.0.1"),sQuery(id+"F0.wireOp",EDGE,"E11.6.0.2"),sQuery(id+"F0.wireOp",EDGE,"E11.6.0.3"),sQuery(id+"F0.wireOp",EDGE,"E11.6.0.4"),sQuery(id+"F0.wireOp",EDGE,"E11.6.0.5"),sQuery(id+"F0.wireOp",EDGE,"E11.6.0.6"),sQuery(id+"F0.wireOp",EDGE,"E11.6.0.7"),sQuery(id+"F0.wireOp",EDGE,"E11.6.0.8"),sQuery(id+"F0.wireOp",EDGE,"E11.6.0.9"),sQuery(id+"F0.wireOp",EDGE,"E11.6.0.10"),sQuery(id+"F0.wireOp",EDGE,"E11.6.0.11"),sQuery(id+"F0.wireOp",EDGE,"E11.6.0.12"),sQuery(id+"F0.wireOp",EDGE,"E11.6.0.13"),sQuery(id+"F0.wireOp",EDGE,"E11.6.0.14"),sQuery(id+"F0.wireOp",EDGE,"E11.6.0.15"),sQuery(id+"F0.wireOp",EDGE,"E11.6.0.16"),sQuery(id+"F0.wireOp",EDGE,"E11.6.0.17"),sQuery(id+"F0.wireOp",EDGE,"E11.6.0.18"),sQuery(id+"F0.wireOp",EDGE,"E11.6.0.19"),sQuery(id+"F0.wireOp",EDGE,"E11.6.0.20"),sQuery(id+"F0.wireOp",EDGE,"E11.6.0.21"),sQuery(id+"F0.wireOp",EDGE,"E11.6.0.22"),sQuery(id+"F0.wireOp",EDGE,"E11.6.0.23"),sQuery(id+"F0.wireOp",EDGE,"E11.6.0.24"),sQuery(id+"F0.wireOp",EDGE,"E11.6.0.25"),sQuery(id+"F0.wireOp",EDGE,"E11.6.0.26"),sQuery(id+"F0.wireOp",EDGE,"E11.6.0.27"),sQuery(id+"F0.wireOp",EDGE,"E11.7.0.0"),sQuery(id+"F0.wireOp",EDGE,"E11.7.0.1"),sQuery(id+"F0.wireOp",EDGE,"E11.7.0.2"),sQuery(id+"F0.wireOp",EDGE,"E11.7.0.3"),sQuery(id+"F0.wireOp",EDGE,"E11.7.0.4"),sQuery(id+"F0.wireOp",EDGE,"E11.7.0.5"),sQuery(id+"F0.wireOp",EDGE,"E11.7.0.6"),sQuery(id+"F0.wireOp",EDGE,"E11.7.0.7"),sQuery(id+"F0.wireOp",EDGE,"E11.7.0.8"),sQuery(id+"F0.wireOp",EDGE,"E11.7.0.9"),sQuery(id+"F0.wireOp",EDGE,"E11.7.0.10"),sQuery(id+"F0.wireOp",EDGE,"E11.7.0.11"),sQuery(id+"F0.wireOp",EDGE,"E11.7.0.12"),sQuery(id+"F0.wireOp",EDGE,"E11.7.0.13"),sQuery(id+"F0.wireOp",EDGE,"E11.7.0.14"),sQuery(id+"F0.wireOp",EDGE,"E11.7.0.15"),sQuery(id+"F0.wireOp",EDGE,"E11.7.0.16"),sQuery(id+"F0.wireOp",EDGE,"E11.7.0.17"),sQuery(id+"F0.wireOp",EDGE,"E11.7.0.18"),sQuery(id+"F0.wireOp",EDGE,"E11.7.0.19"),sQuery(id+"F0.wireOp",EDGE,"E11.7.0.20"),sQuery(id+"F0.wireOp",EDGE,"E11.7.0.21"),sQuery(id+"F0.wireOp",EDGE,"E11.7.0.22"),sQuery(id+"F0.wireOp",EDGE,"E11.7.0.23"),sQuery(id+"F0.wireOp",EDGE,"E11.7.0.24"),sQuery(id+"F0.wireOp",EDGE,"E11.7.0.25"),sQuery(id+"F0.wireOp",EDGE,"E11.7.0.26"),sQuery(id+"F0.wireOp",EDGE,"E11.7.0.27"),sQuery(id+"F0.wireOp",EDGE,"E11.8.0.0"),sQuery(id+"F0.wireOp",EDGE,"E11.8.0.1"),sQuery(id+"F0.wireOp",EDGE,"E11.8.0.2"),sQuery(id+"F0.wireOp",EDGE,"E11.8.0.3"),sQuery(id+"F0.wireOp",EDGE,"E11.8.0.4"),sQuery(id+"F0.wireOp",EDGE,"E11.8.0.5"),sQuery(id+"F0.wireOp",EDGE,"E11.8.0.6"),sQuery(id+"F0.wireOp",EDGE,"E11.8.0.7"),sQuery(id+"F0.wireOp",EDGE,"E11.8.0.8"),sQuery(id+"F0.wireOp",EDGE,"E11.8.0.9"),sQuery(id+"F0.wireOp",EDGE,"E11.8.0.10"),sQuery(id+"F0.wireOp",EDGE,"E11.8.0.11"),sQuery(id+"F0.wireOp",EDGE,"E11.8.0.12"),sQuery(id+"F0.wireOp",EDGE,"E11.8.0.13"),sQuery(id+"F0.wireOp",EDGE,"E11.8.0.14"),sQuery(id+"F0.wireOp",EDGE,"E11.8.0.15"),sQuery(id+"F0.wireOp",EDGE,"E11.8.0.16"),sQuery(id+"F0.wireOp",EDGE,"E11.8.0.17"),sQuery(id+"F0.wireOp",EDGE,"E11.8.0.18"),sQuery(id+"F0.wireOp",EDGE,"E11.8.0.19"),sQuery(id+"F0.wireOp",EDGE,"E11.8.0.20"),sQuery(id+"F0.wireOp",EDGE,"E11.8.0.21"),sQuery(id+"F0.wireOp",EDGE,"E11.8.0.22"),sQuery(id+"F0.wireOp",EDGE,"E11.8.0.23"),sQuery(id+"F0.wireOp",EDGE,"E11.8.0.24"),sQuery(id+"F0.wireOp",EDGE,"E11.8.0.25"),sQuery(id+"F0.wireOp",EDGE,"E11.8.0.26"),sQuery(id+"F0.wireOp",EDGE,"E11.8.0.27"),sQuery(id+"F0.wireOp",EDGE,"E11.9.0.0"),sQuery(id+"F0.wireOp",EDGE,"E11.9.0.1"),sQuery(id+"F0.wireOp",EDGE,"E11.9.0.2"),sQuery(id+"F0.wireOp",EDGE,"E11.9.0.3"),sQuery(id+"F0.wireOp",EDGE,"E11.9.0.4"),sQuery(id+"F0.wireOp",EDGE,"E11.9.0.5"),sQuery(id+"F0.wireOp",EDGE,"E11.9.0.6"),sQuery(id+"F0.wireOp",EDGE,"E11.9.0.7"),sQuery(id+"F0.wireOp",EDGE,"E11.9.0.8"),sQuery(id+"F0.wireOp",EDGE,"E11.9.0.9"),sQuery(id+"F0.wireOp",EDGE,"E11.9.0.10"),sQuery(id+"F0.wireOp",EDGE,"E11.9.0.11"),sQuery(id+"F0.wireOp",EDGE,"E11.9.0.12"),sQuery(id+"F0.wireOp",EDGE,"E11.9.0.13"),sQuery(id+"F0.wireOp",EDGE,"E11.9.0.14"),sQuery(id+"F0.wireOp",EDGE,"E11.9.0.15"),sQuery(id+"F0.wireOp",EDGE,"E11.9.0.16"),sQuery(id+"F0.wireOp",EDGE,"E11.9.0.17"),sQuery(id+"F0.wireOp",EDGE,"E11.9.0.18"),sQuery(id+"F0.wireOp",EDGE,"E11.9.0.19"),sQuery(id+"F0.wireOp",EDGE,"E11.9.0.20"),sQuery(id+"F0.wireOp",EDGE,"E11.9.0.21"),sQuery(id+"F0.wireOp",EDGE,"E11.9.0.22"),sQuery(id+"F0.wireOp",EDGE,"E11.9.0.23"),sQuery(id+"F0.wireOp",EDGE,"E11.9.0.24"),sQuery(id+"F0.wireOp",EDGE,"E11.9.0.25"),sQuery(id+"F0.wireOp",EDGE,"E11.9.0.26"),sQuery(id+"F0.wireOp",EDGE,"E11.9.0.27"),sQuery(id+"F0.wireOp",EDGE,"E11.10.0.0"),sQuery(id+"F0.wireOp",EDGE,"E11.10.0.1"),sQuery(id+"F0.wireOp",EDGE,"E11.10.0.2"),sQuery(id+"F0.wireOp",EDGE,"E11.10.0.3"),sQuery(id+"F0.wireOp",EDGE,"E11.10.0.4"),sQuery(id+"F0.wireOp",EDGE,"E11.10.0.5"),sQuery(id+"F0.wireOp",EDGE,"E11.10.0.6"),sQuery(id+"F0.wireOp",EDGE,"E11.10.0.7"),sQuery(id+"F0.wireOp",EDGE,"E11.10.0.8"),sQuery(id+"F0.wireOp",EDGE,"E11.10.0.9"),sQuery(id+"F0.wireOp",EDGE,"E11.10.0.10"),sQuery(id+"F0.wireOp",EDGE,"E11.10.0.11"),sQuery(id+"F0.wireOp",EDGE,"E11.10.0.12"),sQuery(id+"F0.wireOp",EDGE,"E11.10.0.13"),sQuery(id+"F0.wireOp",EDGE,"E11.10.0.14"),sQuery(id+"F0.wireOp",EDGE,"E11.10.0.15"),sQuery(id+"F0.wireOp",EDGE,"E11.10.0.16"),sQuery(id+"F0.wireOp",EDGE,"E11.10.0.17"),sQuery(id+"F0.wireOp",EDGE,"E11.10.0.18"),sQuery(id+"F0.wireOp",EDGE,"E11.10.0.19"),sQuery(id+"F0.wireOp",EDGE,"E11.10.0.20"),sQuery(id+"F0.wireOp",EDGE,"E11.10.0.21"),sQuery(id+"F0.wireOp",EDGE,"E11.10.0.22"),sQuery(id+"F0.wireOp",EDGE,"E11.10.0.23"),sQuery(id+"F0.wireOp",EDGE,"E11.10.0.24"),sQuery(id+"F0.wireOp",EDGE,"E11.10.0.25"),sQuery(id+"F0.wireOp",EDGE,"E11.10.0.26"),sQuery(id+"F0.wireOp",EDGE,"E11.10.0.27"),sQuery(id+"F0.wireOp",EDGE,"E11.11.0.0"),sQuery(id+"F0.wireOp",EDGE,"E11.11.0.1"),sQuery(id+"F0.wireOp",EDGE,"E11.11.0.2"),sQuery(id+"F0.wireOp",EDGE,"E11.11.0.3"),sQuery(id+"F0.wireOp",EDGE,"E11.11.0.4"),sQuery(id+"F0.wireOp",EDGE,"E11.11.0.5"),sQuery(id+"F0.wireOp",EDGE,"E11.11.0.6"),sQuery(id+"F0.wireOp",EDGE,"E11.11.0.7"),sQuery(id+"F0.wireOp",EDGE,"E11.11.0.8"),sQuery(id+"F0.wireOp",EDGE,"E11.11.0.9"),sQuery(id+"F0.wireOp",EDGE,"E11.11.0.10"),sQuery(id+"F0.wireOp",EDGE,"E11.11.0.11"),sQuery(id+"F0.wireOp",EDGE,"E11.11.0.12"),sQuery(id+"F0.wireOp",EDGE,"E11.11.0.13"),sQuery(id+"F0.wireOp",EDGE,"E11.11.0.14"),sQuery(id+"F0.wireOp",EDGE,"E11.11.0.15"),sQuery(id+"F0.wireOp",EDGE,"E11.11.0.16"),sQuery(id+"F0.wireOp",EDGE,"E11.11.0.17"),sQuery(id+"F0.wireOp",EDGE,"E11.11.0.18"),sQuery(id+"F0.wireOp",EDGE,"E11.11.0.19"),sQuery(id+"F0.wireOp",EDGE,"E11.11.0.20"),sQuery(id+"F0.wireOp",EDGE,"E11.11.0.21"),sQuery(id+"F0.wireOp",EDGE,"E11.11.0.22"),sQuery(id+"F0.wireOp",EDGE,"E11.11.0.23"),sQuery(id+"F0.wireOp",EDGE,"E11.11.0.24"),sQuery(id+"F0.wireOp",EDGE,"E11.11.0.25"),sQuery(id+"F0.wireOp",EDGE,"E11.11.0.26"),sQuery(id+"F0.wireOp",EDGE,"E11.11.0.27"),sQuery(id+"F0.wireOp",EDGE,"E11.12.0.0"),sQuery(id+"F0.wireOp",EDGE,"E11.12.0.1"),sQuery(id+"F0.wireOp",EDGE,"E11.12.0.2"),sQuery(id+"F0.wireOp",EDGE,"E11.12.0.3"),sQuery(id+"F0.wireOp",EDGE,"E11.12.0.4"),sQuery(id+"F0.wireOp",EDGE,"E11.12.0.5"),sQuery(id+"F0.wireOp",EDGE,"E11.12.0.6"),sQuery(id+"F0.wireOp",EDGE,"E11.12.0.7"),sQuery(id+"F0.wireOp",EDGE,"E11.12.0.8"),sQuery(id+"F0.wireOp",EDGE,"E11.12.0.9"),sQuery(id+"F0.wireOp",EDGE,"E11.12.0.10"),sQuery(id+"F0.wireOp",EDGE,"E11.12.0.11"),sQuery(id+"F0.wireOp",EDGE,"E11.12.0.12"),sQuery(id+"F0.wireOp",EDGE,"E11.12.0.13"),sQuery(id+"F0.wireOp",EDGE,"E11.12.0.14"),sQuery(id+"F0.wireOp",EDGE,"E11.12.0.15"),sQuery(id+"F0.wireOp",EDGE,"E11.12.0.16"),sQuery(id+"F0.wireOp",EDGE,"E11.12.0.17"),sQuery(id+"F0.wireOp",EDGE,"E11.12.0.18"),sQuery(id+"F0.wireOp",EDGE,"E11.12.0.19"),sQuery(id+"F0.wireOp",EDGE,"E11.12.0.20"),sQuery(id+"F0.wireOp",EDGE,"E11.12.0.21"),sQuery(id+"F0.wireOp",EDGE,"E11.12.0.22"),sQuery(id+"F0.wireOp",EDGE,"E11.12.0.23"),sQuery(id+"F0.wireOp",EDGE,"E11.12.0.24"),sQuery(id+"F0.wireOp",EDGE,"E11.12.0.25"),sQuery(id+"F0.wireOp",EDGE,"E11.12.0.26"),sQuery(id+"F0.wireOp",EDGE,"E11.12.0.27"),sQuery(id+"F0.wireOp",EDGE,"E11.13.0.0"),sQuery(id+"F0.wireOp",EDGE,"E11.13.0.1"),sQuery(id+"F0.wireOp",EDGE,"E11.13.0.2"),sQuery(id+"F0.wireOp",EDGE,"E11.13.0.3"),sQuery(id+"F0.wireOp",EDGE,"E11.13.0.4"),sQuery(id+"F0.wireOp",EDGE,"E11.13.0.5"),sQuery(id+"F0.wireOp",EDGE,"E11.13.0.6"),sQuery(id+"F0.wireOp",EDGE,"E11.13.0.7"),sQuery(id+"F0.wireOp",EDGE,"E11.13.0.8"),sQuery(id+"F0.wireOp",EDGE,"E11.13.0.9"),sQuery(id+"F0.wireOp",EDGE,"E11.13.0.10"),sQuery(id+"F0.wireOp",EDGE,"E11.13.0.11"),sQuery(id+"F0.wireOp",EDGE,"E11.13.0.12"),sQuery(id+"F0.wireOp",EDGE,"E11.13.0.13"),sQuery(id+"F0.wireOp",EDGE,"E11.13.0.14"),sQuery(id+"F0.wireOp",EDGE,"E11.13.0.15"),sQuery(id+"F0.wireOp",EDGE,"E11.13.0.16"),sQuery(id+"F0.wireOp",EDGE,"E11.13.0.17"),sQuery(id+"F0.wireOp",EDGE,"E11.13.0.18"),sQuery(id+"F0.wireOp",EDGE,"E11.13.0.19"),sQuery(id+"F0.wireOp",EDGE,"E11.13.0.20"),sQuery(id+"F0.wireOp",EDGE,"E11.13.0.21"),sQuery(id+"F0.wireOp",EDGE,"E11.13.0.22"),sQuery(id+"F0.wireOp",EDGE,"E11.13.0.23"),sQuery(id+"F0.wireOp",EDGE,"E11.13.0.24"),sQuery(id+"F0.wireOp",EDGE,"E11.13.0.25"),sQuery(id+"F0.wireOp",EDGE,"E11.13.0.26"),sQuery(id+"F0.wireOp",EDGE,"E11.13.0.27"),sQuery(id+"F0.wireOp",EDGE,"E11.14.0.0"),sQuery(id+"F0.wireOp",EDGE,"E11.14.0.1"),sQuery(id+"F0.wireOp",EDGE,"E11.14.0.2"),sQuery(id+"F0.wireOp",EDGE,"E11.14.0.3"),sQuery(id+"F0.wireOp",EDGE,"E11.14.0.4"),sQuery(id+"F0.wireOp",EDGE,"E11.14.0.5"),sQuery(id+"F0.wireOp",EDGE,"E11.14.0.6"),sQuery(id+"F0.wireOp",EDGE,"E11.14.0.7"),sQuery(id+"F0.wireOp",EDGE,"E11.14.0.8"),sQuery(id+"F0.wireOp",EDGE,"E11.14.0.9"),sQuery(id+"F0.wireOp",EDGE,"E11.14.0.10"),sQuery(id+"F0.wireOp",EDGE,"E11.14.0.11"),sQuery(id+"F0.wireOp",EDGE,"E11.14.0.12"),sQuery(id+"F0.wireOp",EDGE,"E11.14.0.13"),sQuery(id+"F0.wireOp",EDGE,"E11.14.0.14"),sQuery(id+"F0.wireOp",EDGE,"E11.14.0.15"),sQuery(id+"F0.wireOp",EDGE,"E11.14.0.16"),sQuery(id+"F0.wireOp",EDGE,"E11.14.0.17"),sQuery(id+"F0.wireOp",EDGE,"E11.14.0.18"),sQuery(id+"F0.wireOp",EDGE,"E11.14.0.19"),sQuery(id+"F0.wireOp",EDGE,"E11.14.0.20"),sQuery(id+"F0.wireOp",EDGE,"E11.14.0.21"),sQuery(id+"F0.wireOp",EDGE,"E11.14.0.22"),sQuery(id+"F0.wireOp",EDGE,"E11.14.0.23"),sQuery(id+"F0.wireOp",EDGE,"E11.14.0.24"),sQuery(id+"F0.wireOp",EDGE,"E11.14.0.25"),sQuery(id+"F0.wireOp",EDGE,"E11.14.0.26"),sQuery(id+"F0.wireOp",EDGE,"E11.14.0.27")])],"isStart":false});
            var sketch = newSketch(context, id + "F4", { "sketchPlane" : qUnion([Q0])});
            skLineSegment(sketch, "E13.bottom", {"start": v(-7.5, -1) * mm, "end": v(7.5, -1) * mm});
            skLineSegment(sketch, "E13.top", {"start": v(-7.5, 1) * mm, "end": v(7.5, 1) * mm});
            skLineSegment(sketch, "E13.left", {"start": v(-7.5, -1) * mm, "end": v(-7.5, 1) * mm});
            skLineSegment(sketch, "E13.right", {"start": v(7.5, -1) * mm, "end": v(7.5, 1) * mm});
            skPoint(sketch, "E13.middle", {"position": v(0, 0) * mm});
            skLineSegment(sketch, "E14.bottom", {"start": v(49, -49) * mm, "end": v(37.4, -49) * mm});
            skLineSegment(sketch, "E14.top", {"start": v(49, -47) * mm, "end": v(37.4, -47) * mm});
            skLineSegment(sketch, "E14.left", {"start": v(49, -49) * mm, "end": v(49, -47) * mm});
            skLineSegment(sketch, "E14.right", {"start": v(37.4, -49) * mm, "end": v(37.4, -47) * mm});
            skLineSegment(sketch, "E15.bottom", {"start": v(49, -49) * mm, "end": v(47, -49) * mm});
            skLineSegment(sketch, "E15.top", {"start": v(49, -37.5) * mm, "end": v(47, -37.5) * mm});
            skLineSegment(sketch, "E15.left", {"start": v(49, -49) * mm, "end": v(49, -37.5) * mm});
            skLineSegment(sketch, "E15.right", {"start": v(47, -49) * mm, "end": v(47, -37.5) * mm});
            skLineSegment(sketch, "E16.bottom", {"start": v(-49, 49) * mm, "end": v(-47, 49) * mm});
            skLineSegment(sketch, "E16.top", {"start": v(-49, 37.5) * mm, "end": v(-47, 37.5) * mm});
            skLineSegment(sketch, "E16.left", {"start": v(-49, 49) * mm, "end": v(-49, 37.5) * mm});
            skLineSegment(sketch, "E16.right", {"start": v(-47, 49) * mm, "end": v(-47, 37.5) * mm});
            skLineSegment(sketch, "E17.bottom", {"start": v(-49, 49) * mm, "end": v(-37.5, 49) * mm});
            skLineSegment(sketch, "E17.top", {"start": v(-49, 47) * mm, "end": v(-37.5, 47) * mm});
            skLineSegment(sketch, "E17.left", {"start": v(-49, 49) * mm, "end": v(-49, 47) * mm});
            skLineSegment(sketch, "E17.right", {"start": v(-37.5, 49) * mm, "end": v(-37.5, 47) * mm});
            skLineSegment(sketch, "E18.bottom", {"start": v(49, 49) * mm, "end": v(37.5, 49) * mm});
            skLineSegment(sketch, "E18.top", {"start": v(49, 47) * mm, "end": v(37.5, 47) * mm});
            skLineSegment(sketch, "E18.left", {"start": v(49, 49) * mm, "end": v(49, 47) * mm});
            skLineSegment(sketch, "E18.right", {"start": v(37.5, 49) * mm, "end": v(37.5, 47) * mm});
            skLineSegment(sketch, "E19.bottom", {"start": v(49, 49) * mm, "end": v(47, 49) * mm});
            skLineSegment(sketch, "E19.top", {"start": v(49, 37.5) * mm, "end": v(47, 37.5) * mm});
            skLineSegment(sketch, "E19.left", {"start": v(49, 49) * mm, "end": v(49, 37.5) * mm});
            skLineSegment(sketch, "E19.right", {"start": v(47, 49) * mm, "end": v(47, 37.5) * mm});
            skLineSegment(sketch, "E20.bottom", {"start": v(-49, -49) * mm, "end": v(-47, -49) * mm});
            skLineSegment(sketch, "E20.top", {"start": v(-49, -37.5) * mm, "end": v(-47, -37.5) * mm});
            skLineSegment(sketch, "E20.left", {"start": v(-49, -49) * mm, "end": v(-49, -37.5) * mm});
            skLineSegment(sketch, "E20.right", {"start": v(-47, -49) * mm, "end": v(-47, -37.5) * mm});
            skLineSegment(sketch, "E21.bottom", {"start": v(-49, -49) * mm, "end": v(-37.5, -49) * mm});
            skLineSegment(sketch, "E21.top", {"start": v(-49, -47) * mm, "end": v(-37.5, -47) * mm});
            skLineSegment(sketch, "E21.left", {"start": v(-49, -49) * mm, "end": v(-49, -47) * mm});
            skLineSegment(sketch, "E21.right", {"start": v(-37.5, -49) * mm, "end": v(-37.5, -47) * mm});
            skSolve(sketch);
        }
        {
            var Q0;
            Q0 = qSketchRegion(id + "F4", true);
            extrude(context, id + "F5", {"entities" : qUnion([Q0]), "operationType" : NewBodyOperationType.ADD, "depth" : 6 * mm, "offsetDistance" : 25 * mm});
        }
        {
            var Q0;
            Q0=makeQuery(id+"F5.boolean.opBoolean","MERGE",EDGE,{"derivedFrom":[makeQuery(id+"F1.opExtrude","SWEPT_EDGE",EDGE,{"disambiguationData":[OSD([sQuery(id+"F0.wireOp",EDGE,"E1.bottom"),sQuery(id+"F0.wireOp",EDGE,"E1.left")])]}),makeQuery(id+"F5.opExtrude","SWEPT_EDGE",EDGE,{"disambiguationData":[OSD([sQuery(id+"F4.wireOp",EDGE,"E17.bottom"),sQuery(id+"F4.wireOp",EDGE,"E17.left")])]})]});
            var Q1;
            Q1=makeQuery(id+"F5.boolean.opBoolean","MERGE",EDGE,{"derivedFrom":[makeQuery(id+"F1.opExtrude","SWEPT_EDGE",EDGE,{"disambiguationData":[OSD([sQuery(id+"F0.wireOp",EDGE,"E0.bottom"),sQuery(id+"F0.wireOp",EDGE,"E0.right")])]}),makeQuery(id+"F5.opExtrude","SWEPT_EDGE",EDGE,{"disambiguationData":[OSD([sQuery(id+"F4.wireOp",EDGE,"E19.bottom"),sQuery(id+"F4.wireOp",EDGE,"E19.left")])]})]});
            var Q2;
            Q2=makeQuery(id+"F5.boolean.opBoolean","MERGE",EDGE,{"derivedFrom":[makeQuery(id+"F1.opExtrude","SWEPT_EDGE",EDGE,{"disambiguationData":[OSD([sQuery(id+"F0.wireOp",EDGE,"E0.top"),sQuery(id+"F0.wireOp",EDGE,"E0.right")])]}),makeQuery(id+"F5.opExtrude","SWEPT_EDGE",EDGE,{"disambiguationData":[OSD([sQuery(id+"F4.wireOp",EDGE,"E15.bottom"),sQuery(id+"F4.wireOp",EDGE,"E15.left")])]})]});
            var Q3;
            Q3=makeQuery(id+"F5.boolean.opBoolean","MERGE",EDGE,{"derivedFrom":[makeQuery(id+"F1.opExtrude","SWEPT_EDGE",EDGE,{"disambiguationData":[OSD([sQuery(id+"F0.wireOp",EDGE,"E0.top"),sQuery(id+"F0.wireOp",EDGE,"E0.left")])]}),makeQuery(id+"F5.opExtrude","SWEPT_EDGE",EDGE,{"disambiguationData":[OSD([sQuery(id+"F4.wireOp",EDGE,"GKlqXLWi-vUNO-DPzL-R5q6-mg1LjXUYxONC.bottom"),sQuery(id+"F4.wireOp",EDGE,"GKlqXLWi-vUNO-DPzL-R5q6-mg1LjXUYxONC.left")])]})]});
            fillet(context, id + "F6", {"entities" : qUnion([Q0, Q1, Q2, Q3]), "radius" : 5 * mm, "tangentPropagation" : true, "allowEdgeOverflow" : false});
        }
    });
